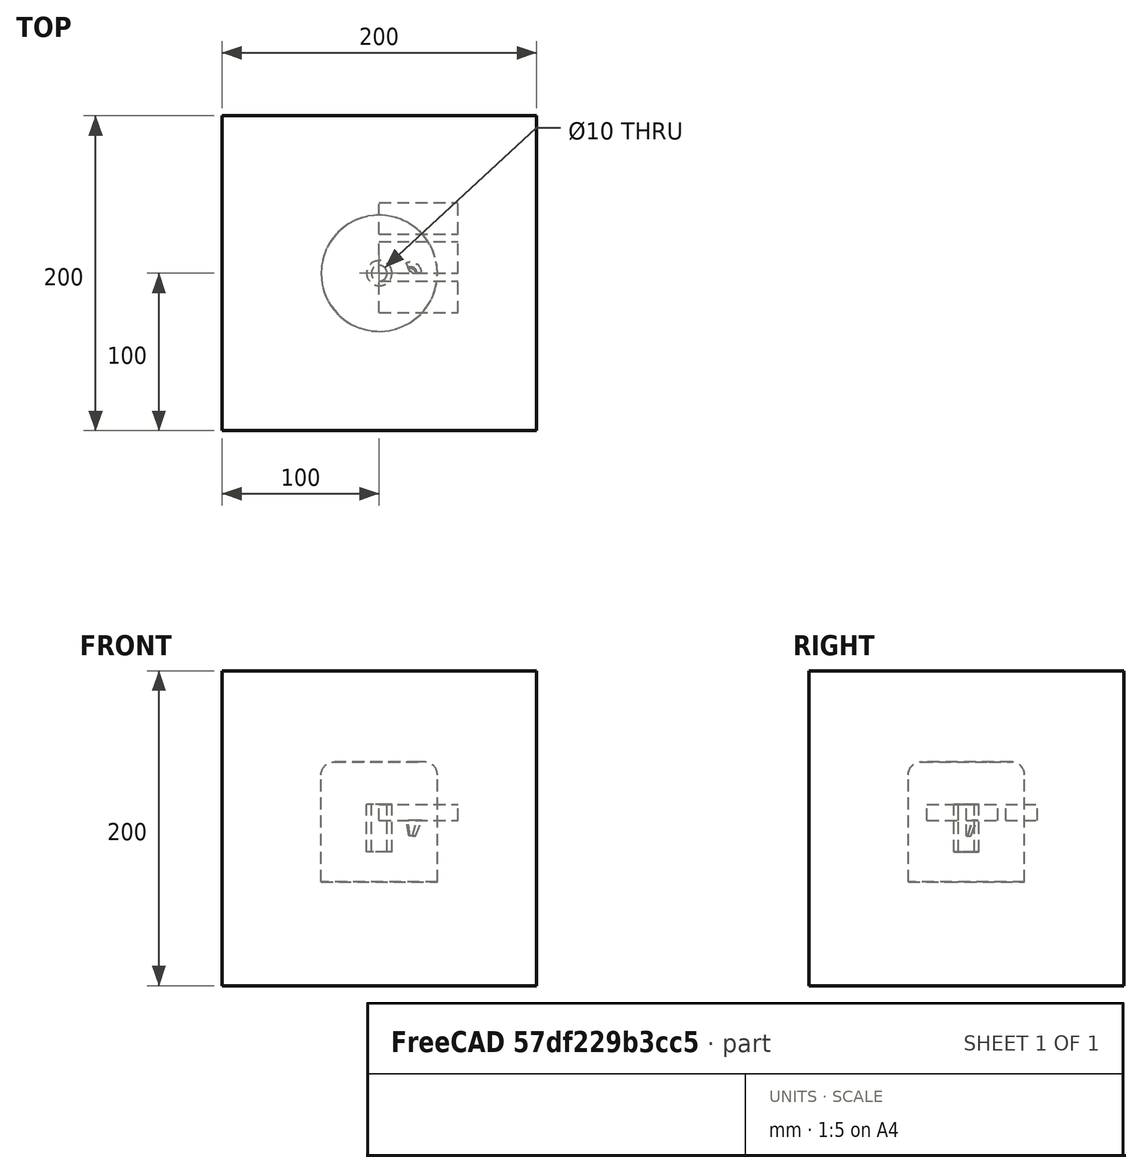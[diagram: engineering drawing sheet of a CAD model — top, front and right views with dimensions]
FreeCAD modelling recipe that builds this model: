
FCSTD DOCUMENT  (FreeCAD 0.19RUnknown)
Label: assemblyTest
License: All rights reserved
LicenseURL: http://en.wikipedia.org/wiki/All_rights_reserved
objects: App::DocumentObjectGroupPython×1254, Part::FeaturePython×6, App::Part×5, Part::Box×3, Part::Fuse×2
note: 11 computed .brp shape members not serialized (recipe doc carries the construction recipe); baked Part::Feature solids carry a one-line shape summary decoded from their .brp

FEATURE [App::DocumentObjectGroupPython] HALFPI  # scripted group (container) (typed FeaturePython)
  name = HALFPI
  value = pi/2.
FEATURE [App::DocumentObjectGroupPython] PI  # scripted group (container) (typed FeaturePython)
  name = PI
  value = 1.*pi
FEATURE [App::DocumentObjectGroupPython] TWOPI  # scripted group (container) (typed FeaturePython)
  name = TWOPI
  value = 2.*pi
FEATURE [App::DocumentObjectGroupPython] Variables  # scripted group (container) (typed FeaturePython)
FEATURE [App::DocumentObjectGroupPython] Quantities  # scripted group (container) (typed FeaturePython)
FEATURE [App::DocumentObjectGroupPython] Isotopes  # scripted group (container) (typed FeaturePython)
FEATURE [App::DocumentObjectGroupPython] Elements  # scripted group (container) (typed FeaturePython)
FEATURE [App::DocumentObjectGroupPython] G4Isotopes  # scripted group (container) (typed FeaturePython)
FEATURE [App::DocumentObjectGroupPython] H_element  # scripted group (container) (typed FeaturePython)
  Z = 1
  atom_value = 1.008
  formula = H
  name = H_element
FEATURE [App::DocumentObjectGroupPython] He_element  # scripted group (container) (typed FeaturePython)
  Z = 2
  atom_value = 4.0026
  formula = He
  name = He_element
FEATURE [App::DocumentObjectGroupPython] Li_element  # scripted group (container) (typed FeaturePython)
  Z = 3
  atom_value = 6.94
  formula = Li
  name = Li_element
FEATURE [App::DocumentObjectGroupPython] Be_element  # scripted group (container) (typed FeaturePython)
  Z = 4
  atom_value = 9.01218
  formula = Be
  name = Be_element
FEATURE [App::DocumentObjectGroupPython] B_element  # scripted group (container) (typed FeaturePython)
  Z = 5
  atom_value = 10.81
  formula = B
  name = B_element
FEATURE [App::DocumentObjectGroupPython] C_element  # scripted group (container) (typed FeaturePython)
  Z = 6
  atom_value = 12.011
  formula = C
  name = C_element
FEATURE [App::DocumentObjectGroupPython] N_element  # scripted group (container) (typed FeaturePython)
  Z = 7
  atom_value = 14.007
  formula = N
  name = N_element
FEATURE [App::DocumentObjectGroupPython] O_element  # scripted group (container) (typed FeaturePython)
  Z = 8
  atom_value = 15.999
  formula = O
  name = O_element
FEATURE [App::DocumentObjectGroupPython] F_element  # scripted group (container) (typed FeaturePython)
  Z = 9
  atom_value = 18.9984
  formula = F
  name = F_element
FEATURE [App::DocumentObjectGroupPython] Ne_element  # scripted group (container) (typed FeaturePython)
  Z = 10
  atom_value = 20.1797
  formula = Ne
  name = Ne_element
FEATURE [App::DocumentObjectGroupPython] Na_element  # scripted group (container) (typed FeaturePython)
  Z = 11
  atom_value = 22.9898
  formula = Na
  name = Na_element
FEATURE [App::DocumentObjectGroupPython] Mg_element  # scripted group (container) (typed FeaturePython)
  Z = 12
  atom_value = 24.305
  formula = Mg
  name = Mg_element
FEATURE [App::DocumentObjectGroupPython] Al_element  # scripted group (container) (typed FeaturePython)
  Z = 13
  atom_value = 26.9815
  formula = Al
  name = Al_element
FEATURE [App::DocumentObjectGroupPython] Si_element  # scripted group (container) (typed FeaturePython)
  Z = 14
  atom_value = 28.085
  formula = Si
  name = Si_element
FEATURE [App::DocumentObjectGroupPython] P_element  # scripted group (container) (typed FeaturePython)
  Z = 15
  atom_value = 30.9738
  formula = P
  name = P_element
FEATURE [App::DocumentObjectGroupPython] S_element  # scripted group (container) (typed FeaturePython)
  Z = 16
  atom_value = 32.06
  formula = S
  name = S_element
FEATURE [App::DocumentObjectGroupPython] Cl_element  # scripted group (container) (typed FeaturePython)
  Z = 17
  atom_value = 35.45
  formula = Cl
  name = Cl_element
FEATURE [App::DocumentObjectGroupPython] Ar_element  # scripted group (container) (typed FeaturePython)
  Z = 18
  atom_value = 39.95
  formula = Ar
  name = Ar_element
FEATURE [App::DocumentObjectGroupPython] K_element  # scripted group (container) (typed FeaturePython)
  Z = 19
  atom_value = 39.0983
  formula = K
  name = K_element
FEATURE [App::DocumentObjectGroupPython] Ca_element  # scripted group (container) (typed FeaturePython)
  Z = 20
  atom_value = 40.078
  formula = Ca
  name = Ca_element
FEATURE [App::DocumentObjectGroupPython] Sc_element  # scripted group (container) (typed FeaturePython)
  Z = 21
  atom_value = 44.9559
  formula = Sc
  name = Sc_element
FEATURE [App::DocumentObjectGroupPython] Ti_element  # scripted group (container) (typed FeaturePython)
  Z = 22
  atom_value = 47.867
  formula = Ti
  name = Ti_element
FEATURE [App::DocumentObjectGroupPython] V_element  # scripted group (container) (typed FeaturePython)
  Z = 23
  atom_value = 50.9415
  formula = V
  name = V_element
FEATURE [App::DocumentObjectGroupPython] Cr_element  # scripted group (container) (typed FeaturePython)
  Z = 24
  atom_value = 51.9961
  formula = Cr
  name = Cr_element
FEATURE [App::DocumentObjectGroupPython] Mn_element  # scripted group (container) (typed FeaturePython)
  Z = 25
  atom_value = 54.938
  formula = Mn
  name = Mn_element
FEATURE [App::DocumentObjectGroupPython] Fe_element  # scripted group (container) (typed FeaturePython)
  Z = 26
  atom_value = 55.845
  formula = Fe
  name = Fe_element
FEATURE [App::DocumentObjectGroupPython] Co_element  # scripted group (container) (typed FeaturePython)
  Z = 27
  atom_value = 58.9332
  formula = Co
  name = Co_element
FEATURE [App::DocumentObjectGroupPython] Ni_element  # scripted group (container) (typed FeaturePython)
  Z = 28
  atom_value = 58.6934
  formula = Ni
  name = Ni_element
FEATURE [App::DocumentObjectGroupPython] Cu_element  # scripted group (container) (typed FeaturePython)
  Z = 29
  atom_value = 63.546
  formula = Cu
  name = Cu_element
FEATURE [App::DocumentObjectGroupPython] Zn_element  # scripted group (container) (typed FeaturePython)
  Z = 30
  atom_value = 65.38
  formula = Zn
  name = Zn_element
FEATURE [App::DocumentObjectGroupPython] Ga_element  # scripted group (container) (typed FeaturePython)
  Z = 31
  atom_value = 69.723
  formula = Ga
  name = Ga_element
FEATURE [App::DocumentObjectGroupPython] Ge_element  # scripted group (container) (typed FeaturePython)
  Z = 32
  atom_value = 72.63
  formula = Ge
  name = Ge_element
FEATURE [App::DocumentObjectGroupPython] As_element  # scripted group (container) (typed FeaturePython)
  Z = 33
  atom_value = 74.9216
  formula = As
  name = As_element
FEATURE [App::DocumentObjectGroupPython] Se_element  # scripted group (container) (typed FeaturePython)
  Z = 34
  atom_value = 78.971
  formula = Se
  name = Se_element
FEATURE [App::DocumentObjectGroupPython] Br_element  # scripted group (container) (typed FeaturePython)
  Z = 35
  atom_value = 79.904
  formula = Br
  name = Br_element
FEATURE [App::DocumentObjectGroupPython] Kr_element  # scripted group (container) (typed FeaturePython)
  Z = 36
  atom_value = 83.798
  formula = Kr
  name = Kr_element
FEATURE [App::DocumentObjectGroupPython] Rb_element  # scripted group (container) (typed FeaturePython)
  Z = 37
  atom_value = 85.4678
  formula = Rb
  name = Rb_element
FEATURE [App::DocumentObjectGroupPython] Sr_element  # scripted group (container) (typed FeaturePython)
  Z = 38
  atom_value = 87.62
  formula = Sr
  name = Sr_element
FEATURE [App::DocumentObjectGroupPython] Y_element  # scripted group (container) (typed FeaturePython)
  Z = 39
  atom_value = 88.9058
  formula = Y
  name = Y_element
FEATURE [App::DocumentObjectGroupPython] Zr_element  # scripted group (container) (typed FeaturePython)
  Z = 40
  atom_value = 91.224
  formula = Zr
  name = Zr_element
FEATURE [App::DocumentObjectGroupPython] Nb_element  # scripted group (container) (typed FeaturePython)
  Z = 41
  atom_value = 92.9064
  formula = Nb
  name = Nb_element
FEATURE [App::DocumentObjectGroupPython] Mo_element  # scripted group (container) (typed FeaturePython)
  Z = 42
  atom_value = 95.95
  formula = Mo
  name = Mo_element
FEATURE [App::DocumentObjectGroupPython] Tc_element  # scripted group (container) (typed FeaturePython)
  Z = 43
  atom_value = 97
  formula = Tc
  name = Tc_element
FEATURE [App::DocumentObjectGroupPython] Ru_element  # scripted group (container) (typed FeaturePython)
  Z = 44
  atom_value = 101.07
  formula = Ru
  name = Ru_element
FEATURE [App::DocumentObjectGroupPython] Rh_element  # scripted group (container) (typed FeaturePython)
  Z = 45
  atom_value = 102.905
  formula = Rh
  name = Rh_element
FEATURE [App::DocumentObjectGroupPython] Pd_element  # scripted group (container) (typed FeaturePython)
  Z = 46
  atom_value = 106.42
  formula = Pd
  name = Pd_element
FEATURE [App::DocumentObjectGroupPython] Ag_element  # scripted group (container) (typed FeaturePython)
  Z = 47
  atom_value = 107.868
  formula = Ag
  name = Ag_element
FEATURE [App::DocumentObjectGroupPython] Cd_element  # scripted group (container) (typed FeaturePython)
  Z = 48
  atom_value = 112.414
  formula = Cd
  name = Cd_element
FEATURE [App::DocumentObjectGroupPython] In_element  # scripted group (container) (typed FeaturePython)
  Z = 49
  atom_value = 114.818
  formula = In
  name = In_element
FEATURE [App::DocumentObjectGroupPython] Sn_element  # scripted group (container) (typed FeaturePython)
  Z = 50
  atom_value = 118.71
  formula = Sn
  name = Sn_element
FEATURE [App::DocumentObjectGroupPython] Sb_element  # scripted group (container) (typed FeaturePython)
  Z = 51
  atom_value = 121.76
  formula = Sb
  name = Sb_element
FEATURE [App::DocumentObjectGroupPython] Te_element  # scripted group (container) (typed FeaturePython)
  Z = 52
  atom_value = 127.6
  formula = Te
  name = Te_element
FEATURE [App::DocumentObjectGroupPython] I_element  # scripted group (container) (typed FeaturePython)
  Z = 53
  atom_value = 126.904
  formula = I
  name = I_element
FEATURE [App::DocumentObjectGroupPython] Xe_element  # scripted group (container) (typed FeaturePython)
  Z = 54
  atom_value = 131.293
  formula = Xe
  name = Xe_element
FEATURE [App::DocumentObjectGroupPython] Cs_element  # scripted group (container) (typed FeaturePython)
  Z = 55
  atom_value = 132.905
  formula = Cs
  name = Cs_element
FEATURE [App::DocumentObjectGroupPython] Ba_element  # scripted group (container) (typed FeaturePython)
  Z = 56
  atom_value = 137.327
  formula = Ba
  name = Ba_element
FEATURE [App::DocumentObjectGroupPython] La_element  # scripted group (container) (typed FeaturePython)
  Z = 57
  atom_value = 138.905
  formula = La
  name = La_element
FEATURE [App::DocumentObjectGroupPython] Ce_element  # scripted group (container) (typed FeaturePython)
  Z = 58
  atom_value = 140.116
  formula = Ce
  name = Ce_element
FEATURE [App::DocumentObjectGroupPython] Pr_element  # scripted group (container) (typed FeaturePython)
  Z = 59
  atom_value = 140.908
  formula = Pr
  name = Pr_element
FEATURE [App::DocumentObjectGroupPython] Nd_element  # scripted group (container) (typed FeaturePython)
  Z = 60
  atom_value = 144.242
  formula = Nd
  name = Nd_element
FEATURE [App::DocumentObjectGroupPython] Pm_element  # scripted group (container) (typed FeaturePython)
  Z = 61
  atom_value = 145
  formula = Pm
  name = Pm_element
FEATURE [App::DocumentObjectGroupPython] Sm_element  # scripted group (container) (typed FeaturePython)
  Z = 62
  atom_value = 150.36
  formula = Sm
  name = Sm_element
FEATURE [App::DocumentObjectGroupPython] Eu_element  # scripted group (container) (typed FeaturePython)
  Z = 63
  atom_value = 151.964
  formula = Eu
  name = Eu_element
FEATURE [App::DocumentObjectGroupPython] Gd_element  # scripted group (container) (typed FeaturePython)
  Z = 64
  atom_value = 157.25
  formula = Gd
  name = Gd_element
FEATURE [App::DocumentObjectGroupPython] Tb_element  # scripted group (container) (typed FeaturePython)
  Z = 65
  atom_value = 158.925
  formula = Tb
  name = Tb_element
FEATURE [App::DocumentObjectGroupPython] Dy_element  # scripted group (container) (typed FeaturePython)
  Z = 66
  atom_value = 162.5
  formula = Dy
  name = Dy_element
FEATURE [App::DocumentObjectGroupPython] Ho_element  # scripted group (container) (typed FeaturePython)
  Z = 67
  atom_value = 164.93
  formula = Ho
  name = Ho_element
FEATURE [App::DocumentObjectGroupPython] Er_element  # scripted group (container) (typed FeaturePython)
  Z = 68
  atom_value = 167.259
  formula = Er
  name = Er_element
FEATURE [App::DocumentObjectGroupPython] Tm_element  # scripted group (container) (typed FeaturePython)
  Z = 69
  atom_value = 168.934
  formula = Tm
  name = Tm_element
FEATURE [App::DocumentObjectGroupPython] Yb_element  # scripted group (container) (typed FeaturePython)
  Z = 70
  atom_value = 173.045
  formula = Yb
  name = Yb_element
FEATURE [App::DocumentObjectGroupPython] Lu_element  # scripted group (container) (typed FeaturePython)
  Z = 71
  atom_value = 174.967
  formula = Lu
  name = Lu_element
FEATURE [App::DocumentObjectGroupPython] Hf_element  # scripted group (container) (typed FeaturePython)
  Z = 72
  atom_value = 178.49
  formula = Hf
  name = Hf_element
FEATURE [App::DocumentObjectGroupPython] Ta_element  # scripted group (container) (typed FeaturePython)
  Z = 73
  atom_value = 180.948
  formula = Ta
  name = Ta_element
FEATURE [App::DocumentObjectGroupPython] W_element  # scripted group (container) (typed FeaturePython)
  Z = 74
  atom_value = 183.84
  formula = W
  name = W_element
FEATURE [App::DocumentObjectGroupPython] Re_element  # scripted group (container) (typed FeaturePython)
  Z = 75
  atom_value = 186.207
  formula = Re
  name = Re_element
FEATURE [App::DocumentObjectGroupPython] Os_element  # scripted group (container) (typed FeaturePython)
  Z = 76
  atom_value = 190.23
  formula = Os
  name = Os_element
FEATURE [App::DocumentObjectGroupPython] Ir_element  # scripted group (container) (typed FeaturePython)
  Z = 77
  atom_value = 192.217
  formula = Ir
  name = Ir_element
FEATURE [App::DocumentObjectGroupPython] Pt_element  # scripted group (container) (typed FeaturePython)
  Z = 78
  atom_value = 195.084
  formula = Pt
  name = Pt_element
FEATURE [App::DocumentObjectGroupPython] Au_element  # scripted group (container) (typed FeaturePython)
  Z = 79
  atom_value = 196.967
  formula = Au
  name = Au_element
FEATURE [App::DocumentObjectGroupPython] Hg_element  # scripted group (container) (typed FeaturePython)
  Z = 80
  atom_value = 200.592
  formula = Hg
  name = Hg_element
FEATURE [App::DocumentObjectGroupPython] Tl_element  # scripted group (container) (typed FeaturePython)
  Z = 81
  atom_value = 204.38
  formula = Tl
  name = Tl_element
FEATURE [App::DocumentObjectGroupPython] Pb_element  # scripted group (container) (typed FeaturePython)
  Z = 82
  atom_value = 207.2
  formula = Pb
  name = Pb_element
FEATURE [App::DocumentObjectGroupPython] Bi_element  # scripted group (container) (typed FeaturePython)
  Z = 83
  atom_value = 208.98
  formula = Bi
  name = Bi_element
FEATURE [App::DocumentObjectGroupPython] Po_element  # scripted group (container) (typed FeaturePython)
  Z = 84
  atom_value = 209
  formula = Po
  name = Po_element
FEATURE [App::DocumentObjectGroupPython] At_element  # scripted group (container) (typed FeaturePython)
  Z = 85
  atom_value = 210
  formula = At
  name = At_element
FEATURE [App::DocumentObjectGroupPython] Rn_element  # scripted group (container) (typed FeaturePython)
  Z = 86
  atom_value = 222
  formula = Rn
  name = Rn_element
FEATURE [App::DocumentObjectGroupPython] Fr_element  # scripted group (container) (typed FeaturePython)
  Z = 87
  atom_value = 223
  formula = Fr
  name = Fr_element
FEATURE [App::DocumentObjectGroupPython] Ra_element  # scripted group (container) (typed FeaturePython)
  Z = 88
  atom_value = 226
  formula = Ra
  name = Ra_element
FEATURE [App::DocumentObjectGroupPython] Ac_element  # scripted group (container) (typed FeaturePython)
  Z = 89
  atom_value = 227
  formula = Ac
  name = Ac_element
FEATURE [App::DocumentObjectGroupPython] Th_element  # scripted group (container) (typed FeaturePython)
  Z = 90
  atom_value = 232.038
  formula = Th
  name = Th_element
FEATURE [App::DocumentObjectGroupPython] Pa_element  # scripted group (container) (typed FeaturePython)
  Z = 91
  atom_value = 231.036
  formula = Pa
  name = Pa_element
FEATURE [App::DocumentObjectGroupPython] U_element  # scripted group (container) (typed FeaturePython)
  Z = 92
  atom_value = 238.029
  formula = U
  name = U_element
FEATURE [App::DocumentObjectGroupPython] Np_element  # scripted group (container) (typed FeaturePython)
  Z = 93
  atom_value = 237
  formula = Np
  name = Np_element
FEATURE [App::DocumentObjectGroupPython] Pu_element  # scripted group (container) (typed FeaturePython)
  Z = 94
  atom_value = 244
  formula = Pu
  name = Pu_element
FEATURE [App::DocumentObjectGroupPython] Am_element  # scripted group (container) (typed FeaturePython)
  Z = 95
  atom_value = 243
  formula = Am
  name = Am_element
FEATURE [App::DocumentObjectGroupPython] Cm_element  # scripted group (container) (typed FeaturePython)
  Z = 96
  atom_value = 247
  formula = Cm
  name = Cm_element
FEATURE [App::DocumentObjectGroupPython] Bk_element  # scripted group (container) (typed FeaturePython)
  Z = 97
  atom_value = 247
  formula = Bk
  name = Bk_element
FEATURE [App::DocumentObjectGroupPython] Cf_element  # scripted group (container) (typed FeaturePython)
  Z = 98
  atom_value = 251
  formula = Cf
  name = Cf_element
FEATURE [App::DocumentObjectGroupPython] G4Elements  # scripted group (container) (typed FeaturePython)
  Group = -> [H_element,He_element,Li_element,Be_element,B_element,C_element,N_element,O_element,F_element,Ne_element,Na_element,Mg_element,Al_element,Si_element,P_element,S_element,Cl_element,Ar_element,K_element,Ca_element,Sc_element,Ti_element,V_element,Cr_element,Mn_element,Fe_element,Co_element,Ni_element,Cu_element,Zn_element,Ga_element,Ge_element,As_element,Se_element,Br_element,Kr_element,Rb_element,+61 more]
FEATURE [Part::FeaturePython] GDMLBox_WorldBox  # WARN: FeaturePython — macro-defined, semantics opaque (R4)
  lunit = 2
  material = 5
  x = 200
  y = 200
  z = 200
FEATURE [App::DocumentObjectGroupPython] HALFPI001  # scripted group (container) (typed FeaturePython)
  name = HALFPI
  value = pi/2.
FEATURE [App::DocumentObjectGroupPython] PI001  # scripted group (container) (typed FeaturePython)
  name = PI
  value = 1.*pi
FEATURE [App::DocumentObjectGroupPython] TWOPI001  # scripted group (container) (typed FeaturePython)
  name = TWOPI
  value = 2.*pi
FEATURE [App::DocumentObjectGroupPython] HALFPI001001  # scripted group (container) (typed FeaturePython)
  name = HALFPI001
  value = pi/2.
FEATURE [App::DocumentObjectGroupPython] PI001001  # scripted group (container) (typed FeaturePython)
  name = PI001
  value = 1.*pi
FEATURE [App::DocumentObjectGroupPython] TWOPI001001  # scripted group (container) (typed FeaturePython)
  name = TWOPI001
  value = 2.*pi
FEATURE [App::DocumentObjectGroupPython] Constants  # scripted group (container) (typed FeaturePython)
  Group = -> [HALFPI,PI,TWOPI,HALFPI001,PI001,TWOPI001,HALFPI001001,PI001001,TWOPI001001]
FEATURE [Part::FeaturePython] GDMLTorus_Torus  # WARN: FeaturePython — macro-defined, semantics opaque (R4)
  aunit = deg
  deltaphi = 360
  lunit = 2
  material = 0
  rmax = 8
  rmin = 0
  rtor = 28.9
  startphi = 0
FEATURE [Part::FeaturePython] GDMLTube_Tube  # WARN: FeaturePython — macro-defined, semantics opaque (R4)
  aunit = 1
  deltaphi = 360
  lunit = 2
  material = 0
  rmax = 28.9
  rmin = 0
  startphi = 0
  z = 16
FEATURE [Part::FeaturePython] GDMLTube_Tube001  label="GDMLTube_T_1"  # WARN: FeaturePython — macro-defined, semantics opaque (R4)
  Placement = pos=(0,0,-34) rot=(0,0,-1;0.349066rad)
  aunit = 1
  deltaphi = 360
  lunit = 2
  material = 0
  rmax = 36.9
  rmin = 0
  startphi = 0
  z = 68
FEATURE [Part::Fuse] Union
  Base = -> GDMLTorus_Torus
  Placement = pos=(0,0,0) rot=(0,0,1;0.523599rad)
  Tool = -> GDMLTube_Tube
FEATURE [Part::Fuse] Union001  label="U1"
  Base = -> Union
  Placement = pos=(0,0,34) rot=(0,0,1;0rad)
  Tool = -> GDMLTube_Tube001
  material = 211
FEATURE [App::Part] Bool_Union001  label="Detector"
  Group = -> [GDMLTorus_Torus,GDMLTube_Tube,Union,GDMLTube_Tube001,Union001]
  Origin = -> Origin005
FEATURE [Part::FeaturePython] GDMLTube_Tube002  # WARN: FeaturePython — macro-defined, semantics opaque (R4)
  aunit = 1
  deltaphi = 360
  lunit = 2
  material = 109
  rmax = 8
  rmin = 5
  startphi = 0
  z = 30
FEATURE [Part::Box] Box  label="Cube"
  AttacherType = Attacher::AttachEngine3D
  Height = 10
  Length = 50
  Placement = pos=(0,0,5) rot=(0,0,1;0rad)
  Width = 20
  material = 441
FEATURE [Part::Box] Box001  label="Cube001"
  AttacherType = Attacher::AttachEngine3D
  Height = 10
  Length = 50
  Placement = pos=(0,25,5) rot=(0,0,1;0rad)
  Width = 20
  material = 441
FEATURE [Part::Box] Box002  label="Cube002"
  AttacherType = Attacher::AttachEngine3D
  Height = 10
  Length = 50
  Placement = pos=(0,-25,5) rot=(0,0,1;0rad)
  Width = 20
  material = 261
FEATURE [App::Part] Part001  label="shieldAssembly"
  Group = -> [Box,Box001,Box002]
  Origin = -> Origin008
  Placement = pos=(0,0,58) rot=(0,0,1;0rad)
FEATURE [App::DocumentObjectGroupPython] H_element553  label="H_element : 0.246"  # scripted group (container) (typed FeaturePython)
  n = 0.101327
FEATURE [App::DocumentObjectGroupPython] C_element593  label="C_element : 0.974"  # scripted group (container) (typed FeaturePython)
  n = 0.7755
FEATURE [App::DocumentObjectGroupPython] N_element273  label="N_element : 0.828"  # scripted group (container) (typed FeaturePython)
  n = 0.035057
FEATURE [App::DocumentObjectGroupPython] O_element521  label="O_element : 0.966"  # scripted group (container) (typed FeaturePython)
  n = 0.0523159
FEATURE [App::DocumentObjectGroupPython] F_element077  label="F_element : 0.727"  # scripted group (container) (typed FeaturePython)
  n = 0.017422
FEATURE [App::DocumentObjectGroupPython] Ca_element057  label="Ca_element : 0.240"  # scripted group (container) (typed FeaturePython)
  n = 0.018378
FEATURE [App::DocumentObjectGroupPython] G4_A_150_TISSUE  label="G4_A-150_TISSUE"  # scripted group (container) (typed FeaturePython)
  Dunit = g/cm3
  Dvalue = 1.127
  Group = -> [H_element553,C_element593,N_element273,O_element521,F_element077,Ca_element057]
  conduct = 2
  density = 1
  expand = 3
  formula = G4_A-150_TISSUE
  name = G4_A-150_TISSUE
  specific = 4
FEATURE [App::DocumentObjectGroupPython] C_element594  label="C_element : 390"  # scripted group (container) (typed FeaturePython)
  n = 3
  ref = C_element
FEATURE [App::DocumentObjectGroupPython] H_element554  label="H_element : 358"  # scripted group (container) (typed FeaturePython)
  n = 6
  ref = H_element
FEATURE [App::DocumentObjectGroupPython] O_element522  label="O_element : 335"  # scripted group (container) (typed FeaturePython)
  n = 1
  ref = O_element
FEATURE [App::DocumentObjectGroupPython] G4_ACETONE  # scripted group (container) (typed FeaturePython)
  Dunit = g/cm3
  Dvalue = 0.7899
  Group = -> [C_element594,H_element554,O_element522]
  conduct = 2
  density = 1
  expand = 3
  formula = G4_ACETONE
  name = G4_ACETONE
  specific = 4
FEATURE [App::DocumentObjectGroupPython] C_element595  label="C_element : 391"  # scripted group (container) (typed FeaturePython)
  n = 2
  ref = C_element
FEATURE [App::DocumentObjectGroupPython] H_element555  label="H_element : 359"  # scripted group (container) (typed FeaturePython)
  n = 2
  ref = H_element
FEATURE [App::DocumentObjectGroupPython] G4_ACETYLENE  # scripted group (container) (typed FeaturePython)
  Dunit = g/cm3
  Dvalue = 0.0010967
  Group = -> [C_element595,H_element555]
  conduct = 2
  density = 1
  expand = 3
  formula = G4_ACETYLENE
  name = G4_ACETYLENE
  specific = 4
FEATURE [App::DocumentObjectGroupPython] C_element596  label="C_element : 392"  # scripted group (container) (typed FeaturePython)
  n = 5
  ref = C_element
FEATURE [App::DocumentObjectGroupPython] H_element556  label="H_element : 360"  # scripted group (container) (typed FeaturePython)
  n = 5
  ref = H_element
FEATURE [App::DocumentObjectGroupPython] N_element274  label="N_element : 154"  # scripted group (container) (typed FeaturePython)
  n = 5
  ref = N_element
FEATURE [App::DocumentObjectGroupPython] G4_ADENINE  # scripted group (container) (typed FeaturePython)
  Dunit = g/cm3
  Dvalue = 1.6
  Group = -> [C_element596,H_element556,N_element274]
  conduct = 2
  density = 1
  expand = 3
  formula = G4_ADENINE
  name = G4_ADENINE
  specific = 4
FEATURE [App::DocumentObjectGroupPython] H_element557  label="H_element : 0.247"  # scripted group (container) (typed FeaturePython)
  n = 0.114
FEATURE [App::DocumentObjectGroupPython] C_element597  label="C_element : 0.975"  # scripted group (container) (typed FeaturePython)
  n = 0.598
FEATURE [App::DocumentObjectGroupPython] N_element275  label="N_element : 0.829"  # scripted group (container) (typed FeaturePython)
  n = 0.007
FEATURE [App::DocumentObjectGroupPython] O_element523  label="O_element : 0.967"  # scripted group (container) (typed FeaturePython)
  n = 0.278
FEATURE [App::DocumentObjectGroupPython] Na_element081  label="Na_element : 0.142"  # scripted group (container) (typed FeaturePython)
  n = 0.001
FEATURE [App::DocumentObjectGroupPython] S_element093  label="S_element : 0.065"  # scripted group (container) (typed FeaturePython)
  n = 0.001
FEATURE [App::DocumentObjectGroupPython] Cl_element121  label="Cl_element : 0.627"  # scripted group (container) (typed FeaturePython)
  n = 0.001
FEATURE [App::DocumentObjectGroupPython] G4_ADIPOSE_TISSUE_ICRP  # scripted group (container) (typed FeaturePython)
  Dunit = g/cm3
  Dvalue = 0.95
  Group = -> [H_element557,C_element597,N_element275,O_element523,Na_element081,S_element093,Cl_element121]
  conduct = 2
  density = 1
  expand = 3
  formula = G4_ADIPOSE_TISSUE_ICRP
  name = G4_ADIPOSE_TISSUE_ICRP
  specific = 4
FEATURE [App::DocumentObjectGroupPython] C_element598  label="C_element : 0.976"  # scripted group (container) (typed FeaturePython)
  n = 0.000124
FEATURE [App::DocumentObjectGroupPython] N_element276  label="N_element : 0.830"  # scripted group (container) (typed FeaturePython)
  n = 0.755268
FEATURE [App::DocumentObjectGroupPython] O_element524  label="O_element : 0.968"  # scripted group (container) (typed FeaturePython)
  n = 0.231781
FEATURE [App::DocumentObjectGroupPython] Ar_element009  label="Ar_element : 0.016"  # scripted group (container) (typed FeaturePython)
  n = 0.012827
FEATURE [App::DocumentObjectGroupPython] G4_AIR  # scripted group (container) (typed FeaturePython)
  Dunit = g/cm3
  Dvalue = 0.00120479
  Group = -> [C_element598,N_element276,O_element524,Ar_element009]
  conduct = 2
  density = 1
  expand = 3
  formula = G4_AIR
  name = G4_AIR
  specific = 4
FEATURE [App::DocumentObjectGroupPython] C_element599  label="C_element : 393"  # scripted group (container) (typed FeaturePython)
  n = 3
  ref = C_element
FEATURE [App::DocumentObjectGroupPython] H_element558  label="H_element : 361"  # scripted group (container) (typed FeaturePython)
  n = 7
  ref = H_element
FEATURE [App::DocumentObjectGroupPython] N_element277  label="N_element : 155"  # scripted group (container) (typed FeaturePython)
  n = 1
  ref = N_element
FEATURE [App::DocumentObjectGroupPython] O_element525  label="O_element : 336"  # scripted group (container) (typed FeaturePython)
  n = 2
  ref = O_element
FEATURE [App::DocumentObjectGroupPython] G4_ALANINE  # scripted group (container) (typed FeaturePython)
  Dunit = g/cm3
  Dvalue = 1.42
  Group = -> [C_element599,H_element558,N_element277,O_element525]
  conduct = 2
  density = 1
  expand = 3
  formula = G4_ALANINE
  name = G4_ALANINE
  specific = 4
FEATURE [App::DocumentObjectGroupPython] Al_element017  label="Al_element : 007"  # scripted group (container) (typed FeaturePython)
  n = 2
  ref = Al_element
FEATURE [App::DocumentObjectGroupPython] O_element526  label="O_element : 337"  # scripted group (container) (typed FeaturePython)
  n = 3
  ref = O_element
FEATURE [App::DocumentObjectGroupPython] G4_ALUMINUM_OXIDE  # scripted group (container) (typed FeaturePython)
  Dunit = g/cm3
  Dvalue = 3.97
  Group = -> [Al_element017,O_element526]
  conduct = 2
  density = 1
  expand = 3
  formula = G4_ALUMINUM_OXIDE
  name = G4_ALUMINUM_OXIDE
  specific = 4
FEATURE [App::DocumentObjectGroupPython] H_element559  label="H_element : 0.248"  # scripted group (container) (typed FeaturePython)
  n = 0.10593
FEATURE [App::DocumentObjectGroupPython] C_element600  label="C_element : 0.977"  # scripted group (container) (typed FeaturePython)
  n = 0.788974
FEATURE [App::DocumentObjectGroupPython] O_element527  label="O_element : 0.969"  # scripted group (container) (typed FeaturePython)
  n = 0.105096
FEATURE [App::DocumentObjectGroupPython] G4_AMBER  # scripted group (container) (typed FeaturePython)
  Dunit = g/cm3
  Dvalue = 1.1
  Group = -> [H_element559,C_element600,O_element527]
  conduct = 2
  density = 1
  expand = 3
  formula = G4_AMBER
  name = G4_AMBER
  specific = 4
FEATURE [App::DocumentObjectGroupPython] N_element278  label="N_element : 156"  # scripted group (container) (typed FeaturePython)
  n = 1
  ref = N_element
FEATURE [App::DocumentObjectGroupPython] H_element560  label="H_element : 362"  # scripted group (container) (typed FeaturePython)
  n = 3
  ref = H_element
FEATURE [App::DocumentObjectGroupPython] G4_AMMONIA  # scripted group (container) (typed FeaturePython)
  Dunit = g/cm3
  Dvalue = 0.000826019
  Group = -> [N_element278,H_element560]
  conduct = 2
  density = 1
  expand = 3
  formula = G4_AMMONIA
  name = G4_AMMONIA
  specific = 4
FEATURE [App::DocumentObjectGroupPython] C_element601  label="C_element : 394"  # scripted group (container) (typed FeaturePython)
  n = 6
  ref = C_element
FEATURE [App::DocumentObjectGroupPython] H_element561  label="H_element : 363"  # scripted group (container) (typed FeaturePython)
  n = 7
  ref = H_element
FEATURE [App::DocumentObjectGroupPython] N_element279  label="N_element : 157"  # scripted group (container) (typed FeaturePython)
  n = 1
  ref = N_element
FEATURE [App::DocumentObjectGroupPython] G4_ANILINE  # scripted group (container) (typed FeaturePython)
  Dunit = g/cm3
  Dvalue = 1.0235
  Group = -> [C_element601,H_element561,N_element279]
  conduct = 2
  density = 1
  expand = 3
  formula = G4_ANILINE
  name = G4_ANILINE
  specific = 4
FEATURE [App::DocumentObjectGroupPython] C_element602  label="C_element : 395"  # scripted group (container) (typed FeaturePython)
  n = 14
  ref = C_element
FEATURE [App::DocumentObjectGroupPython] H_element562  label="H_element : 364"  # scripted group (container) (typed FeaturePython)
  n = 10
  ref = H_element
FEATURE [App::DocumentObjectGroupPython] G4_ANTHRACENE  # scripted group (container) (typed FeaturePython)
  Dunit = g/cm3
  Dvalue = 1.283
  Group = -> [C_element602,H_element562]
  conduct = 2
  density = 1
  expand = 3
  formula = G4_ANTHRACENE
  name = G4_ANTHRACENE
  specific = 4
FEATURE [App::DocumentObjectGroupPython] H_element563  label="H_element : 0.249"  # scripted group (container) (typed FeaturePython)
  n = 0.0654709
FEATURE [App::DocumentObjectGroupPython] C_element603  label="C_element : 0.978"  # scripted group (container) (typed FeaturePython)
  n = 0.536944
FEATURE [App::DocumentObjectGroupPython] N_element280  label="N_element : 0.831"  # scripted group (container) (typed FeaturePython)
  n = 0.0215
FEATURE [App::DocumentObjectGroupPython] O_element528  label="O_element : 0.970"  # scripted group (container) (typed FeaturePython)
  n = 0.032085
FEATURE [App::DocumentObjectGroupPython] F_element078  label="F_element : 0.728"  # scripted group (container) (typed FeaturePython)
  n = 0.167411
FEATURE [App::DocumentObjectGroupPython] Ca_element058  label="Ca_element : 0.241"  # scripted group (container) (typed FeaturePython)
  n = 0.176589
FEATURE [App::DocumentObjectGroupPython] G4_B_100_BONE  label="G4_B-100_BONE"  # scripted group (container) (typed FeaturePython)
  Dunit = g/cm3
  Dvalue = 1.45
  Group = -> [H_element563,C_element603,N_element280,O_element528,F_element078,Ca_element058]
  conduct = 2
  density = 1
  expand = 3
  formula = G4_B-100_BONE
  name = G4_B-100_BONE
  specific = 4
FEATURE [App::DocumentObjectGroupPython] H_element564  label="H_element : 0.250"  # scripted group (container) (typed FeaturePython)
  n = 0.057441
FEATURE [App::DocumentObjectGroupPython] C_element604  label="C_element : 0.979"  # scripted group (container) (typed FeaturePython)
  n = 0.774591
FEATURE [App::DocumentObjectGroupPython] O_element529  label="O_element : 0.971"  # scripted group (container) (typed FeaturePython)
  n = 0.167968
FEATURE [App::DocumentObjectGroupPython] G4_BAKELITE  # scripted group (container) (typed FeaturePython)
  Dunit = g/cm3
  Dvalue = 1.25
  Group = -> [H_element564,C_element604,O_element529]
  conduct = 2
  density = 1
  expand = 3
  formula = G4_BAKELITE
  name = G4_BAKELITE
  specific = 4
FEATURE [App::DocumentObjectGroupPython] Ba_element013  label="Ba_element : 012"  # scripted group (container) (typed FeaturePython)
  n = 1
  ref = Ba_element
FEATURE [App::DocumentObjectGroupPython] F_element079  label="F_element : 037"  # scripted group (container) (typed FeaturePython)
  n = 2
  ref = F_element
FEATURE [App::DocumentObjectGroupPython] G4_BARIUM_FLUORIDE  # scripted group (container) (typed FeaturePython)
  Dunit = g/cm3
  Dvalue = 4.89
  Group = -> [Ba_element013,F_element079]
  conduct = 2
  density = 1
  expand = 3
  formula = G4_BARIUM_FLUORIDE
  name = G4_BARIUM_FLUORIDE
  specific = 4
FEATURE [App::DocumentObjectGroupPython] Ba_element014  label="Ba_element : 013"  # scripted group (container) (typed FeaturePython)
  n = 1
  ref = Ba_element
FEATURE [App::DocumentObjectGroupPython] S_element094  label="S_element : 028"  # scripted group (container) (typed FeaturePython)
  n = 1
  ref = S_element
FEATURE [App::DocumentObjectGroupPython] O_element530  label="O_element : 338"  # scripted group (container) (typed FeaturePython)
  n = 4
  ref = O_element
FEATURE [App::DocumentObjectGroupPython] G4_BARIUM_SULFATE  # scripted group (container) (typed FeaturePython)
  Dunit = g/cm3
  Dvalue = 4.5
  Group = -> [Ba_element014,S_element094,O_element530]
  conduct = 2
  density = 1
  expand = 3
  formula = G4_BARIUM_SULFATE
  name = G4_BARIUM_SULFATE
  specific = 4
FEATURE [App::DocumentObjectGroupPython] C_element605  label="C_element : 396"  # scripted group (container) (typed FeaturePython)
  n = 6
  ref = C_element
FEATURE [App::DocumentObjectGroupPython] H_element565  label="H_element : 365"  # scripted group (container) (typed FeaturePython)
  n = 6
  ref = H_element
FEATURE [App::DocumentObjectGroupPython] G4_BENZENE  # scripted group (container) (typed FeaturePython)
  Dunit = g/cm3
  Dvalue = 0.87865
  Group = -> [C_element605,H_element565]
  conduct = 2
  density = 1
  expand = 3
  formula = G4_BENZENE
  name = G4_BENZENE
  specific = 4
FEATURE [App::DocumentObjectGroupPython] Be_element009  label="Be_element : 008"  # scripted group (container) (typed FeaturePython)
  n = 1
  ref = Be_element
FEATURE [App::DocumentObjectGroupPython] O_element531  label="O_element : 339"  # scripted group (container) (typed FeaturePython)
  n = 1
  ref = O_element
FEATURE [App::DocumentObjectGroupPython] G4_BERYLLIUM_OXIDE  # scripted group (container) (typed FeaturePython)
  Dunit = g/cm3
  Dvalue = 3.01
  Group = -> [Be_element009,O_element531]
  conduct = 2
  density = 1
  expand = 3
  formula = G4_BERYLLIUM_OXIDE
  name = G4_BERYLLIUM_OXIDE
  specific = 4
FEATURE [App::DocumentObjectGroupPython] Bi_element009  label="Bi_element : 009"  # scripted group (container) (typed FeaturePython)
  n = 4
  ref = Bi_element
FEATURE [App::DocumentObjectGroupPython] Ge_element009  label="Ge_element : 008"  # scripted group (container) (typed FeaturePython)
  n = 3
  ref = Ge_element
FEATURE [App::DocumentObjectGroupPython] O_element532  label="O_element : 340"  # scripted group (container) (typed FeaturePython)
  n = 12
  ref = O_element
FEATURE [App::DocumentObjectGroupPython] G4_BGO  # scripted group (container) (typed FeaturePython)
  Dunit = g/cm3
  Dvalue = 7.13
  Group = -> [Bi_element009,Ge_element009,O_element532]
  conduct = 2
  density = 1
  expand = 3
  formula = G4_BGO
  name = G4_BGO
  specific = 4
FEATURE [App::DocumentObjectGroupPython] H_element566  label="H_element : 0.251"  # scripted group (container) (typed FeaturePython)
  n = 0.102
FEATURE [App::DocumentObjectGroupPython] C_element606  label="C_element : 0.980"  # scripted group (container) (typed FeaturePython)
  n = 0.11
FEATURE [App::DocumentObjectGroupPython] N_element281  label="N_element : 0.832"  # scripted group (container) (typed FeaturePython)
  n = 0.033
FEATURE [App::DocumentObjectGroupPython] O_element533  label="O_element : 0.972"  # scripted group (container) (typed FeaturePython)
  n = 0.745
FEATURE [App::DocumentObjectGroupPython] Na_element082  label="Na_element : 0.143"  # scripted group (container) (typed FeaturePython)
  n = 0.001
FEATURE [App::DocumentObjectGroupPython] P_element077  label="P_element : 0.138"  # scripted group (container) (typed FeaturePython)
  n = 0.001
FEATURE [App::DocumentObjectGroupPython] S_element095  label="S_element : 0.066"  # scripted group (container) (typed FeaturePython)
  n = 0.002
FEATURE [App::DocumentObjectGroupPython] Cl_element122  label="Cl_element : 0.628"  # scripted group (container) (typed FeaturePython)
  n = 0.003
FEATURE [App::DocumentObjectGroupPython] K_element053  label="K_element : 0.044"  # scripted group (container) (typed FeaturePython)
  n = 0.002
FEATURE [App::DocumentObjectGroupPython] Fe_element033  label="Fe_element : 0.021"  # scripted group (container) (typed FeaturePython)
  n = 0.001
FEATURE [App::DocumentObjectGroupPython] G4_BLOOD_ICRP  # scripted group (container) (typed FeaturePython)
  Dunit = g/cm3
  Dvalue = 1.06
  Group = -> [H_element566,C_element606,N_element281,O_element533,Na_element082,P_element077,S_element095,Cl_element122,K_element053,Fe_element033]
  conduct = 2
  density = 1
  expand = 3
  formula = G4_BLOOD_ICRP
  name = G4_BLOOD_ICRP
  specific = 4
FEATURE [App::DocumentObjectGroupPython] H_element567  label="H_element : 0.252"  # scripted group (container) (typed FeaturePython)
  n = 0.064
FEATURE [App::DocumentObjectGroupPython] C_element607  label="C_element : 0.981"  # scripted group (container) (typed FeaturePython)
  n = 0.278
FEATURE [App::DocumentObjectGroupPython] N_element282  label="N_element : 0.833"  # scripted group (container) (typed FeaturePython)
  n = 0.027
FEATURE [App::DocumentObjectGroupPython] O_element534  label="O_element : 0.973"  # scripted group (container) (typed FeaturePython)
  n = 0.41
FEATURE [App::DocumentObjectGroupPython] Mg_element045  label="Mg_element : 0.150"  # scripted group (container) (typed FeaturePython)
  n = 0.002
FEATURE [App::DocumentObjectGroupPython] P_element078  label="P_element : 0.139"  # scripted group (container) (typed FeaturePython)
  n = 0.07
FEATURE [App::DocumentObjectGroupPython] S_element096  label="S_element : 0.067"  # scripted group (container) (typed FeaturePython)
  n = 0.002
FEATURE [App::DocumentObjectGroupPython] Ca_element059  label="Ca_element : 0.242"  # scripted group (container) (typed FeaturePython)
  n = 0.147
FEATURE [App::DocumentObjectGroupPython] G4_BONE_COMPACT_ICRU  # scripted group (container) (typed FeaturePython)
  Dunit = g/cm3
  Dvalue = 1.85
  Group = -> [H_element567,C_element607,N_element282,O_element534,Mg_element045,P_element078,S_element096,Ca_element059]
  conduct = 2
  density = 1
  expand = 3
  formula = G4_BONE_COMPACT_ICRU
  name = G4_BONE_COMPACT_ICRU
  specific = 4
FEATURE [App::DocumentObjectGroupPython] H_element568  label="H_element : 0.253"  # scripted group (container) (typed FeaturePython)
  n = 0.034
FEATURE [App::DocumentObjectGroupPython] C_element608  label="C_element : 0.982"  # scripted group (container) (typed FeaturePython)
  n = 0.155
FEATURE [App::DocumentObjectGroupPython] N_element283  label="N_element : 0.834"  # scripted group (container) (typed FeaturePython)
  n = 0.042
FEATURE [App::DocumentObjectGroupPython] O_element535  label="O_element : 0.974"  # scripted group (container) (typed FeaturePython)
  n = 0.435
FEATURE [App::DocumentObjectGroupPython] Na_element083  label="Na_element : 0.144"  # scripted group (container) (typed FeaturePython)
  n = 0.001
FEATURE [App::DocumentObjectGroupPython] Mg_element046  label="Mg_element : 0.151"  # scripted group (container) (typed FeaturePython)
  n = 0.002
FEATURE [App::DocumentObjectGroupPython] P_element079  label="P_element : 0.140"  # scripted group (container) (typed FeaturePython)
  n = 0.103
FEATURE [App::DocumentObjectGroupPython] S_element097  label="S_element : 0.068"  # scripted group (container) (typed FeaturePython)
  n = 0.003
FEATURE [App::DocumentObjectGroupPython] Ca_element060  label="Ca_element : 0.243"  # scripted group (container) (typed FeaturePython)
  n = 0.225
FEATURE [App::DocumentObjectGroupPython] G4_BONE_CORTICAL_ICRP  # scripted group (container) (typed FeaturePython)
  Dunit = g/cm3
  Dvalue = 1.92
  Group = -> [H_element568,C_element608,N_element283,O_element535,Na_element083,Mg_element046,P_element079,S_element097,Ca_element060]
  conduct = 2
  density = 1
  expand = 3
  formula = G4_BONE_CORTICAL_ICRP
  name = G4_BONE_CORTICAL_ICRP
  specific = 4
FEATURE [App::DocumentObjectGroupPython] B_element029  label="B_element : 023"  # scripted group (container) (typed FeaturePython)
  n = 4
  ref = B_element
FEATURE [App::DocumentObjectGroupPython] C_element609  label="C_element : 397"  # scripted group (container) (typed FeaturePython)
  n = 1
  ref = C_element
FEATURE [App::DocumentObjectGroupPython] G4_BORON_CARBIDE  # scripted group (container) (typed FeaturePython)
  Dunit = g/cm3
  Dvalue = 2.52
  Group = -> [B_element029,C_element609]
  conduct = 2
  density = 1
  expand = 3
  formula = G4_BORON_CARBIDE
  name = G4_BORON_CARBIDE
  specific = 4
FEATURE [App::DocumentObjectGroupPython] B_element030  label="B_element : 024"  # scripted group (container) (typed FeaturePython)
  n = 2
  ref = B_element
FEATURE [App::DocumentObjectGroupPython] O_element536  label="O_element : 341"  # scripted group (container) (typed FeaturePython)
  n = 3
  ref = O_element
FEATURE [App::DocumentObjectGroupPython] G4_BORON_OXIDE  # scripted group (container) (typed FeaturePython)
  Dunit = g/cm3
  Dvalue = 1.812
  Group = -> [B_element030,O_element536]
  conduct = 2
  density = 1
  expand = 3
  formula = G4_BORON_OXIDE
  name = G4_BORON_OXIDE
  specific = 4
FEATURE [App::DocumentObjectGroupPython] H_element569  label="H_element : 0.254"  # scripted group (container) (typed FeaturePython)
  n = 0.107
FEATURE [App::DocumentObjectGroupPython] C_element610  label="C_element : 0.983"  # scripted group (container) (typed FeaturePython)
  n = 0.145
FEATURE [App::DocumentObjectGroupPython] N_element284  label="N_element : 0.835"  # scripted group (container) (typed FeaturePython)
  n = 0.022
FEATURE [App::DocumentObjectGroupPython] O_element537  label="O_element : 0.975"  # scripted group (container) (typed FeaturePython)
  n = 0.712
FEATURE [App::DocumentObjectGroupPython] Na_element084  label="Na_element : 0.145"  # scripted group (container) (typed FeaturePython)
  n = 0.002
FEATURE [App::DocumentObjectGroupPython] P_element080  label="P_element : 0.141"  # scripted group (container) (typed FeaturePython)
  n = 0.004
FEATURE [App::DocumentObjectGroupPython] S_element098  label="S_element : 0.069"  # scripted group (container) (typed FeaturePython)
  n = 0.002
FEATURE [App::DocumentObjectGroupPython] Cl_element123  label="Cl_element : 0.629"  # scripted group (container) (typed FeaturePython)
  n = 0.003
FEATURE [App::DocumentObjectGroupPython] K_element054  label="K_element : 0.045"  # scripted group (container) (typed FeaturePython)
  n = 0.003
FEATURE [App::DocumentObjectGroupPython] G4_BRAIN_ICRP  # scripted group (container) (typed FeaturePython)
  Dunit = g/cm3
  Dvalue = 1.04
  Group = -> [H_element569,C_element610,N_element284,O_element537,Na_element084,P_element080,S_element098,Cl_element123,K_element054]
  conduct = 2
  density = 1
  expand = 3
  formula = G4_BRAIN_ICRP
  name = G4_BRAIN_ICRP
  specific = 4
FEATURE [App::DocumentObjectGroupPython] C_element611  label="C_element : 398"  # scripted group (container) (typed FeaturePython)
  n = 4
  ref = C_element
FEATURE [App::DocumentObjectGroupPython] H_element570  label="H_element : 366"  # scripted group (container) (typed FeaturePython)
  n = 10
  ref = H_element
FEATURE [App::DocumentObjectGroupPython] G4_BUTANE  # scripted group (container) (typed FeaturePython)
  Dunit = g/cm3
  Dvalue = 0.00249343
  Group = -> [C_element611,H_element570]
  conduct = 2
  density = 1
  expand = 3
  formula = G4_BUTANE
  name = G4_BUTANE
  specific = 4
FEATURE [App::DocumentObjectGroupPython] C_element612  label="C_element : 399"  # scripted group (container) (typed FeaturePython)
  n = 4
  ref = C_element
FEATURE [App::DocumentObjectGroupPython] H_element571  label="H_element : 367"  # scripted group (container) (typed FeaturePython)
  n = 10
  ref = H_element
FEATURE [App::DocumentObjectGroupPython] O_element538  label="O_element : 342"  # scripted group (container) (typed FeaturePython)
  n = 1
  ref = O_element
FEATURE [App::DocumentObjectGroupPython] G4_N_BUTYL_ALCOHOL  label="G4_N-BUTYL_ALCOHOL"  # scripted group (container) (typed FeaturePython)
  Dunit = g/cm3
  Dvalue = 0.8098
  Group = -> [C_element612,H_element571,O_element538]
  conduct = 2
  density = 1
  expand = 3
  formula = G4_N-BUTYL_ALCOHOL
  name = G4_N-BUTYL_ALCOHOL
  specific = 4
FEATURE [App::DocumentObjectGroupPython] H_element572  label="H_element : 0.255"  # scripted group (container) (typed FeaturePython)
  n = 0.02468
FEATURE [App::DocumentObjectGroupPython] C_element613  label="C_element : 0.984"  # scripted group (container) (typed FeaturePython)
  n = 0.501611
FEATURE [App::DocumentObjectGroupPython] O_element539  label="O_element : 0.976"  # scripted group (container) (typed FeaturePython)
  n = 0.004527
FEATURE [App::DocumentObjectGroupPython] F_element080  label="F_element : 0.729"  # scripted group (container) (typed FeaturePython)
  n = 0.465209
FEATURE [App::DocumentObjectGroupPython] Si_element029  label="Si_element : 0.390"  # scripted group (container) (typed FeaturePython)
  n = 0.003973
FEATURE [App::DocumentObjectGroupPython] G4_C_552  label="G4_C-552"  # scripted group (container) (typed FeaturePython)
  Dunit = g/cm3
  Dvalue = 1.76
  Group = -> [H_element572,C_element613,O_element539,F_element080,Si_element029]
  conduct = 2
  density = 1
  expand = 3
  formula = G4_C-552
  name = G4_C-552
  specific = 4
FEATURE [App::DocumentObjectGroupPython] Cd_element013  label="Cd_element : 012"  # scripted group (container) (typed FeaturePython)
  n = 1
  ref = Cd_element
FEATURE [App::DocumentObjectGroupPython] Te_element009  label="Te_element : 008"  # scripted group (container) (typed FeaturePython)
  n = 1
  ref = Te_element
FEATURE [App::DocumentObjectGroupPython] G4_CADMIUM_TELLURIDE  # scripted group (container) (typed FeaturePython)
  Dunit = g/cm3
  Dvalue = 6.2
  Group = -> [Cd_element013,Te_element009]
  conduct = 2
  density = 1
  expand = 3
  formula = G4_CADMIUM_TELLURIDE
  name = G4_CADMIUM_TELLURIDE
  specific = 4
FEATURE [App::DocumentObjectGroupPython] Cd_element014  label="Cd_element : 013"  # scripted group (container) (typed FeaturePython)
  n = 1
  ref = Cd_element
FEATURE [App::DocumentObjectGroupPython] W_element021  label="W_element : 020"  # scripted group (container) (typed FeaturePython)
  n = 1
  ref = W_element
FEATURE [App::DocumentObjectGroupPython] O_element540  label="O_element : 343"  # scripted group (container) (typed FeaturePython)
  n = 4
  ref = O_element
FEATURE [App::DocumentObjectGroupPython] G4_CADMIUM_TUNGSTATE  # scripted group (container) (typed FeaturePython)
  Dunit = g/cm3
  Dvalue = 7.9
  Group = -> [Cd_element014,W_element021,O_element540]
  conduct = 2
  density = 1
  expand = 3
  formula = G4_CADMIUM_TUNGSTATE
  name = G4_CADMIUM_TUNGSTATE
  specific = 4
FEATURE [App::DocumentObjectGroupPython] Ca_element061  label="Ca_element : 028"  # scripted group (container) (typed FeaturePython)
  n = 1
  ref = Ca_element
FEATURE [App::DocumentObjectGroupPython] C_element614  label="C_element : 400"  # scripted group (container) (typed FeaturePython)
  n = 1
  ref = C_element
FEATURE [App::DocumentObjectGroupPython] O_element541  label="O_element : 344"  # scripted group (container) (typed FeaturePython)
  n = 3
  ref = O_element
FEATURE [App::DocumentObjectGroupPython] G4_CALCIUM_CARBONATE  # scripted group (container) (typed FeaturePython)
  Dunit = g/cm3
  Dvalue = 2.8
  Group = -> [Ca_element061,C_element614,O_element541]
  conduct = 2
  density = 1
  expand = 3
  formula = G4_CALCIUM_CARBONATE
  name = G4_CALCIUM_CARBONATE
  specific = 4
FEATURE [App::DocumentObjectGroupPython] Ca_element062  label="Ca_element : 029"  # scripted group (container) (typed FeaturePython)
  n = 1
  ref = Ca_element
FEATURE [App::DocumentObjectGroupPython] F_element081  label="F_element : 038"  # scripted group (container) (typed FeaturePython)
  n = 2
  ref = F_element
FEATURE [App::DocumentObjectGroupPython] G4_CALCIUM_FLUORIDE  # scripted group (container) (typed FeaturePython)
  Dunit = g/cm3
  Dvalue = 3.18
  Group = -> [Ca_element062,F_element081]
  conduct = 2
  density = 1
  expand = 3
  formula = G4_CALCIUM_FLUORIDE
  name = G4_CALCIUM_FLUORIDE
  specific = 4
FEATURE [App::DocumentObjectGroupPython] Ca_element063  label="Ca_element : 030"  # scripted group (container) (typed FeaturePython)
  n = 1
  ref = Ca_element
FEATURE [App::DocumentObjectGroupPython] O_element542  label="O_element : 345"  # scripted group (container) (typed FeaturePython)
  n = 1
  ref = O_element
FEATURE [App::DocumentObjectGroupPython] G4_CALCIUM_OXIDE  # scripted group (container) (typed FeaturePython)
  Dunit = g/cm3
  Dvalue = 3.3
  Group = -> [Ca_element063,O_element542]
  conduct = 2
  density = 1
  expand = 3
  formula = G4_CALCIUM_OXIDE
  name = G4_CALCIUM_OXIDE
  specific = 4
FEATURE [App::DocumentObjectGroupPython] Ca_element064  label="Ca_element : 031"  # scripted group (container) (typed FeaturePython)
  n = 1
  ref = Ca_element
FEATURE [App::DocumentObjectGroupPython] S_element099  label="S_element : 029"  # scripted group (container) (typed FeaturePython)
  n = 1
  ref = S_element
FEATURE [App::DocumentObjectGroupPython] O_element543  label="O_element : 346"  # scripted group (container) (typed FeaturePython)
  n = 4
  ref = O_element
FEATURE [App::DocumentObjectGroupPython] G4_CALCIUM_SULFATE  # scripted group (container) (typed FeaturePython)
  Dunit = g/cm3
  Dvalue = 2.96
  Group = -> [Ca_element064,S_element099,O_element543]
  conduct = 2
  density = 1
  expand = 3
  formula = G4_CALCIUM_SULFATE
  name = G4_CALCIUM_SULFATE
  specific = 4
FEATURE [App::DocumentObjectGroupPython] Ca_element065  label="Ca_element : 032"  # scripted group (container) (typed FeaturePython)
  n = 1
  ref = Ca_element
FEATURE [App::DocumentObjectGroupPython] W_element022  label="W_element : 021"  # scripted group (container) (typed FeaturePython)
  n = 1
  ref = W_element
FEATURE [App::DocumentObjectGroupPython] O_element544  label="O_element : 347"  # scripted group (container) (typed FeaturePython)
  n = 4
  ref = O_element
FEATURE [App::DocumentObjectGroupPython] G4_CALCIUM_TUNGSTATE  # scripted group (container) (typed FeaturePython)
  Dunit = g/cm3
  Dvalue = 6.062
  Group = -> [Ca_element065,W_element022,O_element544]
  conduct = 2
  density = 1
  expand = 3
  formula = G4_CALCIUM_TUNGSTATE
  name = G4_CALCIUM_TUNGSTATE
  specific = 4
FEATURE [App::DocumentObjectGroupPython] C_element615  label="C_element : 401"  # scripted group (container) (typed FeaturePython)
  n = 1
  ref = C_element
FEATURE [App::DocumentObjectGroupPython] O_element545  label="O_element : 348"  # scripted group (container) (typed FeaturePython)
  n = 2
  ref = O_element
FEATURE [App::DocumentObjectGroupPython] G4_CARBON_DIOXIDE  # scripted group (container) (typed FeaturePython)
  Dunit = g/cm3
  Dvalue = 0.00184212
  Group = -> [C_element615,O_element545]
  conduct = 2
  density = 1
  expand = 3
  formula = G4_CARBON_DIOXIDE
  name = G4_CARBON_DIOXIDE
  specific = 4
FEATURE [App::DocumentObjectGroupPython] C_element616  label="C_element : 402"  # scripted group (container) (typed FeaturePython)
  n = 1
  ref = C_element
FEATURE [App::DocumentObjectGroupPython] Cl_element124  label="Cl_element : 061"  # scripted group (container) (typed FeaturePython)
  n = 4
  ref = Cl_element
FEATURE [App::DocumentObjectGroupPython] G4_CARBON_TETRACHLORIDE  # scripted group (container) (typed FeaturePython)
  Dunit = g/cm3
  Dvalue = 1.594
  Group = -> [C_element616,Cl_element124]
  conduct = 2
  density = 1
  expand = 3
  formula = G4_CARBON_TETRACHLORIDE
  name = G4_CARBON_TETRACHLORIDE
  specific = 4
FEATURE [App::DocumentObjectGroupPython] C_element617  label="C_element : 403"  # scripted group (container) (typed FeaturePython)
  n = 6
  ref = C_element
FEATURE [App::DocumentObjectGroupPython] H_element573  label="H_element : 368"  # scripted group (container) (typed FeaturePython)
  n = 10
  ref = H_element
FEATURE [App::DocumentObjectGroupPython] O_element546  label="O_element : 349"  # scripted group (container) (typed FeaturePython)
  n = 5
  ref = O_element
FEATURE [App::DocumentObjectGroupPython] G4_CELLULOSE_CELLOPHANE  # scripted group (container) (typed FeaturePython)
  Dunit = g/cm3
  Dvalue = 1.42
  Group = -> [C_element617,H_element573,O_element546]
  conduct = 2
  density = 1
  expand = 3
  formula = G4_CELLULOSE_CELLOPHANE
  name = G4_CELLULOSE_CELLOPHANE
  specific = 4
FEATURE [App::DocumentObjectGroupPython] H_element574  label="H_element : 0.256"  # scripted group (container) (typed FeaturePython)
  n = 0.067125
FEATURE [App::DocumentObjectGroupPython] C_element618  label="C_element : 0.985"  # scripted group (container) (typed FeaturePython)
  n = 0.545403
FEATURE [App::DocumentObjectGroupPython] O_element547  label="O_element : 0.977"  # scripted group (container) (typed FeaturePython)
  n = 0.387472
FEATURE [App::DocumentObjectGroupPython] G4_CELLULOSE_BUTYRATE  # scripted group (container) (typed FeaturePython)
  Dunit = g/cm3
  Dvalue = 1.2
  Group = -> [H_element574,C_element618,O_element547]
  conduct = 2
  density = 1
  expand = 3
  formula = G4_CELLULOSE_BUTYRATE
  name = G4_CELLULOSE_BUTYRATE
  specific = 4
FEATURE [App::DocumentObjectGroupPython] H_element575  label="H_element : 0.257"  # scripted group (container) (typed FeaturePython)
  n = 0.029216
FEATURE [App::DocumentObjectGroupPython] C_element619  label="C_element : 0.986"  # scripted group (container) (typed FeaturePython)
  n = 0.271296
FEATURE [App::DocumentObjectGroupPython] N_element285  label="N_element : 0.836"  # scripted group (container) (typed FeaturePython)
  n = 0.121276
FEATURE [App::DocumentObjectGroupPython] O_element548  label="O_element : 0.978"  # scripted group (container) (typed FeaturePython)
  n = 0.578212
FEATURE [App::DocumentObjectGroupPython] G4_CELLULOSE_NITRATE  # scripted group (container) (typed FeaturePython)
  Dunit = g/cm3
  Dvalue = 1.49
  Group = -> [H_element575,C_element619,N_element285,O_element548]
  conduct = 2
  density = 1
  expand = 3
  formula = G4_CELLULOSE_NITRATE
  name = G4_CELLULOSE_NITRATE
  specific = 4
FEATURE [App::DocumentObjectGroupPython] H_element576  label="H_element : 0.258"  # scripted group (container) (typed FeaturePython)
  n = 0.107596
FEATURE [App::DocumentObjectGroupPython] N_element286  label="N_element : 0.837"  # scripted group (container) (typed FeaturePython)
  n = 0.0008
FEATURE [App::DocumentObjectGroupPython] O_element549  label="O_element : 0.979"  # scripted group (container) (typed FeaturePython)
  n = 0.874976
FEATURE [App::DocumentObjectGroupPython] S_element100  label="S_element : 0.070"  # scripted group (container) (typed FeaturePython)
  n = 0.014627
FEATURE [App::DocumentObjectGroupPython] Ce_element009  label="Ce_element : 0.005"  # scripted group (container) (typed FeaturePython)
  n = 0.002001
FEATURE [App::DocumentObjectGroupPython] G4_CERIC_SULFATE  # scripted group (container) (typed FeaturePython)
  Dunit = g/cm3
  Dvalue = 1.03
  Group = -> [H_element576,N_element286,O_element549,S_element100,Ce_element009]
  conduct = 2
  density = 1
  expand = 3
  formula = G4_CERIC_SULFATE
  name = G4_CERIC_SULFATE
  specific = 4
FEATURE [App::DocumentObjectGroupPython] Cs_element013  label="Cs_element : 012"  # scripted group (container) (typed FeaturePython)
  n = 1
  ref = Cs_element
FEATURE [App::DocumentObjectGroupPython] F_element082  label="F_element : 039"  # scripted group (container) (typed FeaturePython)
  n = 1
  ref = F_element
FEATURE [App::DocumentObjectGroupPython] G4_CESIUM_FLUORIDE  # scripted group (container) (typed FeaturePython)
  Dunit = g/cm3
  Dvalue = 4.115
  Group = -> [Cs_element013,F_element082]
  conduct = 2
  density = 1
  expand = 3
  formula = G4_CESIUM_FLUORIDE
  name = G4_CESIUM_FLUORIDE
  specific = 4
FEATURE [App::DocumentObjectGroupPython] Cs_element014  label="Cs_element : 013"  # scripted group (container) (typed FeaturePython)
  n = 1
  ref = Cs_element
FEATURE [App::DocumentObjectGroupPython] I_element041  label="I_element : 026"  # scripted group (container) (typed FeaturePython)
  n = 1
  ref = I_element
FEATURE [App::DocumentObjectGroupPython] G4_CESIUM_IODIDE  # scripted group (container) (typed FeaturePython)
  Dunit = g/cm3
  Dvalue = 4.51
  Group = -> [Cs_element014,I_element041]
  conduct = 2
  density = 1
  expand = 3
  formula = G4_CESIUM_IODIDE
  name = G4_CESIUM_IODIDE
  specific = 4
FEATURE [App::DocumentObjectGroupPython] C_element620  label="C_element : 404"  # scripted group (container) (typed FeaturePython)
  n = 6
  ref = C_element
FEATURE [App::DocumentObjectGroupPython] H_element577  label="H_element : 369"  # scripted group (container) (typed FeaturePython)
  n = 5
  ref = H_element
FEATURE [App::DocumentObjectGroupPython] Cl_element125  label="Cl_element : 062"  # scripted group (container) (typed FeaturePython)
  n = 1
  ref = Cl_element
FEATURE [App::DocumentObjectGroupPython] G4_CHLOROBENZENE  # scripted group (container) (typed FeaturePython)
  Dunit = g/cm3
  Dvalue = 1.1058
  Group = -> [C_element620,H_element577,Cl_element125]
  conduct = 2
  density = 1
  expand = 3
  formula = G4_CHLOROBENZENE
  name = G4_CHLOROBENZENE
  specific = 4
FEATURE [App::DocumentObjectGroupPython] C_element621  label="C_element : 405"  # scripted group (container) (typed FeaturePython)
  n = 1
  ref = C_element
FEATURE [App::DocumentObjectGroupPython] H_element578  label="H_element : 370"  # scripted group (container) (typed FeaturePython)
  n = 1
  ref = H_element
FEATURE [App::DocumentObjectGroupPython] Cl_element126  label="Cl_element : 063"  # scripted group (container) (typed FeaturePython)
  n = 3
  ref = Cl_element
FEATURE [App::DocumentObjectGroupPython] G4_CHLOROFORM  # scripted group (container) (typed FeaturePython)
  Dunit = g/cm3
  Dvalue = 1.4832
  Group = -> [C_element621,H_element578,Cl_element126]
  conduct = 2
  density = 1
  expand = 3
  formula = G4_CHLOROFORM
  name = G4_CHLOROFORM
  specific = 4
FEATURE [App::DocumentObjectGroupPython] H_element579  label="H_element : 0.259"  # scripted group (container) (typed FeaturePython)
  n = 0.01
FEATURE [App::DocumentObjectGroupPython] C_element622  label="C_element : 0.987"  # scripted group (container) (typed FeaturePython)
  n = 0.001
FEATURE [App::DocumentObjectGroupPython] O_element550  label="O_element : 0.980"  # scripted group (container) (typed FeaturePython)
  n = 0.529107
FEATURE [App::DocumentObjectGroupPython] Na_element085  label="Na_element : 0.146"  # scripted group (container) (typed FeaturePython)
  n = 0.016
FEATURE [App::DocumentObjectGroupPython] Mg_element047  label="Mg_element : 0.152"  # scripted group (container) (typed FeaturePython)
  n = 0.002
FEATURE [App::DocumentObjectGroupPython] Al_element018  label="Al_element : 0.039"  # scripted group (container) (typed FeaturePython)
  n = 0.033872
FEATURE [App::DocumentObjectGroupPython] Si_element030  label="Si_element : 0.391"  # scripted group (container) (typed FeaturePython)
  n = 0.337021
FEATURE [App::DocumentObjectGroupPython] K_element055  label="K_element : 0.046"  # scripted group (container) (typed FeaturePython)
  n = 0.013
FEATURE [App::DocumentObjectGroupPython] Ca_element066  label="Ca_element : 0.244"  # scripted group (container) (typed FeaturePython)
  n = 0.044
FEATURE [App::DocumentObjectGroupPython] Fe_element034  label="Fe_element : 0.022"  # scripted group (container) (typed FeaturePython)
  n = 0.014
FEATURE [App::DocumentObjectGroupPython] G4_CONCRETE  # scripted group (container) (typed FeaturePython)
  Dunit = g/cm3
  Dvalue = 2.3
  Group = -> [H_element579,C_element622,O_element550,Na_element085,Mg_element047,Al_element018,Si_element030,K_element055,Ca_element066,Fe_element034]
  conduct = 2
  density = 1
  expand = 3
  formula = G4_CONCRETE
  name = G4_CONCRETE
  specific = 4
FEATURE [App::DocumentObjectGroupPython] C_element623  label="C_element : 406"  # scripted group (container) (typed FeaturePython)
  n = 6
  ref = C_element
FEATURE [App::DocumentObjectGroupPython] H_element580  label="H_element : 371"  # scripted group (container) (typed FeaturePython)
  n = 12
  ref = H_element
FEATURE [App::DocumentObjectGroupPython] G4_CYCLOHEXANE  # scripted group (container) (typed FeaturePython)
  Dunit = g/cm3
  Dvalue = 0.779
  Group = -> [C_element623,H_element580]
  conduct = 2
  density = 1
  expand = 3
  formula = G4_CYCLOHEXANE
  name = G4_CYCLOHEXANE
  specific = 4
FEATURE [App::DocumentObjectGroupPython] C_element624  label="C_element : 407"  # scripted group (container) (typed FeaturePython)
  n = 6
  ref = C_element
FEATURE [App::DocumentObjectGroupPython] H_element581  label="H_element : 372"  # scripted group (container) (typed FeaturePython)
  n = 4
  ref = H_element
FEATURE [App::DocumentObjectGroupPython] Cl_element127  label="Cl_element : 064"  # scripted group (container) (typed FeaturePython)
  n = 2
  ref = Cl_element
FEATURE [App::DocumentObjectGroupPython] G4_1_2_DICHLOROBENZENE  label="G4_1.2-DICHLOROBENZENE"  # scripted group (container) (typed FeaturePython)
  Dunit = g/cm3
  Dvalue = 1.3048
  Group = -> [C_element624,H_element581,Cl_element127]
  conduct = 2
  density = 1
  expand = 3
  formula = G4_1.2-DICHLOROBENZENE
  name = G4_1.2-DICHLOROBENZENE
  specific = 4
FEATURE [App::DocumentObjectGroupPython] C_element625  label="C_element : 408"  # scripted group (container) (typed FeaturePython)
  n = 4
  ref = C_element
FEATURE [App::DocumentObjectGroupPython] H_element582  label="H_element : 373"  # scripted group (container) (typed FeaturePython)
  n = 8
  ref = H_element
FEATURE [App::DocumentObjectGroupPython] O_element551  label="O_element : 350"  # scripted group (container) (typed FeaturePython)
  n = 1
  ref = O_element
FEATURE [App::DocumentObjectGroupPython] Cl_element128  label="Cl_element : 065"  # scripted group (container) (typed FeaturePython)
  n = 2
  ref = Cl_element
FEATURE [App::DocumentObjectGroupPython] G4_DICHLORODIETHYL_ETHER  # scripted group (container) (typed FeaturePython)
  Dunit = g/cm3
  Dvalue = 1.2199
  Group = -> [C_element625,H_element582,O_element551,Cl_element128]
  conduct = 2
  density = 1
  expand = 3
  formula = G4_DICHLORODIETHYL_ETHER
  name = G4_DICHLORODIETHYL_ETHER
  specific = 4
FEATURE [App::DocumentObjectGroupPython] C_element626  label="C_element : 409"  # scripted group (container) (typed FeaturePython)
  n = 2
  ref = C_element
FEATURE [App::DocumentObjectGroupPython] H_element583  label="H_element : 374"  # scripted group (container) (typed FeaturePython)
  n = 4
  ref = H_element
FEATURE [App::DocumentObjectGroupPython] Cl_element129  label="Cl_element : 066"  # scripted group (container) (typed FeaturePython)
  n = 2
  ref = Cl_element
FEATURE [App::DocumentObjectGroupPython] G4_1_2_DICHLOROETHANE  label="G4_1.2-DICHLOROETHANE"  # scripted group (container) (typed FeaturePython)
  Dunit = g/cm3
  Dvalue = 1.2351
  Group = -> [C_element626,H_element583,Cl_element129]
  conduct = 2
  density = 1
  expand = 3
  formula = G4_1.2-DICHLOROETHANE
  name = G4_1.2-DICHLOROETHANE
  specific = 4
FEATURE [App::DocumentObjectGroupPython] C_element627  label="C_element : 410"  # scripted group (container) (typed FeaturePython)
  n = 4
  ref = C_element
FEATURE [App::DocumentObjectGroupPython] H_element584  label="H_element : 375"  # scripted group (container) (typed FeaturePython)
  n = 10
  ref = H_element
FEATURE [App::DocumentObjectGroupPython] O_element552  label="O_element : 351"  # scripted group (container) (typed FeaturePython)
  n = 1
  ref = O_element
FEATURE [App::DocumentObjectGroupPython] G4_DIETHYL_ETHER  # scripted group (container) (typed FeaturePython)
  Dunit = g/cm3
  Dvalue = 0.71378
  Group = -> [C_element627,H_element584,O_element552]
  conduct = 2
  density = 1
  expand = 3
  formula = G4_DIETHYL_ETHER
  name = G4_DIETHYL_ETHER
  specific = 4
FEATURE [App::DocumentObjectGroupPython] C_element628  label="C_element : 411"  # scripted group (container) (typed FeaturePython)
  n = 3
  ref = C_element
FEATURE [App::DocumentObjectGroupPython] H_element585  label="H_element : 376"  # scripted group (container) (typed FeaturePython)
  n = 7
  ref = H_element
FEATURE [App::DocumentObjectGroupPython] N_element287  label="N_element : 158"  # scripted group (container) (typed FeaturePython)
  n = 1
  ref = N_element
FEATURE [App::DocumentObjectGroupPython] O_element553  label="O_element : 352"  # scripted group (container) (typed FeaturePython)
  n = 1
  ref = O_element
FEATURE [App::DocumentObjectGroupPython] G4_N_N_DIMETHYL_FORMAMIDE  label="G4_N.N-DIMETHYL_FORMAMIDE"  # scripted group (container) (typed FeaturePython)
  Dunit = g/cm3
  Dvalue = 0.9487
  Group = -> [C_element628,H_element585,N_element287,O_element553]
  conduct = 2
  density = 1
  expand = 3
  formula = G4_N.N-DIMETHYL_FORMAMIDE
  name = G4_N.N-DIMETHYL_FORMAMIDE
  specific = 4
FEATURE [App::DocumentObjectGroupPython] C_element629  label="C_element : 412"  # scripted group (container) (typed FeaturePython)
  n = 2
  ref = C_element
FEATURE [App::DocumentObjectGroupPython] H_element586  label="H_element : 377"  # scripted group (container) (typed FeaturePython)
  n = 6
  ref = H_element
FEATURE [App::DocumentObjectGroupPython] O_element554  label="O_element : 353"  # scripted group (container) (typed FeaturePython)
  n = 1
  ref = O_element
FEATURE [App::DocumentObjectGroupPython] S_element101  label="S_element : 030"  # scripted group (container) (typed FeaturePython)
  n = 1
  ref = S_element
FEATURE [App::DocumentObjectGroupPython] G4_DIMETHYL_SULFOXIDE  # scripted group (container) (typed FeaturePython)
  Dunit = g/cm3
  Dvalue = 1.1014
  Group = -> [C_element629,H_element586,O_element554,S_element101]
  conduct = 2
  density = 1
  expand = 3
  formula = G4_DIMETHYL_SULFOXIDE
  name = G4_DIMETHYL_SULFOXIDE
  specific = 4
FEATURE [App::DocumentObjectGroupPython] C_element630  label="C_element : 413"  # scripted group (container) (typed FeaturePython)
  n = 2
  ref = C_element
FEATURE [App::DocumentObjectGroupPython] H_element587  label="H_element : 378"  # scripted group (container) (typed FeaturePython)
  n = 6
  ref = H_element
FEATURE [App::DocumentObjectGroupPython] G4_ETHANE  # scripted group (container) (typed FeaturePython)
  Dunit = g/cm3
  Dvalue = 0.00125324
  Group = -> [C_element630,H_element587]
  conduct = 2
  density = 1
  expand = 3
  formula = G4_ETHANE
  name = G4_ETHANE
  specific = 4
FEATURE [App::DocumentObjectGroupPython] C_element631  label="C_element : 414"  # scripted group (container) (typed FeaturePython)
  n = 2
  ref = C_element
FEATURE [App::DocumentObjectGroupPython] H_element588  label="H_element : 379"  # scripted group (container) (typed FeaturePython)
  n = 6
  ref = H_element
FEATURE [App::DocumentObjectGroupPython] O_element555  label="O_element : 354"  # scripted group (container) (typed FeaturePython)
  n = 1
  ref = O_element
FEATURE [App::DocumentObjectGroupPython] G4_ETHYL_ALCOHOL  # scripted group (container) (typed FeaturePython)
  Dunit = g/cm3
  Dvalue = 0.7893
  Group = -> [C_element631,H_element588,O_element555]
  conduct = 2
  density = 1
  expand = 3
  formula = G4_ETHYL_ALCOHOL
  name = G4_ETHYL_ALCOHOL
  specific = 4
FEATURE [App::DocumentObjectGroupPython] H_element589  label="H_element : 0.260"  # scripted group (container) (typed FeaturePython)
  n = 0.090027
FEATURE [App::DocumentObjectGroupPython] C_element632  label="C_element : 0.988"  # scripted group (container) (typed FeaturePython)
  n = 0.585182
FEATURE [App::DocumentObjectGroupPython] O_element556  label="O_element : 0.981"  # scripted group (container) (typed FeaturePython)
  n = 0.324791
FEATURE [App::DocumentObjectGroupPython] G4_ETHYL_CELLULOSE  # scripted group (container) (typed FeaturePython)
  Dunit = g/cm3
  Dvalue = 1.13
  Group = -> [H_element589,C_element632,O_element556]
  conduct = 2
  density = 1
  expand = 3
  formula = G4_ETHYL_CELLULOSE
  name = G4_ETHYL_CELLULOSE
  specific = 4
FEATURE [App::DocumentObjectGroupPython] C_element633  label="C_element : 415"  # scripted group (container) (typed FeaturePython)
  n = 2
  ref = C_element
FEATURE [App::DocumentObjectGroupPython] H_element590  label="H_element : 380"  # scripted group (container) (typed FeaturePython)
  n = 4
  ref = H_element
FEATURE [App::DocumentObjectGroupPython] G4_ETHYLENE  # scripted group (container) (typed FeaturePython)
  Dunit = g/cm3
  Dvalue = 0.00117497
  Group = -> [C_element633,H_element590]
  conduct = 2
  density = 1
  expand = 3
  formula = G4_ETHYLENE
  name = G4_ETHYLENE
  specific = 4
FEATURE [App::DocumentObjectGroupPython] H_element591  label="H_element : 0.261"  # scripted group (container) (typed FeaturePython)
  n = 0.096
FEATURE [App::DocumentObjectGroupPython] C_element634  label="C_element : 0.989"  # scripted group (container) (typed FeaturePython)
  n = 0.195
FEATURE [App::DocumentObjectGroupPython] N_element288  label="N_element : 0.838"  # scripted group (container) (typed FeaturePython)
  n = 0.057
FEATURE [App::DocumentObjectGroupPython] O_element557  label="O_element : 0.982"  # scripted group (container) (typed FeaturePython)
  n = 0.646
FEATURE [App::DocumentObjectGroupPython] Na_element086  label="Na_element : 0.147"  # scripted group (container) (typed FeaturePython)
  n = 0.001
FEATURE [App::DocumentObjectGroupPython] P_element081  label="P_element : 0.142"  # scripted group (container) (typed FeaturePython)
  n = 0.001
FEATURE [App::DocumentObjectGroupPython] S_element102  label="S_element : 0.071"  # scripted group (container) (typed FeaturePython)
  n = 0.003
FEATURE [App::DocumentObjectGroupPython] Cl_element130  label="Cl_element : 0.630"  # scripted group (container) (typed FeaturePython)
  n = 0.001
FEATURE [App::DocumentObjectGroupPython] G4_EYE_LENS_ICRP  # scripted group (container) (typed FeaturePython)
  Dunit = g/cm3
  Dvalue = 1.07
  Group = -> [H_element591,C_element634,N_element288,O_element557,Na_element086,P_element081,S_element102,Cl_element130]
  conduct = 2
  density = 1
  expand = 3
  formula = G4_EYE_LENS_ICRP
  name = G4_EYE_LENS_ICRP
  specific = 4
FEATURE [App::DocumentObjectGroupPython] Fe_element035  label="Fe_element : 017"  # scripted group (container) (typed FeaturePython)
  n = 2
  ref = Fe_element
FEATURE [App::DocumentObjectGroupPython] O_element558  label="O_element : 355"  # scripted group (container) (typed FeaturePython)
  n = 3
  ref = O_element
FEATURE [App::DocumentObjectGroupPython] G4_FERRIC_OXIDE  # scripted group (container) (typed FeaturePython)
  Dunit = g/cm3
  Dvalue = 5.2
  Group = -> [Fe_element035,O_element558]
  conduct = 2
  density = 1
  expand = 3
  formula = G4_FERRIC_OXIDE
  name = G4_FERRIC_OXIDE
  specific = 4
FEATURE [App::DocumentObjectGroupPython] Fe_element036  label="Fe_element : 018"  # scripted group (container) (typed FeaturePython)
  n = 1
  ref = Fe_element
FEATURE [App::DocumentObjectGroupPython] B_element031  label="B_element : 025"  # scripted group (container) (typed FeaturePython)
  n = 1
  ref = B_element
FEATURE [App::DocumentObjectGroupPython] G4_FERROBORIDE  # scripted group (container) (typed FeaturePython)
  Dunit = g/cm3
  Dvalue = 7.15
  Group = -> [Fe_element036,B_element031]
  conduct = 2
  density = 1
  expand = 3
  formula = G4_FERROBORIDE
  name = G4_FERROBORIDE
  specific = 4
FEATURE [App::DocumentObjectGroupPython] Fe_element037  label="Fe_element : 019"  # scripted group (container) (typed FeaturePython)
  n = 1
  ref = Fe_element
FEATURE [App::DocumentObjectGroupPython] O_element559  label="O_element : 356"  # scripted group (container) (typed FeaturePython)
  n = 1
  ref = O_element
FEATURE [App::DocumentObjectGroupPython] G4_FERROUS_OXIDE  # scripted group (container) (typed FeaturePython)
  Dunit = g/cm3
  Dvalue = 5.7
  Group = -> [Fe_element037,O_element559]
  conduct = 2
  density = 1
  expand = 3
  formula = G4_FERROUS_OXIDE
  name = G4_FERROUS_OXIDE
  specific = 4
FEATURE [App::DocumentObjectGroupPython] H_element592  label="H_element : 0.262"  # scripted group (container) (typed FeaturePython)
  n = 0.108259
FEATURE [App::DocumentObjectGroupPython] N_element289  label="N_element : 0.839"  # scripted group (container) (typed FeaturePython)
  n = 2.7e-05
FEATURE [App::DocumentObjectGroupPython] O_element560  label="O_element : 0.983"  # scripted group (container) (typed FeaturePython)
  n = 0.878636
FEATURE [App::DocumentObjectGroupPython] Na_element087  label="Na_element : 0.148"  # scripted group (container) (typed FeaturePython)
  n = 2.2e-05
FEATURE [App::DocumentObjectGroupPython] S_element103  label="S_element : 0.072"  # scripted group (container) (typed FeaturePython)
  n = 0.012968
FEATURE [App::DocumentObjectGroupPython] Cl_element131  label="Cl_element : 0.631"  # scripted group (container) (typed FeaturePython)
  n = 3.4e-05
FEATURE [App::DocumentObjectGroupPython] Fe_element038  label="Fe_element : 0.023"  # scripted group (container) (typed FeaturePython)
  n = 5.4e-05
FEATURE [App::DocumentObjectGroupPython] G4_FERROUS_SULFATE  # scripted group (container) (typed FeaturePython)
  Dunit = g/cm3
  Dvalue = 1.024
  Group = -> [H_element592,N_element289,O_element560,Na_element087,S_element103,Cl_element131,Fe_element038]
  conduct = 2
  density = 1
  expand = 3
  formula = G4_FERROUS_SULFATE
  name = G4_FERROUS_SULFATE
  specific = 4
FEATURE [App::DocumentObjectGroupPython] C_element635  label="C_element : 0.990"  # scripted group (container) (typed FeaturePython)
  n = 0.099335
FEATURE [App::DocumentObjectGroupPython] F_element083  label="F_element : 0.730"  # scripted group (container) (typed FeaturePython)
  n = 0.314247
FEATURE [App::DocumentObjectGroupPython] Cl_element132  label="Cl_element : 0.632"  # scripted group (container) (typed FeaturePython)
  n = 0.586418
FEATURE [App::DocumentObjectGroupPython] G4_FREON_12  label="G4_FREON-12"  # scripted group (container) (typed FeaturePython)
  Dunit = g/cm3
  Dvalue = 1.12
  Group = -> [C_element635,F_element083,Cl_element132]
  conduct = 2
  density = 1
  expand = 3
  formula = G4_FREON-12
  name = G4_FREON-12
  specific = 4
FEATURE [App::DocumentObjectGroupPython] C_element636  label="C_element : 0.991"  # scripted group (container) (typed FeaturePython)
  n = 0.057245
FEATURE [App::DocumentObjectGroupPython] F_element084  label="F_element : 0.731"  # scripted group (container) (typed FeaturePython)
  n = 0.181096
FEATURE [App::DocumentObjectGroupPython] Br_element029  label="Br_element : 0.769"  # scripted group (container) (typed FeaturePython)
  n = 0.761659
FEATURE [App::DocumentObjectGroupPython] G4_FREON_12B2  label="G4_FREON-12B2"  # scripted group (container) (typed FeaturePython)
  Dunit = g/cm3
  Dvalue = 1.8
  Group = -> [C_element636,F_element084,Br_element029]
  conduct = 2
  density = 1
  expand = 3
  formula = G4_FREON-12B2
  name = G4_FREON-12B2
  specific = 4
FEATURE [App::DocumentObjectGroupPython] C_element637  label="C_element : 0.992"  # scripted group (container) (typed FeaturePython)
  n = 0.114983
FEATURE [App::DocumentObjectGroupPython] F_element085  label="F_element : 0.732"  # scripted group (container) (typed FeaturePython)
  n = 0.545621
FEATURE [App::DocumentObjectGroupPython] Cl_element133  label="Cl_element : 0.633"  # scripted group (container) (typed FeaturePython)
  n = 0.339396
FEATURE [App::DocumentObjectGroupPython] G4_FREON_13  label="G4_FREON-13"  # scripted group (container) (typed FeaturePython)
  Dunit = g/cm3
  Dvalue = 0.95
  Group = -> [C_element637,F_element085,Cl_element133]
  conduct = 2
  density = 1
  expand = 3
  formula = G4_FREON-13
  name = G4_FREON-13
  specific = 4
FEATURE [App::DocumentObjectGroupPython] C_element638  label="C_element : 416"  # scripted group (container) (typed FeaturePython)
  n = 1
  ref = C_element
FEATURE [App::DocumentObjectGroupPython] F_element086  label="F_element : 040"  # scripted group (container) (typed FeaturePython)
  n = 3
  ref = F_element
FEATURE [App::DocumentObjectGroupPython] Br_element030  label="Br_element : 016"  # scripted group (container) (typed FeaturePython)
  n = 1
  ref = Br_element
FEATURE [App::DocumentObjectGroupPython] G4_FREON_13B1  label="G4_FREON-13B1"  # scripted group (container) (typed FeaturePython)
  Dunit = g/cm3
  Dvalue = 1.5
  Group = -> [C_element638,F_element086,Br_element030]
  conduct = 2
  density = 1
  expand = 3
  formula = G4_FREON-13B1
  name = G4_FREON-13B1
  specific = 4
FEATURE [App::DocumentObjectGroupPython] C_element639  label="C_element : 0.993"  # scripted group (container) (typed FeaturePython)
  n = 0.061309
FEATURE [App::DocumentObjectGroupPython] F_element087  label="F_element : 0.733"  # scripted group (container) (typed FeaturePython)
  n = 0.290924
FEATURE [App::DocumentObjectGroupPython] I_element042  label="I_element : 0.657"  # scripted group (container) (typed FeaturePython)
  n = 0.647767
FEATURE [App::DocumentObjectGroupPython] G4_FREON_13I1  label="G4_FREON-13I1"  # scripted group (container) (typed FeaturePython)
  Dunit = g/cm3
  Dvalue = 1.8
  Group = -> [C_element639,F_element087,I_element042]
  conduct = 2
  density = 1
  expand = 3
  formula = G4_FREON-13I1
  name = G4_FREON-13I1
  specific = 4
FEATURE [App::DocumentObjectGroupPython] Gd_element009  label="Gd_element : 007"  # scripted group (container) (typed FeaturePython)
  n = 2
  ref = Gd_element
FEATURE [App::DocumentObjectGroupPython] O_element561  label="O_element : 357"  # scripted group (container) (typed FeaturePython)
  n = 2
  ref = O_element
FEATURE [App::DocumentObjectGroupPython] S_element104  label="S_element : 031"  # scripted group (container) (typed FeaturePython)
  n = 1
  ref = S_element
FEATURE [App::DocumentObjectGroupPython] G4_GADOLINIUM_OXYSULFIDE  # scripted group (container) (typed FeaturePython)
  Dunit = g/cm3
  Dvalue = 7.44
  Group = -> [Gd_element009,O_element561,S_element104]
  conduct = 2
  density = 1
  expand = 3
  formula = G4_GADOLINIUM_OXYSULFIDE
  name = G4_GADOLINIUM_OXYSULFIDE
  specific = 4
FEATURE [App::DocumentObjectGroupPython] Ga_element009  label="Ga_element : 008"  # scripted group (container) (typed FeaturePython)
  n = 1
  ref = Ga_element
FEATURE [App::DocumentObjectGroupPython] As_element013  label="As_element : 008"  # scripted group (container) (typed FeaturePython)
  n = 1
  ref = As_element
FEATURE [App::DocumentObjectGroupPython] G4_GALLIUM_ARSENIDE  # scripted group (container) (typed FeaturePython)
  Dunit = g/cm3
  Dvalue = 5.31
  Group = -> [Ga_element009,As_element013]
  conduct = 2
  density = 1
  expand = 3
  formula = G4_GALLIUM_ARSENIDE
  name = G4_GALLIUM_ARSENIDE
  specific = 4
FEATURE [App::DocumentObjectGroupPython] H_element593  label="H_element : 0.263"  # scripted group (container) (typed FeaturePython)
  n = 0.08118
FEATURE [App::DocumentObjectGroupPython] C_element640  label="C_element : 0.994"  # scripted group (container) (typed FeaturePython)
  n = 0.41606
FEATURE [App::DocumentObjectGroupPython] N_element290  label="N_element : 0.840"  # scripted group (container) (typed FeaturePython)
  n = 0.11124
FEATURE [App::DocumentObjectGroupPython] O_element562  label="O_element : 0.984"  # scripted group (container) (typed FeaturePython)
  n = 0.38064
FEATURE [App::DocumentObjectGroupPython] S_element105  label="S_element : 0.073"  # scripted group (container) (typed FeaturePython)
  n = 0.01088
FEATURE [App::DocumentObjectGroupPython] G4_GEL_PHOTO_EMULSION  # scripted group (container) (typed FeaturePython)
  Dunit = g/cm3
  Dvalue = 1.2914
  Group = -> [H_element593,C_element640,N_element290,O_element562,S_element105]
  conduct = 2
  density = 1
  expand = 3
  formula = G4_GEL_PHOTO_EMULSION
  name = G4_GEL_PHOTO_EMULSION
  specific = 4
FEATURE [App::DocumentObjectGroupPython] B_element032  label="B_element : 0.043"  # scripted group (container) (typed FeaturePython)
  n = 0.0400639
FEATURE [App::DocumentObjectGroupPython] O_element563  label="O_element : 0.985"  # scripted group (container) (typed FeaturePython)
  n = 0.539561
FEATURE [App::DocumentObjectGroupPython] Na_element088  label="Na_element : 0.149"  # scripted group (container) (typed FeaturePython)
  n = 0.0281909
FEATURE [App::DocumentObjectGroupPython] Al_element019  label="Al_element : 0.040"  # scripted group (container) (typed FeaturePython)
  n = 0.011644
FEATURE [App::DocumentObjectGroupPython] Si_element031  label="Si_element : 0.392"  # scripted group (container) (typed FeaturePython)
  n = 0.377219
FEATURE [App::DocumentObjectGroupPython] K_element056  label="K_element : 0.047"  # scripted group (container) (typed FeaturePython)
  n = 0.00332099
FEATURE [App::DocumentObjectGroupPython] G4_Pyrex_Glass  # scripted group (container) (typed FeaturePython)
  Dunit = g/cm3
  Dvalue = 2.23
  Group = -> [B_element032,O_element563,Na_element088,Al_element019,Si_element031,K_element056]
  conduct = 2
  density = 1
  expand = 3
  formula = G4_Pyrex_Glass
  name = G4_Pyrex_Glass
  specific = 4
FEATURE [App::DocumentObjectGroupPython] O_element564  label="O_element : 0.986"  # scripted group (container) (typed FeaturePython)
  n = 0.156453
FEATURE [App::DocumentObjectGroupPython] Si_element032  label="Si_element : 0.393"  # scripted group (container) (typed FeaturePython)
  n = 0.080866
FEATURE [App::DocumentObjectGroupPython] Ti_element017  label="Ti_element : 0.019"  # scripted group (container) (typed FeaturePython)
  n = 0.008092
FEATURE [App::DocumentObjectGroupPython] As_element014  label="As_element : 0.006"  # scripted group (container) (typed FeaturePython)
  n = 0.002651
FEATURE [App::DocumentObjectGroupPython] Pb_element025  label="Pb_element : 0.933"  # scripted group (container) (typed FeaturePython)
  n = 0.751938
FEATURE [App::DocumentObjectGroupPython] G4_GLASS_LEAD  # scripted group (container) (typed FeaturePython)
  Dunit = g/cm3
  Dvalue = 6.22
  Group = -> [O_element564,Si_element032,Ti_element017,As_element014,Pb_element025]
  conduct = 2
  density = 1
  expand = 3
  formula = G4_GLASS_LEAD
  name = G4_GLASS_LEAD
  specific = 4
FEATURE [App::DocumentObjectGroupPython] O_element565  label="O_element : 0.987"  # scripted group (container) (typed FeaturePython)
  n = 0.4598
FEATURE [App::DocumentObjectGroupPython] Na_element089  label="Na_element : 0.150"  # scripted group (container) (typed FeaturePython)
  n = 0.0964411
FEATURE [App::DocumentObjectGroupPython] Si_element033  label="Si_element : 0.394"  # scripted group (container) (typed FeaturePython)
  n = 0.336553
FEATURE [App::DocumentObjectGroupPython] Ca_element067  label="Ca_element : 0.245"  # scripted group (container) (typed FeaturePython)
  n = 0.107205
FEATURE [App::DocumentObjectGroupPython] G4_GLASS_PLATE  # scripted group (container) (typed FeaturePython)
  Dunit = g/cm3
  Dvalue = 2.4
  Group = -> [O_element565,Na_element089,Si_element033,Ca_element067]
  conduct = 2
  density = 1
  expand = 3
  formula = G4_GLASS_PLATE
  name = G4_GLASS_PLATE
  specific = 4
FEATURE [App::DocumentObjectGroupPython] C_element641  label="C_element : 417"  # scripted group (container) (typed FeaturePython)
  n = 5
  ref = C_element
FEATURE [App::DocumentObjectGroupPython] H_element594  label="H_element : 381"  # scripted group (container) (typed FeaturePython)
  n = 10
  ref = H_element
FEATURE [App::DocumentObjectGroupPython] N_element291  label="N_element : 159"  # scripted group (container) (typed FeaturePython)
  n = 2
  ref = N_element
FEATURE [App::DocumentObjectGroupPython] O_element566  label="O_element : 358"  # scripted group (container) (typed FeaturePython)
  n = 3
  ref = O_element
FEATURE [App::DocumentObjectGroupPython] G4_GLUTAMINE  # scripted group (container) (typed FeaturePython)
  Dunit = g/cm3
  Dvalue = 1.46
  Group = -> [C_element641,H_element594,N_element291,O_element566]
  conduct = 2
  density = 1
  expand = 3
  formula = G4_GLUTAMINE
  name = G4_GLUTAMINE
  specific = 4
FEATURE [App::DocumentObjectGroupPython] C_element642  label="C_element : 418"  # scripted group (container) (typed FeaturePython)
  n = 3
  ref = C_element
FEATURE [App::DocumentObjectGroupPython] H_element595  label="H_element : 382"  # scripted group (container) (typed FeaturePython)
  n = 8
  ref = H_element
FEATURE [App::DocumentObjectGroupPython] O_element567  label="O_element : 359"  # scripted group (container) (typed FeaturePython)
  n = 3
  ref = O_element
FEATURE [App::DocumentObjectGroupPython] G4_GLYCEROL  # scripted group (container) (typed FeaturePython)
  Dunit = g/cm3
  Dvalue = 1.2613
  Group = -> [C_element642,H_element595,O_element567]
  conduct = 2
  density = 1
  expand = 3
  formula = G4_GLYCEROL
  name = G4_GLYCEROL
  specific = 4
FEATURE [App::DocumentObjectGroupPython] C_element643  label="C_element : 419"  # scripted group (container) (typed FeaturePython)
  n = 5
  ref = C_element
FEATURE [App::DocumentObjectGroupPython] H_element596  label="H_element : 383"  # scripted group (container) (typed FeaturePython)
  n = 5
  ref = H_element
FEATURE [App::DocumentObjectGroupPython] N_element292  label="N_element : 160"  # scripted group (container) (typed FeaturePython)
  n = 5
  ref = N_element
FEATURE [App::DocumentObjectGroupPython] O_element568  label="O_element : 360"  # scripted group (container) (typed FeaturePython)
  n = 1
  ref = O_element
FEATURE [App::DocumentObjectGroupPython] G4_GUANINE  # scripted group (container) (typed FeaturePython)
  Dunit = g/cm3
  Dvalue = 2.2
  Group = -> [C_element643,H_element596,N_element292,O_element568]
  conduct = 2
  density = 1
  expand = 3
  formula = G4_GUANINE
  name = G4_GUANINE
  specific = 4
FEATURE [App::DocumentObjectGroupPython] Ca_element068  label="Ca_element : 033"  # scripted group (container) (typed FeaturePython)
  n = 1
  ref = Ca_element
FEATURE [App::DocumentObjectGroupPython] S_element106  label="S_element : 032"  # scripted group (container) (typed FeaturePython)
  n = 1
  ref = S_element
FEATURE [App::DocumentObjectGroupPython] O_element569  label="O_element : 361"  # scripted group (container) (typed FeaturePython)
  n = 6
  ref = O_element
FEATURE [App::DocumentObjectGroupPython] H_element597  label="H_element : 384"  # scripted group (container) (typed FeaturePython)
  n = 4
  ref = H_element
FEATURE [App::DocumentObjectGroupPython] G4_GYPSUM  # scripted group (container) (typed FeaturePython)
  Dunit = g/cm3
  Dvalue = 2.32
  Group = -> [Ca_element068,S_element106,O_element569,H_element597]
  conduct = 2
  density = 1
  expand = 3
  formula = G4_GYPSUM
  name = G4_GYPSUM
  specific = 4
FEATURE [App::DocumentObjectGroupPython] C_element644  label="C_element : 420"  # scripted group (container) (typed FeaturePython)
  n = 7
  ref = C_element
FEATURE [App::DocumentObjectGroupPython] H_element598  label="H_element : 385"  # scripted group (container) (typed FeaturePython)
  n = 16
  ref = H_element
FEATURE [App::DocumentObjectGroupPython] G4_N_HEPTANE  label="G4_N-HEPTANE"  # scripted group (container) (typed FeaturePython)
  Dunit = g/cm3
  Dvalue = 0.68376
  Group = -> [C_element644,H_element598]
  conduct = 2
  density = 1
  expand = 3
  formula = G4_N-HEPTANE
  name = G4_N-HEPTANE
  specific = 4
FEATURE [App::DocumentObjectGroupPython] C_element645  label="C_element : 421"  # scripted group (container) (typed FeaturePython)
  n = 6
  ref = C_element
FEATURE [App::DocumentObjectGroupPython] H_element599  label="H_element : 386"  # scripted group (container) (typed FeaturePython)
  n = 14
  ref = H_element
FEATURE [App::DocumentObjectGroupPython] G4_N_HEXANE  label="G4_N-HEXANE"  # scripted group (container) (typed FeaturePython)
  Dunit = g/cm3
  Dvalue = 0.6603
  Group = -> [C_element645,H_element599]
  conduct = 2
  density = 1
  expand = 3
  formula = G4_N-HEXANE
  name = G4_N-HEXANE
  specific = 4
FEATURE [App::DocumentObjectGroupPython] C_element646  label="C_element : 422"  # scripted group (container) (typed FeaturePython)
  n = 22
  ref = C_element
FEATURE [App::DocumentObjectGroupPython] H_element600  label="H_element : 387"  # scripted group (container) (typed FeaturePython)
  n = 10
  ref = H_element
FEATURE [App::DocumentObjectGroupPython] N_element293  label="N_element : 161"  # scripted group (container) (typed FeaturePython)
  n = 2
  ref = N_element
FEATURE [App::DocumentObjectGroupPython] O_element570  label="O_element : 362"  # scripted group (container) (typed FeaturePython)
  n = 5
  ref = O_element
FEATURE [App::DocumentObjectGroupPython] G4_KAPTON  # scripted group (container) (typed FeaturePython)
  Dunit = g/cm3
  Dvalue = 1.42
  Group = -> [C_element646,H_element600,N_element293,O_element570]
  conduct = 2
  density = 1
  expand = 3
  formula = G4_KAPTON
  name = G4_KAPTON
  specific = 4
FEATURE [App::DocumentObjectGroupPython] La_element013  label="La_element : 011"  # scripted group (container) (typed FeaturePython)
  n = 1
  ref = La_element
FEATURE [App::DocumentObjectGroupPython] Br_element031  label="Br_element : 017"  # scripted group (container) (typed FeaturePython)
  n = 1
  ref = Br_element
FEATURE [App::DocumentObjectGroupPython] O_element571  label="O_element : 363"  # scripted group (container) (typed FeaturePython)
  n = 1
  ref = O_element
FEATURE [App::DocumentObjectGroupPython] G4_LANTHANUM_OXYBROMIDE  # scripted group (container) (typed FeaturePython)
  Dunit = g/cm3
  Dvalue = 6.28
  Group = -> [La_element013,Br_element031,O_element571]
  conduct = 2
  density = 1
  expand = 3
  formula = G4_LANTHANUM_OXYBROMIDE
  name = G4_LANTHANUM_OXYBROMIDE
  specific = 4
FEATURE [App::DocumentObjectGroupPython] La_element014  label="La_element : 012"  # scripted group (container) (typed FeaturePython)
  n = 2
  ref = La_element
FEATURE [App::DocumentObjectGroupPython] O_element572  label="O_element : 364"  # scripted group (container) (typed FeaturePython)
  n = 2
  ref = O_element
FEATURE [App::DocumentObjectGroupPython] S_element107  label="S_element : 033"  # scripted group (container) (typed FeaturePython)
  n = 1
  ref = S_element
FEATURE [App::DocumentObjectGroupPython] G4_LANTHANUM_OXYSULFIDE  # scripted group (container) (typed FeaturePython)
  Dunit = g/cm3
  Dvalue = 5.86
  Group = -> [La_element014,O_element572,S_element107]
  conduct = 2
  density = 1
  expand = 3
  formula = G4_LANTHANUM_OXYSULFIDE
  name = G4_LANTHANUM_OXYSULFIDE
  specific = 4
FEATURE [App::DocumentObjectGroupPython] O_element573  label="O_element : 0.988"  # scripted group (container) (typed FeaturePython)
  n = 0.071682
FEATURE [App::DocumentObjectGroupPython] Pb_element026  label="Pb_element : 0.934"  # scripted group (container) (typed FeaturePython)
  n = 0.928318
FEATURE [App::DocumentObjectGroupPython] G4_LEAD_OXIDE  # scripted group (container) (typed FeaturePython)
  Dunit = g/cm3
  Dvalue = 9.53
  Group = -> [O_element573,Pb_element026]
  conduct = 2
  density = 1
  expand = 3
  formula = G4_LEAD_OXIDE
  name = G4_LEAD_OXIDE
  specific = 4
FEATURE [App::DocumentObjectGroupPython] Li_element033  label="Li_element : 031"  # scripted group (container) (typed FeaturePython)
  n = 1
  ref = Li_element
FEATURE [App::DocumentObjectGroupPython] N_element294  label="N_element : 162"  # scripted group (container) (typed FeaturePython)
  n = 1
  ref = N_element
FEATURE [App::DocumentObjectGroupPython] H_element601  label="H_element : 388"  # scripted group (container) (typed FeaturePython)
  n = 2
  ref = H_element
FEATURE [App::DocumentObjectGroupPython] G4_LITHIUM_AMIDE  # scripted group (container) (typed FeaturePython)
  Dunit = g/cm3
  Dvalue = 1.178
  Group = -> [Li_element033,N_element294,H_element601]
  conduct = 2
  density = 1
  expand = 3
  formula = G4_LITHIUM_AMIDE
  name = G4_LITHIUM_AMIDE
  specific = 4
FEATURE [App::DocumentObjectGroupPython] Li_element034  label="Li_element : 032"  # scripted group (container) (typed FeaturePython)
  n = 2
  ref = Li_element
FEATURE [App::DocumentObjectGroupPython] C_element647  label="C_element : 423"  # scripted group (container) (typed FeaturePython)
  n = 1
  ref = C_element
FEATURE [App::DocumentObjectGroupPython] O_element574  label="O_element : 365"  # scripted group (container) (typed FeaturePython)
  n = 3
  ref = O_element
FEATURE [App::DocumentObjectGroupPython] G4_LITHIUM_CARBONATE  # scripted group (container) (typed FeaturePython)
  Dunit = g/cm3
  Dvalue = 2.11
  Group = -> [Li_element034,C_element647,O_element574]
  conduct = 2
  density = 1
  expand = 3
  formula = G4_LITHIUM_CARBONATE
  name = G4_LITHIUM_CARBONATE
  specific = 4
FEATURE [App::DocumentObjectGroupPython] Li_element035  label="Li_element : 033"  # scripted group (container) (typed FeaturePython)
  n = 1
  ref = Li_element
FEATURE [App::DocumentObjectGroupPython] F_element088  label="F_element : 041"  # scripted group (container) (typed FeaturePython)
  n = 1
  ref = F_element
FEATURE [App::DocumentObjectGroupPython] G4_LITHIUM_FLUORIDE  # scripted group (container) (typed FeaturePython)
  Dunit = g/cm3
  Dvalue = 2.635
  Group = -> [Li_element035,F_element088]
  conduct = 2
  density = 1
  expand = 3
  formula = G4_LITHIUM_FLUORIDE
  name = G4_LITHIUM_FLUORIDE
  specific = 4
FEATURE [App::DocumentObjectGroupPython] Li_element036  label="Li_element : 034"  # scripted group (container) (typed FeaturePython)
  n = 1
  ref = Li_element
FEATURE [App::DocumentObjectGroupPython] H_element602  label="H_element : 389"  # scripted group (container) (typed FeaturePython)
  n = 1
  ref = H_element
FEATURE [App::DocumentObjectGroupPython] G4_LITHIUM_HYDRIDE  # scripted group (container) (typed FeaturePython)
  Dunit = g/cm3
  Dvalue = 0.82
  Group = -> [Li_element036,H_element602]
  conduct = 2
  density = 1
  expand = 3
  formula = G4_LITHIUM_HYDRIDE
  name = G4_LITHIUM_HYDRIDE
  specific = 4
FEATURE [App::DocumentObjectGroupPython] Li_element037  label="Li_element : 035"  # scripted group (container) (typed FeaturePython)
  n = 1
  ref = Li_element
FEATURE [App::DocumentObjectGroupPython] I_element043  label="I_element : 027"  # scripted group (container) (typed FeaturePython)
  n = 1
  ref = I_element
FEATURE [App::DocumentObjectGroupPython] G4_LITHIUM_IODIDE  # scripted group (container) (typed FeaturePython)
  Dunit = g/cm3
  Dvalue = 3.494
  Group = -> [Li_element037,I_element043]
  conduct = 2
  density = 1
  expand = 3
  formula = G4_LITHIUM_IODIDE
  name = G4_LITHIUM_IODIDE
  specific = 4
FEATURE [App::DocumentObjectGroupPython] Li_element038  label="Li_element : 036"  # scripted group (container) (typed FeaturePython)
  n = 2
  ref = Li_element
FEATURE [App::DocumentObjectGroupPython] O_element575  label="O_element : 366"  # scripted group (container) (typed FeaturePython)
  n = 1
  ref = O_element
FEATURE [App::DocumentObjectGroupPython] G4_LITHIUM_OXIDE  # scripted group (container) (typed FeaturePython)
  Dunit = g/cm3
  Dvalue = 2.013
  Group = -> [Li_element038,O_element575]
  conduct = 2
  density = 1
  expand = 3
  formula = G4_LITHIUM_OXIDE
  name = G4_LITHIUM_OXIDE
  specific = 4
FEATURE [App::DocumentObjectGroupPython] Li_element039  label="Li_element : 037"  # scripted group (container) (typed FeaturePython)
  n = 2
  ref = Li_element
FEATURE [App::DocumentObjectGroupPython] B_element033  label="B_element : 026"  # scripted group (container) (typed FeaturePython)
  n = 4
  ref = B_element
FEATURE [App::DocumentObjectGroupPython] O_element576  label="O_element : 367"  # scripted group (container) (typed FeaturePython)
  n = 7
  ref = O_element
FEATURE [App::DocumentObjectGroupPython] G4_LITHIUM_TETRABORATE  # scripted group (container) (typed FeaturePython)
  Dunit = g/cm3
  Dvalue = 2.44
  Group = -> [Li_element039,B_element033,O_element576]
  conduct = 2
  density = 1
  expand = 3
  formula = G4_LITHIUM_TETRABORATE
  name = G4_LITHIUM_TETRABORATE
  specific = 4
FEATURE [App::DocumentObjectGroupPython] H_element603  label="H_element : 0.264"  # scripted group (container) (typed FeaturePython)
  n = 0.105
FEATURE [App::DocumentObjectGroupPython] C_element648  label="C_element : 0.995"  # scripted group (container) (typed FeaturePython)
  n = 0.083
FEATURE [App::DocumentObjectGroupPython] N_element295  label="N_element : 0.841"  # scripted group (container) (typed FeaturePython)
  n = 0.023
FEATURE [App::DocumentObjectGroupPython] O_element577  label="O_element : 0.989"  # scripted group (container) (typed FeaturePython)
  n = 0.779
FEATURE [App::DocumentObjectGroupPython] Na_element090  label="Na_element : 0.151"  # scripted group (container) (typed FeaturePython)
  n = 0.002
FEATURE [App::DocumentObjectGroupPython] P_element082  label="P_element : 0.143"  # scripted group (container) (typed FeaturePython)
  n = 0.001
FEATURE [App::DocumentObjectGroupPython] S_element108  label="S_element : 0.074"  # scripted group (container) (typed FeaturePython)
  n = 0.002
FEATURE [App::DocumentObjectGroupPython] Cl_element134  label="Cl_element : 0.634"  # scripted group (container) (typed FeaturePython)
  n = 0.003
FEATURE [App::DocumentObjectGroupPython] K_element057  label="K_element : 0.048"  # scripted group (container) (typed FeaturePython)
  n = 0.002
FEATURE [App::DocumentObjectGroupPython] G4_LUNG_ICRP  # scripted group (container) (typed FeaturePython)
  Dunit = g/cm3
  Dvalue = 1.04
  Group = -> [H_element603,C_element648,N_element295,O_element577,Na_element090,P_element082,S_element108,Cl_element134,K_element057]
  conduct = 2
  density = 1
  expand = 3
  formula = G4_LUNG_ICRP
  name = G4_LUNG_ICRP
  specific = 4
FEATURE [App::DocumentObjectGroupPython] H_element604  label="H_element : 0.265"  # scripted group (container) (typed FeaturePython)
  n = 0.114318
FEATURE [App::DocumentObjectGroupPython] C_element649  label="C_element : 0.996"  # scripted group (container) (typed FeaturePython)
  n = 0.655824
FEATURE [App::DocumentObjectGroupPython] O_element578  label="O_element : 0.990"  # scripted group (container) (typed FeaturePython)
  n = 0.0921831
FEATURE [App::DocumentObjectGroupPython] Mg_element048  label="Mg_element : 0.153"  # scripted group (container) (typed FeaturePython)
  n = 0.134792
FEATURE [App::DocumentObjectGroupPython] Ca_element069  label="Ca_element : 0.246"  # scripted group (container) (typed FeaturePython)
  n = 0.002883
FEATURE [App::DocumentObjectGroupPython] G4_M3_WAX  # scripted group (container) (typed FeaturePython)
  Dunit = g/cm3
  Dvalue = 1.05
  Group = -> [H_element604,C_element649,O_element578,Mg_element048,Ca_element069]
  conduct = 2
  density = 1
  expand = 3
  formula = G4_M3_WAX
  name = G4_M3_WAX
  specific = 4
FEATURE [App::DocumentObjectGroupPython] Mg_element049  label="Mg_element : 020"  # scripted group (container) (typed FeaturePython)
  n = 1
  ref = Mg_element
FEATURE [App::DocumentObjectGroupPython] C_element650  label="C_element : 424"  # scripted group (container) (typed FeaturePython)
  n = 1
  ref = C_element
FEATURE [App::DocumentObjectGroupPython] O_element579  label="O_element : 368"  # scripted group (container) (typed FeaturePython)
  n = 3
  ref = O_element
FEATURE [App::DocumentObjectGroupPython] G4_MAGNESIUM_CARBONATE  # scripted group (container) (typed FeaturePython)
  Dunit = g/cm3
  Dvalue = 2.958
  Group = -> [Mg_element049,C_element650,O_element579]
  conduct = 2
  density = 1
  expand = 3
  formula = G4_MAGNESIUM_CARBONATE
  name = G4_MAGNESIUM_CARBONATE
  specific = 4
FEATURE [App::DocumentObjectGroupPython] Mg_element050  label="Mg_element : 021"  # scripted group (container) (typed FeaturePython)
  n = 1
  ref = Mg_element
FEATURE [App::DocumentObjectGroupPython] F_element089  label="F_element : 042"  # scripted group (container) (typed FeaturePython)
  n = 2
  ref = F_element
FEATURE [App::DocumentObjectGroupPython] G4_MAGNESIUM_FLUORIDE  # scripted group (container) (typed FeaturePython)
  Dunit = g/cm3
  Dvalue = 3
  Group = -> [Mg_element050,F_element089]
  conduct = 2
  density = 1
  expand = 3
  formula = G4_MAGNESIUM_FLUORIDE
  name = G4_MAGNESIUM_FLUORIDE
  specific = 4
FEATURE [App::DocumentObjectGroupPython] Mg_element051  label="Mg_element : 022"  # scripted group (container) (typed FeaturePython)
  n = 1
  ref = Mg_element
FEATURE [App::DocumentObjectGroupPython] O_element580  label="O_element : 369"  # scripted group (container) (typed FeaturePython)
  n = 1
  ref = O_element
FEATURE [App::DocumentObjectGroupPython] G4_MAGNESIUM_OXIDE  # scripted group (container) (typed FeaturePython)
  Dunit = g/cm3
  Dvalue = 3.58
  Group = -> [Mg_element051,O_element580]
  conduct = 2
  density = 1
  expand = 3
  formula = G4_MAGNESIUM_OXIDE
  name = G4_MAGNESIUM_OXIDE
  specific = 4
FEATURE [App::DocumentObjectGroupPython] Mg_element052  label="Mg_element : 023"  # scripted group (container) (typed FeaturePython)
  n = 1
  ref = Mg_element
FEATURE [App::DocumentObjectGroupPython] B_element034  label="B_element : 027"  # scripted group (container) (typed FeaturePython)
  n = 4
  ref = B_element
FEATURE [App::DocumentObjectGroupPython] O_element581  label="O_element : 370"  # scripted group (container) (typed FeaturePython)
  n = 7
  ref = O_element
FEATURE [App::DocumentObjectGroupPython] G4_MAGNESIUM_TETRABORATE  # scripted group (container) (typed FeaturePython)
  Dunit = g/cm3
  Dvalue = 2.53
  Group = -> [Mg_element052,B_element034,O_element581]
  conduct = 2
  density = 1
  expand = 3
  formula = G4_MAGNESIUM_TETRABORATE
  name = G4_MAGNESIUM_TETRABORATE
  specific = 4
FEATURE [App::DocumentObjectGroupPython] Hg_element009  label="Hg_element : 008"  # scripted group (container) (typed FeaturePython)
  n = 1
  ref = Hg_element
FEATURE [App::DocumentObjectGroupPython] I_element044  label="I_element : 028"  # scripted group (container) (typed FeaturePython)
  n = 2
  ref = I_element
FEATURE [App::DocumentObjectGroupPython] G4_MERCURIC_IODIDE  # scripted group (container) (typed FeaturePython)
  Dunit = g/cm3
  Dvalue = 6.36
  Group = -> [Hg_element009,I_element044]
  conduct = 2
  density = 1
  expand = 3
  formula = G4_MERCURIC_IODIDE
  name = G4_MERCURIC_IODIDE
  specific = 4
FEATURE [App::DocumentObjectGroupPython] C_element651  label="C_element : 425"  # scripted group (container) (typed FeaturePython)
  n = 1
  ref = C_element
FEATURE [App::DocumentObjectGroupPython] H_element605  label="H_element : 390"  # scripted group (container) (typed FeaturePython)
  n = 4
  ref = H_element
FEATURE [App::DocumentObjectGroupPython] G4_METHANE  # scripted group (container) (typed FeaturePython)
  Dunit = g/cm3
  Dvalue = 0.000667151
  Group = -> [C_element651,H_element605]
  conduct = 2
  density = 1
  expand = 3
  formula = G4_METHANE
  name = G4_METHANE
  specific = 4
FEATURE [App::DocumentObjectGroupPython] C_element652  label="C_element : 426"  # scripted group (container) (typed FeaturePython)
  n = 1
  ref = C_element
FEATURE [App::DocumentObjectGroupPython] H_element606  label="H_element : 391"  # scripted group (container) (typed FeaturePython)
  n = 4
  ref = H_element
FEATURE [App::DocumentObjectGroupPython] O_element582  label="O_element : 371"  # scripted group (container) (typed FeaturePython)
  n = 1
  ref = O_element
FEATURE [App::DocumentObjectGroupPython] G4_METHANOL  # scripted group (container) (typed FeaturePython)
  Dunit = g/cm3
  Dvalue = 0.7914
  Group = -> [C_element652,H_element606,O_element582]
  conduct = 2
  density = 1
  expand = 3
  formula = G4_METHANOL
  name = G4_METHANOL
  specific = 4
FEATURE [App::DocumentObjectGroupPython] H_element607  label="H_element : 0.266"  # scripted group (container) (typed FeaturePython)
  n = 0.13404
FEATURE [App::DocumentObjectGroupPython] C_element653  label="C_element : 0.997"  # scripted group (container) (typed FeaturePython)
  n = 0.77796
FEATURE [App::DocumentObjectGroupPython] O_element583  label="O_element : 0.991"  # scripted group (container) (typed FeaturePython)
  n = 0.03502
FEATURE [App::DocumentObjectGroupPython] Mg_element053  label="Mg_element : 0.154"  # scripted group (container) (typed FeaturePython)
  n = 0.038594
FEATURE [App::DocumentObjectGroupPython] Ti_element018  label="Ti_element : 0.020"  # scripted group (container) (typed FeaturePython)
  n = 0.014386
FEATURE [App::DocumentObjectGroupPython] G4_MIX_D_WAX  # scripted group (container) (typed FeaturePython)
  Dunit = g/cm3
  Dvalue = 0.99
  Group = -> [H_element607,C_element653,O_element583,Mg_element053,Ti_element018]
  conduct = 2
  density = 1
  expand = 3
  formula = G4_MIX_D_WAX
  name = G4_MIX_D_WAX
  specific = 4
FEATURE [App::DocumentObjectGroupPython] H_element608  label="H_element : 0.267"  # scripted group (container) (typed FeaturePython)
  n = 0.081192
FEATURE [App::DocumentObjectGroupPython] C_element654  label="C_element : 0.998"  # scripted group (container) (typed FeaturePython)
  n = 0.583442
FEATURE [App::DocumentObjectGroupPython] N_element296  label="N_element : 0.842"  # scripted group (container) (typed FeaturePython)
  n = 0.017798
FEATURE [App::DocumentObjectGroupPython] O_element584  label="O_element : 0.992"  # scripted group (container) (typed FeaturePython)
  n = 0.186381
FEATURE [App::DocumentObjectGroupPython] Mg_element054  label="Mg_element : 0.155"  # scripted group (container) (typed FeaturePython)
  n = 0.130287
FEATURE [App::DocumentObjectGroupPython] Cl_element135  label="Cl_element : 0.635"  # scripted group (container) (typed FeaturePython)
  n = 0.0009
FEATURE [App::DocumentObjectGroupPython] G4_MS20_TISSUE  # scripted group (container) (typed FeaturePython)
  Dunit = g/cm3
  Dvalue = 1
  Group = -> [H_element608,C_element654,N_element296,O_element584,Mg_element054,Cl_element135]
  conduct = 2
  density = 1
  expand = 3
  formula = G4_MS20_TISSUE
  name = G4_MS20_TISSUE
  specific = 4
FEATURE [App::DocumentObjectGroupPython] H_element609  label="H_element : 0.268"  # scripted group (container) (typed FeaturePython)
  n = 0.102
FEATURE [App::DocumentObjectGroupPython] C_element655  label="C_element : 0.999"  # scripted group (container) (typed FeaturePython)
  n = 0.143
FEATURE [App::DocumentObjectGroupPython] N_element297  label="N_element : 0.843"  # scripted group (container) (typed FeaturePython)
  n = 0.034
FEATURE [App::DocumentObjectGroupPython] O_element585  label="O_element : 0.993"  # scripted group (container) (typed FeaturePython)
  n = 0.71
FEATURE [App::DocumentObjectGroupPython] Na_element091  label="Na_element : 0.152"  # scripted group (container) (typed FeaturePython)
  n = 0.001
FEATURE [App::DocumentObjectGroupPython] P_element083  label="P_element : 0.144"  # scripted group (container) (typed FeaturePython)
  n = 0.002
FEATURE [App::DocumentObjectGroupPython] S_element109  label="S_element : 0.075"  # scripted group (container) (typed FeaturePython)
  n = 0.003
FEATURE [App::DocumentObjectGroupPython] Cl_element136  label="Cl_element : 0.636"  # scripted group (container) (typed FeaturePython)
  n = 0.001
FEATURE [App::DocumentObjectGroupPython] K_element058  label="K_element : 0.049"  # scripted group (container) (typed FeaturePython)
  n = 0.004
FEATURE [App::DocumentObjectGroupPython] G4_MUSCLE_SKELETAL_ICRP  # scripted group (container) (typed FeaturePython)
  Dunit = g/cm3
  Dvalue = 1.05
  Group = -> [H_element609,C_element655,N_element297,O_element585,Na_element091,P_element083,S_element109,Cl_element136,K_element058]
  conduct = 2
  density = 1
  expand = 3
  formula = G4_MUSCLE_SKELETAL_ICRP
  name = G4_MUSCLE_SKELETAL_ICRP
  specific = 4
FEATURE [App::DocumentObjectGroupPython] H_element610  label="H_element : 0.269"  # scripted group (container) (typed FeaturePython)
  n = 0.102102
FEATURE [App::DocumentObjectGroupPython] C_element656  label="C_element : 0.1000"  # scripted group (container) (typed FeaturePython)
  n = 0.123123
FEATURE [App::DocumentObjectGroupPython] N_element298  label="N_element : 0.844"  # scripted group (container) (typed FeaturePython)
  n = 0.035035
FEATURE [App::DocumentObjectGroupPython] O_element586  label="O_element : 0.994"  # scripted group (container) (typed FeaturePython)
  n = 0.72973
FEATURE [App::DocumentObjectGroupPython] Na_element092  label="Na_element : 0.153"  # scripted group (container) (typed FeaturePython)
  n = 0.001001
FEATURE [App::DocumentObjectGroupPython] P_element084  label="P_element : 0.145"  # scripted group (container) (typed FeaturePython)
  n = 0.002002
FEATURE [App::DocumentObjectGroupPython] S_element110  label="S_element : 0.076"  # scripted group (container) (typed FeaturePython)
  n = 0.004004
FEATURE [App::DocumentObjectGroupPython] K_element059  label="K_element : 0.050"  # scripted group (container) (typed FeaturePython)
  n = 0.003003
FEATURE [App::DocumentObjectGroupPython] G4_MUSCLE_STRIATED_ICRU  # scripted group (container) (typed FeaturePython)
  Dunit = g/cm3
  Dvalue = 1.04
  Group = -> [H_element610,C_element656,N_element298,O_element586,Na_element092,P_element084,S_element110,K_element059]
  conduct = 2
  density = 1
  expand = 3
  formula = G4_MUSCLE_STRIATED_ICRU
  name = G4_MUSCLE_STRIATED_ICRU
  specific = 4
FEATURE [App::DocumentObjectGroupPython] H_element611  label="H_element : 0.270"  # scripted group (container) (typed FeaturePython)
  n = 0.0982341
FEATURE [App::DocumentObjectGroupPython] C_element657  label="C_element : 0.1001"  # scripted group (container) (typed FeaturePython)
  n = 0.156214
FEATURE [App::DocumentObjectGroupPython] N_element299  label="N_element : 0.845"  # scripted group (container) (typed FeaturePython)
  n = 0.035451
FEATURE [App::DocumentObjectGroupPython] O_element587  label="O_element : 0.995"  # scripted group (container) (typed FeaturePython)
  n = 0.710101
FEATURE [App::DocumentObjectGroupPython] G4_MUSCLE_WITH_SUCROSE  # scripted group (container) (typed FeaturePython)
  Dunit = g/cm3
  Dvalue = 1.11
  Group = -> [H_element611,C_element657,N_element299,O_element587]
  conduct = 2
  density = 1
  expand = 3
  formula = G4_MUSCLE_WITH_SUCROSE
  name = G4_MUSCLE_WITH_SUCROSE
  specific = 4
FEATURE [App::DocumentObjectGroupPython] H_element612  label="H_element : 0.271"  # scripted group (container) (typed FeaturePython)
  n = 0.101969
FEATURE [App::DocumentObjectGroupPython] C_element658  label="C_element : 0.1002"  # scripted group (container) (typed FeaturePython)
  n = 0.120058
FEATURE [App::DocumentObjectGroupPython] N_element300  label="N_element : 0.846"  # scripted group (container) (typed FeaturePython)
  n = 0.035451
FEATURE [App::DocumentObjectGroupPython] O_element588  label="O_element : 0.996"  # scripted group (container) (typed FeaturePython)
  n = 0.742522
FEATURE [App::DocumentObjectGroupPython] G4_MUSCLE_WITHOUT_SUCROSE  # scripted group (container) (typed FeaturePython)
  Dunit = g/cm3
  Dvalue = 1.07
  Group = -> [H_element612,C_element658,N_element300,O_element588]
  conduct = 2
  density = 1
  expand = 3
  formula = G4_MUSCLE_WITHOUT_SUCROSE
  name = G4_MUSCLE_WITHOUT_SUCROSE
  specific = 4
FEATURE [App::DocumentObjectGroupPython] C_element659  label="C_element : 427"  # scripted group (container) (typed FeaturePython)
  n = 10
  ref = C_element
FEATURE [App::DocumentObjectGroupPython] H_element613  label="H_element : 392"  # scripted group (container) (typed FeaturePython)
  n = 8
  ref = H_element
FEATURE [App::DocumentObjectGroupPython] G4_NAPHTHALENE  # scripted group (container) (typed FeaturePython)
  Dunit = g/cm3
  Dvalue = 1.145
  Group = -> [C_element659,H_element613]
  conduct = 2
  density = 1
  expand = 3
  formula = G4_NAPHTHALENE
  name = G4_NAPHTHALENE
  specific = 4
FEATURE [App::DocumentObjectGroupPython] C_element660  label="C_element : 428"  # scripted group (container) (typed FeaturePython)
  n = 6
  ref = C_element
FEATURE [App::DocumentObjectGroupPython] H_element614  label="H_element : 393"  # scripted group (container) (typed FeaturePython)
  n = 5
  ref = H_element
FEATURE [App::DocumentObjectGroupPython] N_element301  label="N_element : 163"  # scripted group (container) (typed FeaturePython)
  n = 1
  ref = N_element
FEATURE [App::DocumentObjectGroupPython] O_element589  label="O_element : 372"  # scripted group (container) (typed FeaturePython)
  n = 2
  ref = O_element
FEATURE [App::DocumentObjectGroupPython] G4_NITROBENZENE  # scripted group (container) (typed FeaturePython)
  Dunit = g/cm3
  Dvalue = 1.19867
  Group = -> [C_element660,H_element614,N_element301,O_element589]
  conduct = 2
  density = 1
  expand = 3
  formula = G4_NITROBENZENE
  name = G4_NITROBENZENE
  specific = 4
FEATURE [App::DocumentObjectGroupPython] N_element302  label="N_element : 164"  # scripted group (container) (typed FeaturePython)
  n = 2
  ref = N_element
FEATURE [App::DocumentObjectGroupPython] O_element590  label="O_element : 373"  # scripted group (container) (typed FeaturePython)
  n = 1
  ref = O_element
FEATURE [App::DocumentObjectGroupPython] G4_NITROUS_OXIDE  # scripted group (container) (typed FeaturePython)
  Dunit = g/cm3
  Dvalue = 0.00183094
  Group = -> [N_element302,O_element590]
  conduct = 2
  density = 1
  expand = 3
  formula = G4_NITROUS_OXIDE
  name = G4_NITROUS_OXIDE
  specific = 4
FEATURE [App::DocumentObjectGroupPython] H_element615  label="H_element : 0.272"  # scripted group (container) (typed FeaturePython)
  n = 0.103509
FEATURE [App::DocumentObjectGroupPython] C_element661  label="C_element : 0.1003"  # scripted group (container) (typed FeaturePython)
  n = 0.648416
FEATURE [App::DocumentObjectGroupPython] N_element303  label="N_element : 0.847"  # scripted group (container) (typed FeaturePython)
  n = 0.0995361
FEATURE [App::DocumentObjectGroupPython] O_element591  label="O_element : 0.997"  # scripted group (container) (typed FeaturePython)
  n = 0.148539
FEATURE [App::DocumentObjectGroupPython] G4_NYLON_8062  label="G4_NYLON-8062"  # scripted group (container) (typed FeaturePython)
  Dunit = g/cm3
  Dvalue = 1.08
  Group = -> [H_element615,C_element661,N_element303,O_element591]
  conduct = 2
  density = 1
  expand = 3
  formula = G4_NYLON-8062
  name = G4_NYLON-8062
  specific = 4
FEATURE [App::DocumentObjectGroupPython] C_element662  label="C_element : 429"  # scripted group (container) (typed FeaturePython)
  n = 6
  ref = C_element
FEATURE [App::DocumentObjectGroupPython] H_element616  label="H_element : 394"  # scripted group (container) (typed FeaturePython)
  n = 11
  ref = H_element
FEATURE [App::DocumentObjectGroupPython] N_element304  label="N_element : 165"  # scripted group (container) (typed FeaturePython)
  n = 1
  ref = N_element
FEATURE [App::DocumentObjectGroupPython] O_element592  label="O_element : 374"  # scripted group (container) (typed FeaturePython)
  n = 1
  ref = O_element
FEATURE [App::DocumentObjectGroupPython] G4_NYLON_6_6  label="G4_NYLON-6-6"  # scripted group (container) (typed FeaturePython)
  Dunit = g/cm3
  Dvalue = 1.14
  Group = -> [C_element662,H_element616,N_element304,O_element592]
  conduct = 2
  density = 1
  expand = 3
  formula = G4_NYLON-6-6
  name = G4_NYLON-6-6
  specific = 4
FEATURE [App::DocumentObjectGroupPython] H_element617  label="H_element : 0.273"  # scripted group (container) (typed FeaturePython)
  n = 0.107062
FEATURE [App::DocumentObjectGroupPython] C_element663  label="C_element : 0.1004"  # scripted group (container) (typed FeaturePython)
  n = 0.680449
FEATURE [App::DocumentObjectGroupPython] N_element305  label="N_element : 0.848"  # scripted group (container) (typed FeaturePython)
  n = 0.099189
FEATURE [App::DocumentObjectGroupPython] O_element593  label="O_element : 0.998"  # scripted group (container) (typed FeaturePython)
  n = 0.1133
FEATURE [App::DocumentObjectGroupPython] G4_NYLON_6_10  label="G4_NYLON-6-10"  # scripted group (container) (typed FeaturePython)
  Dunit = g/cm3
  Dvalue = 1.14
  Group = -> [H_element617,C_element663,N_element305,O_element593]
  conduct = 2
  density = 1
  expand = 3
  formula = G4_NYLON-6-10
  name = G4_NYLON-6-10
  specific = 4
FEATURE [App::DocumentObjectGroupPython] H_element618  label="H_element : 0.274"  # scripted group (container) (typed FeaturePython)
  n = 0.115476
FEATURE [App::DocumentObjectGroupPython] C_element664  label="C_element : 0.1005"  # scripted group (container) (typed FeaturePython)
  n = 0.720818
FEATURE [App::DocumentObjectGroupPython] N_element306  label="N_element : 0.849"  # scripted group (container) (typed FeaturePython)
  n = 0.0764169
FEATURE [App::DocumentObjectGroupPython] O_element594  label="O_element : 0.999"  # scripted group (container) (typed FeaturePython)
  n = 0.0872889
FEATURE [App::DocumentObjectGroupPython] G4_NYLON_11_RILSAN  label="G4_NYLON-11_RILSAN"  # scripted group (container) (typed FeaturePython)
  Dunit = g/cm3
  Dvalue = 1.425
  Group = -> [H_element618,C_element664,N_element306,O_element594]
  conduct = 2
  density = 1
  expand = 3
  formula = G4_NYLON-11_RILSAN
  name = G4_NYLON-11_RILSAN
  specific = 4
FEATURE [App::DocumentObjectGroupPython] C_element665  label="C_element : 430"  # scripted group (container) (typed FeaturePython)
  n = 8
  ref = C_element
FEATURE [App::DocumentObjectGroupPython] H_element619  label="H_element : 395"  # scripted group (container) (typed FeaturePython)
  n = 18
  ref = H_element
FEATURE [App::DocumentObjectGroupPython] G4_OCTANE  # scripted group (container) (typed FeaturePython)
  Dunit = g/cm3
  Dvalue = 0.7026
  Group = -> [C_element665,H_element619]
  conduct = 2
  density = 1
  expand = 3
  formula = G4_OCTANE
  name = G4_OCTANE
  specific = 4
FEATURE [App::DocumentObjectGroupPython] C_element666  label="C_element : 431"  # scripted group (container) (typed FeaturePython)
  n = 25
  ref = C_element
FEATURE [App::DocumentObjectGroupPython] H_element620  label="H_element : 396"  # scripted group (container) (typed FeaturePython)
  n = 52
  ref = H_element
FEATURE [App::DocumentObjectGroupPython] G4_PARAFFIN  # scripted group (container) (typed FeaturePython)
  Dunit = g/cm3
  Dvalue = 0.93
  Group = -> [C_element666,H_element620]
  conduct = 2
  density = 1
  expand = 3
  formula = G4_PARAFFIN
  name = G4_PARAFFIN
  specific = 4
FEATURE [App::DocumentObjectGroupPython] C_element667  label="C_element : 432"  # scripted group (container) (typed FeaturePython)
  n = 5
  ref = C_element
FEATURE [App::DocumentObjectGroupPython] H_element621  label="H_element : 397"  # scripted group (container) (typed FeaturePython)
  n = 12
  ref = H_element
FEATURE [App::DocumentObjectGroupPython] G4_N_PENTANE  label="G4_N-PENTANE"  # scripted group (container) (typed FeaturePython)
  Dunit = g/cm3
  Dvalue = 0.6262
  Group = -> [C_element667,H_element621]
  conduct = 2
  density = 1
  expand = 3
  formula = G4_N-PENTANE
  name = G4_N-PENTANE
  specific = 4
FEATURE [App::DocumentObjectGroupPython] H_element622  label="H_element : 0.275"  # scripted group (container) (typed FeaturePython)
  n = 0.0141
FEATURE [App::DocumentObjectGroupPython] C_element668  label="C_element : 0.1006"  # scripted group (container) (typed FeaturePython)
  n = 0.072261
FEATURE [App::DocumentObjectGroupPython] N_element307  label="N_element : 0.850"  # scripted group (container) (typed FeaturePython)
  n = 0.01932
FEATURE [App::DocumentObjectGroupPython] O_element595  label="O_element : 0.1000"  # scripted group (container) (typed FeaturePython)
  n = 0.066101
FEATURE [App::DocumentObjectGroupPython] S_element111  label="S_element : 0.077"  # scripted group (container) (typed FeaturePython)
  n = 0.00189
FEATURE [App::DocumentObjectGroupPython] Br_element032  label="Br_element : 0.770"  # scripted group (container) (typed FeaturePython)
  n = 0.349103
FEATURE [App::DocumentObjectGroupPython] Ag_element025  label="Ag_element : 0.579"  # scripted group (container) (typed FeaturePython)
  n = 0.474105
FEATURE [App::DocumentObjectGroupPython] I_element045  label="I_element : 0.658"  # scripted group (container) (typed FeaturePython)
  n = 0.00312
FEATURE [App::DocumentObjectGroupPython] G4_PHOTO_EMULSION  # scripted group (container) (typed FeaturePython)
  Dunit = g/cm3
  Dvalue = 3.815
  Group = -> [H_element622,C_element668,N_element307,O_element595,S_element111,Br_element032,Ag_element025,I_element045]
  conduct = 2
  density = 1
  expand = 3
  formula = G4_PHOTO_EMULSION
  name = G4_PHOTO_EMULSION
  specific = 4
FEATURE [App::DocumentObjectGroupPython] C_element669  label="C_element : 433"  # scripted group (container) (typed FeaturePython)
  n = 9
  ref = C_element
FEATURE [App::DocumentObjectGroupPython] H_element623  label="H_element : 398"  # scripted group (container) (typed FeaturePython)
  n = 10
  ref = H_element
FEATURE [App::DocumentObjectGroupPython] G4_PLASTIC_SC_VINYLTOLUENE  # scripted group (container) (typed FeaturePython)
  Dunit = g/cm3
  Dvalue = 1.032
  Group = -> [C_element669,H_element623]
  conduct = 2
  density = 1
  expand = 3
  formula = G4_PLASTIC_SC_VINYLTOLUENE
  name = G4_PLASTIC_SC_VINYLTOLUENE
  specific = 4
FEATURE [App::DocumentObjectGroupPython] Pu_element009  label="Pu_element : 008"  # scripted group (container) (typed FeaturePython)
  n = 1
  ref = Pu_element
FEATURE [App::DocumentObjectGroupPython] O_element596  label="O_element : 375"  # scripted group (container) (typed FeaturePython)
  n = 2
  ref = O_element
FEATURE [App::DocumentObjectGroupPython] G4_PLUTONIUM_DIOXIDE  # scripted group (container) (typed FeaturePython)
  Dunit = g/cm3
  Dvalue = 11.46
  Group = -> [Pu_element009,O_element596]
  conduct = 2
  density = 1
  expand = 3
  formula = G4_PLUTONIUM_DIOXIDE
  name = G4_PLUTONIUM_DIOXIDE
  specific = 4
FEATURE [App::DocumentObjectGroupPython] C_element670  label="C_element : 434"  # scripted group (container) (typed FeaturePython)
  n = 3
  ref = C_element
FEATURE [App::DocumentObjectGroupPython] H_element624  label="H_element : 399"  # scripted group (container) (typed FeaturePython)
  n = 3
  ref = H_element
FEATURE [App::DocumentObjectGroupPython] N_element308  label="N_element : 166"  # scripted group (container) (typed FeaturePython)
  n = 1
  ref = N_element
FEATURE [App::DocumentObjectGroupPython] G4_POLYACRYLONITRILE  # scripted group (container) (typed FeaturePython)
  Dunit = g/cm3
  Dvalue = 1.17
  Group = -> [C_element670,H_element624,N_element308]
  conduct = 2
  density = 1
  expand = 3
  formula = G4_POLYACRYLONITRILE
  name = G4_POLYACRYLONITRILE
  specific = 4
FEATURE [App::DocumentObjectGroupPython] C_element671  label="C_element : 435"  # scripted group (container) (typed FeaturePython)
  n = 16
  ref = C_element
FEATURE [App::DocumentObjectGroupPython] H_element625  label="H_element : 400"  # scripted group (container) (typed FeaturePython)
  n = 14
  ref = H_element
FEATURE [App::DocumentObjectGroupPython] O_element597  label="O_element : 376"  # scripted group (container) (typed FeaturePython)
  n = 3
  ref = O_element
FEATURE [App::DocumentObjectGroupPython] G4_POLYCARBONATE  # scripted group (container) (typed FeaturePython)
  Dunit = g/cm3
  Dvalue = 1.2
  Group = -> [C_element671,H_element625,O_element597]
  conduct = 2
  density = 1
  expand = 3
  formula = G4_POLYCARBONATE
  name = G4_POLYCARBONATE
  specific = 4
FEATURE [App::DocumentObjectGroupPython] C_element672  label="C_element : 436"  # scripted group (container) (typed FeaturePython)
  n = 8
  ref = C_element
FEATURE [App::DocumentObjectGroupPython] H_element626  label="H_element : 401"  # scripted group (container) (typed FeaturePython)
  n = 7
  ref = H_element
FEATURE [App::DocumentObjectGroupPython] Cl_element137  label="Cl_element : 067"  # scripted group (container) (typed FeaturePython)
  n = 1
  ref = Cl_element
FEATURE [App::DocumentObjectGroupPython] G4_POLYCHLOROSTYRENE  # scripted group (container) (typed FeaturePython)
  Dunit = g/cm3
  Dvalue = 1.3
  Group = -> [C_element672,H_element626,Cl_element137]
  conduct = 2
  density = 1
  expand = 3
  formula = G4_POLYCHLOROSTYRENE
  name = G4_POLYCHLOROSTYRENE
  specific = 4
FEATURE [App::DocumentObjectGroupPython] C_element673  label="C_element : 437"  # scripted group (container) (typed FeaturePython)
  n = 1
  ref = C_element
FEATURE [App::DocumentObjectGroupPython] H_element627  label="H_element : 402"  # scripted group (container) (typed FeaturePython)
  n = 2
  ref = H_element
FEATURE [App::DocumentObjectGroupPython] G4_POLYETHYLENE  # scripted group (container) (typed FeaturePython)
  Dunit = g/cm3
  Dvalue = 0.94
  Group = -> [C_element673,H_element627]
  conduct = 2
  density = 1
  expand = 3
  formula = G4_POLYETHYLENE
  name = G4_POLYETHYLENE
  specific = 4
FEATURE [App::DocumentObjectGroupPython] C_element674  label="C_element : 438"  # scripted group (container) (typed FeaturePython)
  n = 10
  ref = C_element
FEATURE [App::DocumentObjectGroupPython] H_element628  label="H_element : 403"  # scripted group (container) (typed FeaturePython)
  n = 8
  ref = H_element
FEATURE [App::DocumentObjectGroupPython] O_element598  label="O_element : 377"  # scripted group (container) (typed FeaturePython)
  n = 4
  ref = O_element
FEATURE [App::DocumentObjectGroupPython] G4_MYLAR  # scripted group (container) (typed FeaturePython)
  Dunit = g/cm3
  Dvalue = 1.4
  Group = -> [C_element674,H_element628,O_element598]
  conduct = 2
  density = 1
  expand = 3
  formula = G4_MYLAR
  name = G4_MYLAR
  specific = 4
FEATURE [App::DocumentObjectGroupPython] C_element675  label="C_element : 439"  # scripted group (container) (typed FeaturePython)
  n = 5
  ref = C_element
FEATURE [App::DocumentObjectGroupPython] H_element629  label="H_element : 404"  # scripted group (container) (typed FeaturePython)
  n = 8
  ref = H_element
FEATURE [App::DocumentObjectGroupPython] O_element599  label="O_element : 378"  # scripted group (container) (typed FeaturePython)
  n = 2
  ref = O_element
FEATURE [App::DocumentObjectGroupPython] G4_PLEXIGLASS  # scripted group (container) (typed FeaturePython)
  Dunit = g/cm3
  Dvalue = 1.19
  Group = -> [C_element675,H_element629,O_element599]
  conduct = 2
  density = 1
  expand = 3
  formula = G4_PLEXIGLASS
  name = G4_PLEXIGLASS
  specific = 4
FEATURE [App::DocumentObjectGroupPython] C_element676  label="C_element : 440"  # scripted group (container) (typed FeaturePython)
  n = 1
  ref = C_element
FEATURE [App::DocumentObjectGroupPython] H_element630  label="H_element : 405"  # scripted group (container) (typed FeaturePython)
  n = 2
  ref = H_element
FEATURE [App::DocumentObjectGroupPython] O_element600  label="O_element : 379"  # scripted group (container) (typed FeaturePython)
  n = 1
  ref = O_element
FEATURE [App::DocumentObjectGroupPython] G4_POLYOXYMETHYLENE  # scripted group (container) (typed FeaturePython)
  Dunit = g/cm3
  Dvalue = 1.425
  Group = -> [C_element676,H_element630,O_element600]
  conduct = 2
  density = 1
  expand = 3
  formula = G4_POLYOXYMETHYLENE
  name = G4_POLYOXYMETHYLENE
  specific = 4
FEATURE [App::DocumentObjectGroupPython] C_element677  label="C_element : 441"  # scripted group (container) (typed FeaturePython)
  n = 2
  ref = C_element
FEATURE [App::DocumentObjectGroupPython] H_element631  label="H_element : 406"  # scripted group (container) (typed FeaturePython)
  n = 4
  ref = H_element
FEATURE [App::DocumentObjectGroupPython] G4_POLYPROPYLENE  # scripted group (container) (typed FeaturePython)
  Dunit = g/cm3
  Dvalue = 0.9
  Group = -> [C_element677,H_element631]
  conduct = 2
  density = 1
  expand = 3
  formula = G4_POLYPROPYLENE
  name = G4_POLYPROPYLENE
  specific = 4
FEATURE [App::DocumentObjectGroupPython] C_element678  label="C_element : 442"  # scripted group (container) (typed FeaturePython)
  n = 8
  ref = C_element
FEATURE [App::DocumentObjectGroupPython] H_element632  label="H_element : 407"  # scripted group (container) (typed FeaturePython)
  n = 8
  ref = H_element
FEATURE [App::DocumentObjectGroupPython] G4_POLYSTYRENE  # scripted group (container) (typed FeaturePython)
  Dunit = g/cm3
  Dvalue = 1.06
  Group = -> [C_element678,H_element632]
  conduct = 2
  density = 1
  expand = 3
  formula = G4_POLYSTYRENE
  name = G4_POLYSTYRENE
  specific = 4
FEATURE [App::DocumentObjectGroupPython] C_element679  label="C_element : 443"  # scripted group (container) (typed FeaturePython)
  n = 2
  ref = C_element
FEATURE [App::DocumentObjectGroupPython] F_element090  label="F_element : 043"  # scripted group (container) (typed FeaturePython)
  n = 4
  ref = F_element
FEATURE [App::DocumentObjectGroupPython] G4_TEFLON  # scripted group (container) (typed FeaturePython)
  Dunit = g/cm3
  Dvalue = 2.2
  Group = -> [C_element679,F_element090]
  conduct = 2
  density = 1
  expand = 3
  formula = G4_TEFLON
  name = G4_TEFLON
  specific = 4
FEATURE [App::DocumentObjectGroupPython] C_element680  label="C_element : 444"  # scripted group (container) (typed FeaturePython)
  n = 2
  ref = C_element
FEATURE [App::DocumentObjectGroupPython] F_element091  label="F_element : 044"  # scripted group (container) (typed FeaturePython)
  n = 3
  ref = F_element
FEATURE [App::DocumentObjectGroupPython] Cl_element138  label="Cl_element : 068"  # scripted group (container) (typed FeaturePython)
  n = 1
  ref = Cl_element
FEATURE [App::DocumentObjectGroupPython] G4_POLYTRIFLUOROCHLOROETHYLENE  # scripted group (container) (typed FeaturePython)
  Dunit = g/cm3
  Dvalue = 2.1
  Group = -> [C_element680,F_element091,Cl_element138]
  conduct = 2
  density = 1
  expand = 3
  formula = G4_POLYTRIFLUOROCHLOROETHYLENE
  name = G4_POLYTRIFLUOROCHLOROETHYLENE
  specific = 4
FEATURE [App::DocumentObjectGroupPython] C_element681  label="C_element : 445"  # scripted group (container) (typed FeaturePython)
  n = 4
  ref = C_element
FEATURE [App::DocumentObjectGroupPython] H_element633  label="H_element : 408"  # scripted group (container) (typed FeaturePython)
  n = 6
  ref = H_element
FEATURE [App::DocumentObjectGroupPython] O_element601  label="O_element : 380"  # scripted group (container) (typed FeaturePython)
  n = 2
  ref = O_element
FEATURE [App::DocumentObjectGroupPython] G4_POLYVINYL_ACETATE  # scripted group (container) (typed FeaturePython)
  Dunit = g/cm3
  Dvalue = 1.19
  Group = -> [C_element681,H_element633,O_element601]
  conduct = 2
  density = 1
  expand = 3
  formula = G4_POLYVINYL_ACETATE
  name = G4_POLYVINYL_ACETATE
  specific = 4
FEATURE [App::DocumentObjectGroupPython] C_element682  label="C_element : 446"  # scripted group (container) (typed FeaturePython)
  n = 2
  ref = C_element
FEATURE [App::DocumentObjectGroupPython] H_element634  label="H_element : 409"  # scripted group (container) (typed FeaturePython)
  n = 4
  ref = H_element
FEATURE [App::DocumentObjectGroupPython] O_element602  label="O_element : 381"  # scripted group (container) (typed FeaturePython)
  n = 1
  ref = O_element
FEATURE [App::DocumentObjectGroupPython] G4_POLYVINYL_ALCOHOL  # scripted group (container) (typed FeaturePython)
  Dunit = g/cm3
  Dvalue = 1.3
  Group = -> [C_element682,H_element634,O_element602]
  conduct = 2
  density = 1
  expand = 3
  formula = G4_POLYVINYL_ALCOHOL
  name = G4_POLYVINYL_ALCOHOL
  specific = 4
FEATURE [App::DocumentObjectGroupPython] C_element683  label="C_element : 447"  # scripted group (container) (typed FeaturePython)
  n = 8
  ref = C_element
FEATURE [App::DocumentObjectGroupPython] H_element635  label="H_element : 410"  # scripted group (container) (typed FeaturePython)
  n = 14
  ref = H_element
FEATURE [App::DocumentObjectGroupPython] O_element603  label="O_element : 382"  # scripted group (container) (typed FeaturePython)
  n = 2
  ref = O_element
FEATURE [App::DocumentObjectGroupPython] G4_POLYVINYL_BUTYRAL  # scripted group (container) (typed FeaturePython)
  Dunit = g/cm3
  Dvalue = 1.12
  Group = -> [C_element683,H_element635,O_element603]
  conduct = 2
  density = 1
  expand = 3
  formula = G4_POLYVINYL_BUTYRAL
  name = G4_POLYVINYL_BUTYRAL
  specific = 4
FEATURE [App::DocumentObjectGroupPython] C_element684  label="C_element : 448"  # scripted group (container) (typed FeaturePython)
  n = 2
  ref = C_element
FEATURE [App::DocumentObjectGroupPython] H_element636  label="H_element : 411"  # scripted group (container) (typed FeaturePython)
  n = 3
  ref = H_element
FEATURE [App::DocumentObjectGroupPython] Cl_element139  label="Cl_element : 069"  # scripted group (container) (typed FeaturePython)
  n = 1
  ref = Cl_element
FEATURE [App::DocumentObjectGroupPython] G4_POLYVINYL_CHLORIDE  # scripted group (container) (typed FeaturePython)
  Dunit = g/cm3
  Dvalue = 1.3
  Group = -> [C_element684,H_element636,Cl_element139]
  conduct = 2
  density = 1
  expand = 3
  formula = G4_POLYVINYL_CHLORIDE
  name = G4_POLYVINYL_CHLORIDE
  specific = 4
FEATURE [App::DocumentObjectGroupPython] C_element685  label="C_element : 449"  # scripted group (container) (typed FeaturePython)
  n = 2
  ref = C_element
FEATURE [App::DocumentObjectGroupPython] H_element637  label="H_element : 412"  # scripted group (container) (typed FeaturePython)
  n = 2
  ref = H_element
FEATURE [App::DocumentObjectGroupPython] Cl_element140  label="Cl_element : 070"  # scripted group (container) (typed FeaturePython)
  n = 2
  ref = Cl_element
FEATURE [App::DocumentObjectGroupPython] G4_POLYVINYLIDENE_CHLORIDE  # scripted group (container) (typed FeaturePython)
  Dunit = g/cm3
  Dvalue = 1.7
  Group = -> [C_element685,H_element637,Cl_element140]
  conduct = 2
  density = 1
  expand = 3
  formula = G4_POLYVINYLIDENE_CHLORIDE
  name = G4_POLYVINYLIDENE_CHLORIDE
  specific = 4
FEATURE [App::DocumentObjectGroupPython] C_element686  label="C_element : 450"  # scripted group (container) (typed FeaturePython)
  n = 2
  ref = C_element
FEATURE [App::DocumentObjectGroupPython] H_element638  label="H_element : 413"  # scripted group (container) (typed FeaturePython)
  n = 2
  ref = H_element
FEATURE [App::DocumentObjectGroupPython] F_element092  label="F_element : 045"  # scripted group (container) (typed FeaturePython)
  n = 2
  ref = F_element
FEATURE [App::DocumentObjectGroupPython] G4_POLYVINYLIDENE_FLUORIDE  # scripted group (container) (typed FeaturePython)
  Dunit = g/cm3
  Dvalue = 1.76
  Group = -> [C_element686,H_element638,F_element092]
  conduct = 2
  density = 1
  expand = 3
  formula = G4_POLYVINYLIDENE_FLUORIDE
  name = G4_POLYVINYLIDENE_FLUORIDE
  specific = 4
FEATURE [App::DocumentObjectGroupPython] C_element687  label="C_element : 451"  # scripted group (container) (typed FeaturePython)
  n = 6
  ref = C_element
FEATURE [App::DocumentObjectGroupPython] H_element639  label="H_element : 414"  # scripted group (container) (typed FeaturePython)
  n = 9
  ref = H_element
FEATURE [App::DocumentObjectGroupPython] N_element309  label="N_element : 167"  # scripted group (container) (typed FeaturePython)
  n = 1
  ref = N_element
FEATURE [App::DocumentObjectGroupPython] O_element604  label="O_element : 383"  # scripted group (container) (typed FeaturePython)
  n = 1
  ref = O_element
FEATURE [App::DocumentObjectGroupPython] G4_POLYVINYL_PYRROLIDONE  # scripted group (container) (typed FeaturePython)
  Dunit = g/cm3
  Dvalue = 1.25
  Group = -> [C_element687,H_element639,N_element309,O_element604]
  conduct = 2
  density = 1
  expand = 3
  formula = G4_POLYVINYL_PYRROLIDONE
  name = G4_POLYVINYL_PYRROLIDONE
  specific = 4
FEATURE [App::DocumentObjectGroupPython] K_element060  label="K_element : 011"  # scripted group (container) (typed FeaturePython)
  n = 1
  ref = K_element
FEATURE [App::DocumentObjectGroupPython] I_element046  label="I_element : 029"  # scripted group (container) (typed FeaturePython)
  n = 1
  ref = I_element
FEATURE [App::DocumentObjectGroupPython] G4_POTASSIUM_IODIDE  # scripted group (container) (typed FeaturePython)
  Dunit = g/cm3
  Dvalue = 3.13
  Group = -> [K_element060,I_element046]
  conduct = 2
  density = 1
  expand = 3
  formula = G4_POTASSIUM_IODIDE
  name = G4_POTASSIUM_IODIDE
  specific = 4
FEATURE [App::DocumentObjectGroupPython] K_element061  label="K_element : 012"  # scripted group (container) (typed FeaturePython)
  n = 2
  ref = K_element
FEATURE [App::DocumentObjectGroupPython] O_element605  label="O_element : 384"  # scripted group (container) (typed FeaturePython)
  n = 1
  ref = O_element
FEATURE [App::DocumentObjectGroupPython] G4_POTASSIUM_OXIDE  # scripted group (container) (typed FeaturePython)
  Dunit = g/cm3
  Dvalue = 2.32
  Group = -> [K_element061,O_element605]
  conduct = 2
  density = 1
  expand = 3
  formula = G4_POTASSIUM_OXIDE
  name = G4_POTASSIUM_OXIDE
  specific = 4
FEATURE [App::DocumentObjectGroupPython] C_element688  label="C_element : 452"  # scripted group (container) (typed FeaturePython)
  n = 3
  ref = C_element
FEATURE [App::DocumentObjectGroupPython] H_element640  label="H_element : 415"  # scripted group (container) (typed FeaturePython)
  n = 8
  ref = H_element
FEATURE [App::DocumentObjectGroupPython] G4_PROPANE  # scripted group (container) (typed FeaturePython)
  Dunit = g/cm3
  Dvalue = 0.00187939
  Group = -> [C_element688,H_element640]
  conduct = 2
  density = 1
  expand = 3
  formula = G4_PROPANE
  name = G4_PROPANE
  specific = 4
FEATURE [App::DocumentObjectGroupPython] C_element689  label="C_element : 453"  # scripted group (container) (typed FeaturePython)
  n = 3
  ref = C_element
FEATURE [App::DocumentObjectGroupPython] H_element641  label="H_element : 416"  # scripted group (container) (typed FeaturePython)
  n = 8
  ref = H_element
FEATURE [App::DocumentObjectGroupPython] G4_lPROPANE  # scripted group (container) (typed FeaturePython)
  Dunit = g/cm3
  Dvalue = 0.43
  Group = -> [C_element689,H_element641]
  conduct = 2
  density = 1
  expand = 3
  formula = G4_lPROPANE
  name = G4_lPROPANE
  specific = 4
FEATURE [App::DocumentObjectGroupPython] C_element690  label="C_element : 454"  # scripted group (container) (typed FeaturePython)
  n = 3
  ref = C_element
FEATURE [App::DocumentObjectGroupPython] H_element642  label="H_element : 417"  # scripted group (container) (typed FeaturePython)
  n = 8
  ref = H_element
FEATURE [App::DocumentObjectGroupPython] O_element606  label="O_element : 385"  # scripted group (container) (typed FeaturePython)
  n = 1
  ref = O_element
FEATURE [App::DocumentObjectGroupPython] G4_N_PROPYL_ALCOHOL  label="G4_N-PROPYL_ALCOHOL"  # scripted group (container) (typed FeaturePython)
  Dunit = g/cm3
  Dvalue = 0.8035
  Group = -> [C_element690,H_element642,O_element606]
  conduct = 2
  density = 1
  expand = 3
  formula = G4_N-PROPYL_ALCOHOL
  name = G4_N-PROPYL_ALCOHOL
  specific = 4
FEATURE [App::DocumentObjectGroupPython] C_element691  label="C_element : 455"  # scripted group (container) (typed FeaturePython)
  n = 5
  ref = C_element
FEATURE [App::DocumentObjectGroupPython] H_element643  label="H_element : 418"  # scripted group (container) (typed FeaturePython)
  n = 5
  ref = H_element
FEATURE [App::DocumentObjectGroupPython] N_element310  label="N_element : 168"  # scripted group (container) (typed FeaturePython)
  n = 1
  ref = N_element
FEATURE [App::DocumentObjectGroupPython] G4_PYRIDINE  # scripted group (container) (typed FeaturePython)
  Dunit = g/cm3
  Dvalue = 0.9819
  Group = -> [C_element691,H_element643,N_element310]
  conduct = 2
  density = 1
  expand = 3
  formula = G4_PYRIDINE
  name = G4_PYRIDINE
  specific = 4
FEATURE [App::DocumentObjectGroupPython] H_element644  label="H_element : 0.276"  # scripted group (container) (typed FeaturePython)
  n = 0.143711
FEATURE [App::DocumentObjectGroupPython] C_element692  label="C_element : 0.1007"  # scripted group (container) (typed FeaturePython)
  n = 0.856289
FEATURE [App::DocumentObjectGroupPython] G4_RUBBER_BUTYL  # scripted group (container) (typed FeaturePython)
  Dunit = g/cm3
  Dvalue = 0.92
  Group = -> [H_element644,C_element692]
  conduct = 2
  density = 1
  expand = 3
  formula = G4_RUBBER_BUTYL
  name = G4_RUBBER_BUTYL
  specific = 4
FEATURE [App::DocumentObjectGroupPython] H_element645  label="H_element : 0.277"  # scripted group (container) (typed FeaturePython)
  n = 0.118371
FEATURE [App::DocumentObjectGroupPython] C_element693  label="C_element : 0.1008"  # scripted group (container) (typed FeaturePython)
  n = 0.881629
FEATURE [App::DocumentObjectGroupPython] G4_RUBBER_NATURAL  # scripted group (container) (typed FeaturePython)
  Dunit = g/cm3
  Dvalue = 0.92
  Group = -> [H_element645,C_element693]
  conduct = 2
  density = 1
  expand = 3
  formula = G4_RUBBER_NATURAL
  name = G4_RUBBER_NATURAL
  specific = 4
FEATURE [App::DocumentObjectGroupPython] H_element646  label="H_element : 0.278"  # scripted group (container) (typed FeaturePython)
  n = 0.05692
FEATURE [App::DocumentObjectGroupPython] C_element694  label="C_element : 0.1009"  # scripted group (container) (typed FeaturePython)
  n = 0.542646
FEATURE [App::DocumentObjectGroupPython] Cl_element141  label="Cl_element : 0.637"  # scripted group (container) (typed FeaturePython)
  n = 0.400434
FEATURE [App::DocumentObjectGroupPython] G4_RUBBER_NEOPRENE  # scripted group (container) (typed FeaturePython)
  Dunit = g/cm3
  Dvalue = 1.23
  Group = -> [H_element646,C_element694,Cl_element141]
  conduct = 2
  density = 1
  expand = 3
  formula = G4_RUBBER_NEOPRENE
  name = G4_RUBBER_NEOPRENE
  specific = 4
FEATURE [App::DocumentObjectGroupPython] Si_element034  label="Si_element : 008"  # scripted group (container) (typed FeaturePython)
  n = 1
  ref = Si_element
FEATURE [App::DocumentObjectGroupPython] O_element607  label="O_element : 386"  # scripted group (container) (typed FeaturePython)
  n = 2
  ref = O_element
FEATURE [App::DocumentObjectGroupPython] G4_SILICON_DIOXIDE  # scripted group (container) (typed FeaturePython)
  Dunit = g/cm3
  Dvalue = 2.32
  Group = -> [Si_element034,O_element607]
  conduct = 2
  density = 1
  expand = 3
  formula = G4_SILICON_DIOXIDE
  name = G4_SILICON_DIOXIDE
  specific = 4
FEATURE [App::DocumentObjectGroupPython] Ag_element026  label="Ag_element : 016"  # scripted group (container) (typed FeaturePython)
  n = 1
  ref = Ag_element
FEATURE [App::DocumentObjectGroupPython] Br_element033  label="Br_element : 018"  # scripted group (container) (typed FeaturePython)
  n = 1
  ref = Br_element
FEATURE [App::DocumentObjectGroupPython] G4_SILVER_BROMIDE  # scripted group (container) (typed FeaturePython)
  Dunit = g/cm3
  Dvalue = 6.473
  Group = -> [Ag_element026,Br_element033]
  conduct = 2
  density = 1
  expand = 3
  formula = G4_SILVER_BROMIDE
  name = G4_SILVER_BROMIDE
  specific = 4
FEATURE [App::DocumentObjectGroupPython] Ag_element027  label="Ag_element : 017"  # scripted group (container) (typed FeaturePython)
  n = 1
  ref = Ag_element
FEATURE [App::DocumentObjectGroupPython] Cl_element142  label="Cl_element : 071"  # scripted group (container) (typed FeaturePython)
  n = 1
  ref = Cl_element
FEATURE [App::DocumentObjectGroupPython] G4_SILVER_CHLORIDE  # scripted group (container) (typed FeaturePython)
  Dunit = g/cm3
  Dvalue = 5.56
  Group = -> [Ag_element027,Cl_element142]
  conduct = 2
  density = 1
  expand = 3
  formula = G4_SILVER_CHLORIDE
  name = G4_SILVER_CHLORIDE
  specific = 4
FEATURE [App::DocumentObjectGroupPython] Br_element034  label="Br_element : 0.771"  # scripted group (container) (typed FeaturePython)
  n = 0.422895
FEATURE [App::DocumentObjectGroupPython] Ag_element028  label="Ag_element : 0.580"  # scripted group (container) (typed FeaturePython)
  n = 0.573748
FEATURE [App::DocumentObjectGroupPython] I_element047  label="I_element : 0.659"  # scripted group (container) (typed FeaturePython)
  n = 0.003357
FEATURE [App::DocumentObjectGroupPython] G4_SILVER_HALIDES  # scripted group (container) (typed FeaturePython)
  Dunit = g/cm3
  Dvalue = 6.47
  Group = -> [Br_element034,Ag_element028,I_element047]
  conduct = 2
  density = 1
  expand = 3
  formula = G4_SILVER_HALIDES
  name = G4_SILVER_HALIDES
  specific = 4
FEATURE [App::DocumentObjectGroupPython] Ag_element029  label="Ag_element : 018"  # scripted group (container) (typed FeaturePython)
  n = 1
  ref = Ag_element
FEATURE [App::DocumentObjectGroupPython] I_element048  label="I_element : 030"  # scripted group (container) (typed FeaturePython)
  n = 1
  ref = I_element
FEATURE [App::DocumentObjectGroupPython] G4_SILVER_IODIDE  # scripted group (container) (typed FeaturePython)
  Dunit = g/cm3
  Dvalue = 6.01
  Group = -> [Ag_element029,I_element048]
  conduct = 2
  density = 1
  expand = 3
  formula = G4_SILVER_IODIDE
  name = G4_SILVER_IODIDE
  specific = 4
FEATURE [App::DocumentObjectGroupPython] H_element647  label="H_element : 0.279"  # scripted group (container) (typed FeaturePython)
  n = 0.1
FEATURE [App::DocumentObjectGroupPython] C_element695  label="C_element : 0.1010"  # scripted group (container) (typed FeaturePython)
  n = 0.204
FEATURE [App::DocumentObjectGroupPython] N_element311  label="N_element : 0.851"  # scripted group (container) (typed FeaturePython)
  n = 0.042
FEATURE [App::DocumentObjectGroupPython] O_element608  label="O_element : 0.1001"  # scripted group (container) (typed FeaturePython)
  n = 0.645
FEATURE [App::DocumentObjectGroupPython] Na_element093  label="Na_element : 0.154"  # scripted group (container) (typed FeaturePython)
  n = 0.002
FEATURE [App::DocumentObjectGroupPython] P_element085  label="P_element : 0.146"  # scripted group (container) (typed FeaturePython)
  n = 0.001
FEATURE [App::DocumentObjectGroupPython] S_element112  label="S_element : 0.078"  # scripted group (container) (typed FeaturePython)
  n = 0.002
FEATURE [App::DocumentObjectGroupPython] Cl_element143  label="Cl_element : 0.638"  # scripted group (container) (typed FeaturePython)
  n = 0.003
FEATURE [App::DocumentObjectGroupPython] K_element062  label="K_element : 0.051"  # scripted group (container) (typed FeaturePython)
  n = 0.001
FEATURE [App::DocumentObjectGroupPython] G4_SKIN_ICRP  # scripted group (container) (typed FeaturePython)
  Dunit = g/cm3
  Dvalue = 1.09
  Group = -> [H_element647,C_element695,N_element311,O_element608,Na_element093,P_element085,S_element112,Cl_element143,K_element062]
  conduct = 2
  density = 1
  expand = 3
  formula = G4_SKIN_ICRP
  name = G4_SKIN_ICRP
  specific = 4
FEATURE [App::DocumentObjectGroupPython] Na_element094  label="Na_element : 019"  # scripted group (container) (typed FeaturePython)
  n = 2
  ref = Na_element
FEATURE [App::DocumentObjectGroupPython] C_element696  label="C_element : 456"  # scripted group (container) (typed FeaturePython)
  n = 1
  ref = C_element
FEATURE [App::DocumentObjectGroupPython] O_element609  label="O_element : 387"  # scripted group (container) (typed FeaturePython)
  n = 3
  ref = O_element
FEATURE [App::DocumentObjectGroupPython] G4_SODIUM_CARBONATE  # scripted group (container) (typed FeaturePython)
  Dunit = g/cm3
  Dvalue = 2.532
  Group = -> [Na_element094,C_element696,O_element609]
  conduct = 2
  density = 1
  expand = 3
  formula = G4_SODIUM_CARBONATE
  name = G4_SODIUM_CARBONATE
  specific = 4
FEATURE [App::DocumentObjectGroupPython] Na_element095  label="Na_element : 020"  # scripted group (container) (typed FeaturePython)
  n = 1
  ref = Na_element
FEATURE [App::DocumentObjectGroupPython] I_element049  label="I_element : 031"  # scripted group (container) (typed FeaturePython)
  n = 1
  ref = I_element
FEATURE [App::DocumentObjectGroupPython] G4_SODIUM_IODIDE  # scripted group (container) (typed FeaturePython)
  Dunit = g/cm3
  Dvalue = 3.667
  Group = -> [Na_element095,I_element049]
  conduct = 2
  density = 1
  expand = 3
  formula = G4_SODIUM_IODIDE
  name = G4_SODIUM_IODIDE
  specific = 4
FEATURE [App::DocumentObjectGroupPython] Na_element096  label="Na_element : 021"  # scripted group (container) (typed FeaturePython)
  n = 2
  ref = Na_element
FEATURE [App::DocumentObjectGroupPython] O_element610  label="O_element : 388"  # scripted group (container) (typed FeaturePython)
  n = 1
  ref = O_element
FEATURE [App::DocumentObjectGroupPython] G4_SODIUM_MONOXIDE  # scripted group (container) (typed FeaturePython)
  Dunit = g/cm3
  Dvalue = 2.27
  Group = -> [Na_element096,O_element610]
  conduct = 2
  density = 1
  expand = 3
  formula = G4_SODIUM_MONOXIDE
  name = G4_SODIUM_MONOXIDE
  specific = 4
FEATURE [App::DocumentObjectGroupPython] Na_element097  label="Na_element : 022"  # scripted group (container) (typed FeaturePython)
  n = 1
  ref = Na_element
FEATURE [App::DocumentObjectGroupPython] N_element312  label="N_element : 169"  # scripted group (container) (typed FeaturePython)
  n = 1
  ref = N_element
FEATURE [App::DocumentObjectGroupPython] O_element611  label="O_element : 389"  # scripted group (container) (typed FeaturePython)
  n = 3
  ref = O_element
FEATURE [App::DocumentObjectGroupPython] G4_SODIUM_NITRATE  # scripted group (container) (typed FeaturePython)
  Dunit = g/cm3
  Dvalue = 2.261
  Group = -> [Na_element097,N_element312,O_element611]
  conduct = 2
  density = 1
  expand = 3
  formula = G4_SODIUM_NITRATE
  name = G4_SODIUM_NITRATE
  specific = 4
FEATURE [App::DocumentObjectGroupPython] C_element697  label="C_element : 457"  # scripted group (container) (typed FeaturePython)
  n = 14
  ref = C_element
FEATURE [App::DocumentObjectGroupPython] H_element648  label="H_element : 419"  # scripted group (container) (typed FeaturePython)
  n = 12
  ref = H_element
FEATURE [App::DocumentObjectGroupPython] G4_STILBENE  # scripted group (container) (typed FeaturePython)
  Dunit = g/cm3
  Dvalue = 0.9707
  Group = -> [C_element697,H_element648]
  conduct = 2
  density = 1
  expand = 3
  formula = G4_STILBENE
  name = G4_STILBENE
  specific = 4
FEATURE [App::DocumentObjectGroupPython] C_element698  label="C_element : 458"  # scripted group (container) (typed FeaturePython)
  n = 12
  ref = C_element
FEATURE [App::DocumentObjectGroupPython] H_element649  label="H_element : 420"  # scripted group (container) (typed FeaturePython)
  n = 22
  ref = H_element
FEATURE [App::DocumentObjectGroupPython] O_element612  label="O_element : 390"  # scripted group (container) (typed FeaturePython)
  n = 11
  ref = O_element
FEATURE [App::DocumentObjectGroupPython] G4_SUCROSE  # scripted group (container) (typed FeaturePython)
  Dunit = g/cm3
  Dvalue = 1.5805
  Group = -> [C_element698,H_element649,O_element612]
  conduct = 2
  density = 1
  expand = 3
  formula = G4_SUCROSE
  name = G4_SUCROSE
  specific = 4
FEATURE [App::DocumentObjectGroupPython] C_element699  label="C_element : 459"  # scripted group (container) (typed FeaturePython)
  n = 18
  ref = C_element
FEATURE [App::DocumentObjectGroupPython] H_element650  label="H_element : 421"  # scripted group (container) (typed FeaturePython)
  n = 14
  ref = H_element
FEATURE [App::DocumentObjectGroupPython] G4_TERPHENYL  # scripted group (container) (typed FeaturePython)
  Dunit = g/cm3
  Dvalue = 1.24
  Group = -> [C_element699,H_element650]
  conduct = 2
  density = 1
  expand = 3
  formula = G4_TERPHENYL
  name = G4_TERPHENYL
  specific = 4
FEATURE [App::DocumentObjectGroupPython] H_element651  label="H_element : 0.280"  # scripted group (container) (typed FeaturePython)
  n = 0.106
FEATURE [App::DocumentObjectGroupPython] C_element700  label="C_element : 0.1011"  # scripted group (container) (typed FeaturePython)
  n = 0.099
FEATURE [App::DocumentObjectGroupPython] N_element313  label="N_element : 0.852"  # scripted group (container) (typed FeaturePython)
  n = 0.02
FEATURE [App::DocumentObjectGroupPython] O_element613  label="O_element : 0.1002"  # scripted group (container) (typed FeaturePython)
  n = 0.766
FEATURE [App::DocumentObjectGroupPython] Na_element098  label="Na_element : 0.155"  # scripted group (container) (typed FeaturePython)
  n = 0.002
FEATURE [App::DocumentObjectGroupPython] P_element086  label="P_element : 0.147"  # scripted group (container) (typed FeaturePython)
  n = 0.001
FEATURE [App::DocumentObjectGroupPython] S_element113  label="S_element : 0.079"  # scripted group (container) (typed FeaturePython)
  n = 0.002
FEATURE [App::DocumentObjectGroupPython] Cl_element144  label="Cl_element : 0.639"  # scripted group (container) (typed FeaturePython)
  n = 0.002
FEATURE [App::DocumentObjectGroupPython] K_element063  label="K_element : 0.052"  # scripted group (container) (typed FeaturePython)
  n = 0.002
FEATURE [App::DocumentObjectGroupPython] G4_TESTIS_ICRP  # scripted group (container) (typed FeaturePython)
  Dunit = g/cm3
  Dvalue = 1.04
  Group = -> [H_element651,C_element700,N_element313,O_element613,Na_element098,P_element086,S_element113,Cl_element144,K_element063]
  conduct = 2
  density = 1
  expand = 3
  formula = G4_TESTIS_ICRP
  name = G4_TESTIS_ICRP
  specific = 4
FEATURE [App::DocumentObjectGroupPython] C_element701  label="C_element : 460"  # scripted group (container) (typed FeaturePython)
  n = 2
  ref = C_element
FEATURE [App::DocumentObjectGroupPython] Cl_element145  label="Cl_element : 072"  # scripted group (container) (typed FeaturePython)
  n = 4
  ref = Cl_element
FEATURE [App::DocumentObjectGroupPython] G4_TETRACHLOROETHYLENE  # scripted group (container) (typed FeaturePython)
  Dunit = g/cm3
  Dvalue = 1.625
  Group = -> [C_element701,Cl_element145]
  conduct = 2
  density = 1
  expand = 3
  formula = G4_TETRACHLOROETHYLENE
  name = G4_TETRACHLOROETHYLENE
  specific = 4
FEATURE [App::DocumentObjectGroupPython] Tl_element009  label="Tl_element : 008"  # scripted group (container) (typed FeaturePython)
  n = 1
  ref = Tl_element
FEATURE [App::DocumentObjectGroupPython] Cl_element146  label="Cl_element : 073"  # scripted group (container) (typed FeaturePython)
  n = 1
  ref = Cl_element
FEATURE [App::DocumentObjectGroupPython] G4_THALLIUM_CHLORIDE  # scripted group (container) (typed FeaturePython)
  Dunit = g/cm3
  Dvalue = 7.004
  Group = -> [Tl_element009,Cl_element146]
  conduct = 2
  density = 1
  expand = 3
  formula = G4_THALLIUM_CHLORIDE
  name = G4_THALLIUM_CHLORIDE
  specific = 4
FEATURE [App::DocumentObjectGroupPython] H_element652  label="H_element : 0.281"  # scripted group (container) (typed FeaturePython)
  n = 0.105
FEATURE [App::DocumentObjectGroupPython] C_element702  label="C_element : 0.1012"  # scripted group (container) (typed FeaturePython)
  n = 0.256
FEATURE [App::DocumentObjectGroupPython] N_element314  label="N_element : 0.853"  # scripted group (container) (typed FeaturePython)
  n = 0.027
FEATURE [App::DocumentObjectGroupPython] O_element614  label="O_element : 0.1003"  # scripted group (container) (typed FeaturePython)
  n = 0.602
FEATURE [App::DocumentObjectGroupPython] Na_element099  label="Na_element : 0.156"  # scripted group (container) (typed FeaturePython)
  n = 0.001
FEATURE [App::DocumentObjectGroupPython] P_element087  label="P_element : 0.148"  # scripted group (container) (typed FeaturePython)
  n = 0.002
FEATURE [App::DocumentObjectGroupPython] S_element114  label="S_element : 0.080"  # scripted group (container) (typed FeaturePython)
  n = 0.003
FEATURE [App::DocumentObjectGroupPython] Cl_element147  label="Cl_element : 0.640"  # scripted group (container) (typed FeaturePython)
  n = 0.002
FEATURE [App::DocumentObjectGroupPython] K_element064  label="K_element : 0.053"  # scripted group (container) (typed FeaturePython)
  n = 0.002
FEATURE [App::DocumentObjectGroupPython] G4_TISSUE_SOFT_ICRP  # scripted group (container) (typed FeaturePython)
  Dunit = g/cm3
  Dvalue = 1.03
  Group = -> [H_element652,C_element702,N_element314,O_element614,Na_element099,P_element087,S_element114,Cl_element147,K_element064]
  conduct = 2
  density = 1
  expand = 3
  formula = G4_TISSUE_SOFT_ICRP
  name = G4_TISSUE_SOFT_ICRP
  specific = 4
FEATURE [App::DocumentObjectGroupPython] H_element653  label="H_element : 0.282"  # scripted group (container) (typed FeaturePython)
  n = 0.101
FEATURE [App::DocumentObjectGroupPython] C_element703  label="C_element : 0.1013"  # scripted group (container) (typed FeaturePython)
  n = 0.111
FEATURE [App::DocumentObjectGroupPython] N_element315  label="N_element : 0.854"  # scripted group (container) (typed FeaturePython)
  n = 0.026
FEATURE [App::DocumentObjectGroupPython] O_element615  label="O_element : 0.1004"  # scripted group (container) (typed FeaturePython)
  n = 0.762
FEATURE [App::DocumentObjectGroupPython] G4_TISSUE_SOFT_ICRU_4  label="G4_TISSUE_SOFT_ICRU-4"  # scripted group (container) (typed FeaturePython)
  Dunit = g/cm3
  Dvalue = 1
  Group = -> [H_element653,C_element703,N_element315,O_element615]
  conduct = 2
  density = 1
  expand = 3
  formula = G4_TISSUE_SOFT_ICRU-4
  name = G4_TISSUE_SOFT_ICRU-4
  specific = 4
FEATURE [App::DocumentObjectGroupPython] H_element654  label="H_element : 0.283"  # scripted group (container) (typed FeaturePython)
  n = 0.101869
FEATURE [App::DocumentObjectGroupPython] C_element704  label="C_element : 0.1014"  # scripted group (container) (typed FeaturePython)
  n = 0.456179
FEATURE [App::DocumentObjectGroupPython] N_element316  label="N_element : 0.855"  # scripted group (container) (typed FeaturePython)
  n = 0.035172
FEATURE [App::DocumentObjectGroupPython] O_element616  label="O_element : 0.1005"  # scripted group (container) (typed FeaturePython)
  n = 0.40678
FEATURE [App::DocumentObjectGroupPython] G4_TISSUE_METHANE  label="G4_TISSUE-METHANE"  # scripted group (container) (typed FeaturePython)
  Dunit = g/cm3
  Dvalue = 0.00106409
  Group = -> [H_element654,C_element704,N_element316,O_element616]
  conduct = 2
  density = 1
  expand = 3
  formula = G4_TISSUE-METHANE
  name = G4_TISSUE-METHANE
  specific = 4
FEATURE [App::DocumentObjectGroupPython] H_element655  label="H_element : 0.284"  # scripted group (container) (typed FeaturePython)
  n = 0.102672
FEATURE [App::DocumentObjectGroupPython] C_element705  label="C_element : 0.1015"  # scripted group (container) (typed FeaturePython)
  n = 0.56894
FEATURE [App::DocumentObjectGroupPython] N_element317  label="N_element : 0.856"  # scripted group (container) (typed FeaturePython)
  n = 0.035022
FEATURE [App::DocumentObjectGroupPython] O_element617  label="O_element : 0.1006"  # scripted group (container) (typed FeaturePython)
  n = 0.293366
FEATURE [App::DocumentObjectGroupPython] G4_TISSUE_PROPANE  label="G4_TISSUE-PROPANE"  # scripted group (container) (typed FeaturePython)
  Dunit = g/cm3
  Dvalue = 0.00182628
  Group = -> [H_element655,C_element705,N_element317,O_element617]
  conduct = 2
  density = 1
  expand = 3
  formula = G4_TISSUE-PROPANE
  name = G4_TISSUE-PROPANE
  specific = 4
FEATURE [App::DocumentObjectGroupPython] Ti_element019  label="Ti_element : 008"  # scripted group (container) (typed FeaturePython)
  n = 1
  ref = Ti_element
FEATURE [App::DocumentObjectGroupPython] O_element618  label="O_element : 391"  # scripted group (container) (typed FeaturePython)
  n = 2
  ref = O_element
FEATURE [App::DocumentObjectGroupPython] G4_TITANIUM_DIOXIDE  # scripted group (container) (typed FeaturePython)
  Dunit = g/cm3
  Dvalue = 4.26
  Group = -> [Ti_element019,O_element618]
  conduct = 2
  density = 1
  expand = 3
  formula = G4_TITANIUM_DIOXIDE
  name = G4_TITANIUM_DIOXIDE
  specific = 4
FEATURE [App::DocumentObjectGroupPython] C_element706  label="C_element : 461"  # scripted group (container) (typed FeaturePython)
  n = 7
  ref = C_element
FEATURE [App::DocumentObjectGroupPython] H_element656  label="H_element : 422"  # scripted group (container) (typed FeaturePython)
  n = 8
  ref = H_element
FEATURE [App::DocumentObjectGroupPython] G4_TOLUENE  # scripted group (container) (typed FeaturePython)
  Dunit = g/cm3
  Dvalue = 0.8669
  Group = -> [C_element706,H_element656]
  conduct = 2
  density = 1
  expand = 3
  formula = G4_TOLUENE
  name = G4_TOLUENE
  specific = 4
FEATURE [App::DocumentObjectGroupPython] C_element707  label="C_element : 462"  # scripted group (container) (typed FeaturePython)
  n = 2
  ref = C_element
FEATURE [App::DocumentObjectGroupPython] H_element657  label="H_element : 423"  # scripted group (container) (typed FeaturePython)
  n = 1
  ref = H_element
FEATURE [App::DocumentObjectGroupPython] Cl_element148  label="Cl_element : 074"  # scripted group (container) (typed FeaturePython)
  n = 3
  ref = Cl_element
FEATURE [App::DocumentObjectGroupPython] G4_TRICHLOROETHYLENE  # scripted group (container) (typed FeaturePython)
  Dunit = g/cm3
  Dvalue = 1.46
  Group = -> [C_element707,H_element657,Cl_element148]
  conduct = 2
  density = 1
  expand = 3
  formula = G4_TRICHLOROETHYLENE
  name = G4_TRICHLOROETHYLENE
  specific = 4
FEATURE [App::DocumentObjectGroupPython] C_element708  label="C_element : 463"  # scripted group (container) (typed FeaturePython)
  n = 6
  ref = C_element
FEATURE [App::DocumentObjectGroupPython] H_element658  label="H_element : 424"  # scripted group (container) (typed FeaturePython)
  n = 15
  ref = H_element
FEATURE [App::DocumentObjectGroupPython] O_element619  label="O_element : 392"  # scripted group (container) (typed FeaturePython)
  n = 4
  ref = O_element
FEATURE [App::DocumentObjectGroupPython] P_element088  label="P_element : 032"  # scripted group (container) (typed FeaturePython)
  n = 1
  ref = P_element
FEATURE [App::DocumentObjectGroupPython] G4_TRIETHYL_PHOSPHATE  # scripted group (container) (typed FeaturePython)
  Dunit = g/cm3
  Dvalue = 1.07
  Group = -> [C_element708,H_element658,O_element619,P_element088]
  conduct = 2
  density = 1
  expand = 3
  formula = G4_TRIETHYL_PHOSPHATE
  name = G4_TRIETHYL_PHOSPHATE
  specific = 4
FEATURE [App::DocumentObjectGroupPython] W_element023  label="W_element : 022"  # scripted group (container) (typed FeaturePython)
  n = 1
  ref = W_element
FEATURE [App::DocumentObjectGroupPython] F_element093  label="F_element : 046"  # scripted group (container) (typed FeaturePython)
  n = 6
  ref = F_element
FEATURE [App::DocumentObjectGroupPython] G4_TUNGSTEN_HEXAFLUORIDE  # scripted group (container) (typed FeaturePython)
  Dunit = g/cm3
  Dvalue = 2.4
  Group = -> [W_element023,F_element093]
  conduct = 2
  density = 1
  expand = 3
  formula = G4_TUNGSTEN_HEXAFLUORIDE
  name = G4_TUNGSTEN_HEXAFLUORIDE
  specific = 4
FEATURE [App::DocumentObjectGroupPython] U_element017  label="U_element : 016"  # scripted group (container) (typed FeaturePython)
  n = 1
  ref = U_element
FEATURE [App::DocumentObjectGroupPython] C_element709  label="C_element : 464"  # scripted group (container) (typed FeaturePython)
  n = 2
  ref = C_element
FEATURE [App::DocumentObjectGroupPython] G4_URANIUM_DICARBIDE  # scripted group (container) (typed FeaturePython)
  Dunit = g/cm3
  Dvalue = 11.28
  Group = -> [U_element017,C_element709]
  conduct = 2
  density = 1
  expand = 3
  formula = G4_URANIUM_DICARBIDE
  name = G4_URANIUM_DICARBIDE
  specific = 4
FEATURE [App::DocumentObjectGroupPython] U_element018  label="U_element : 017"  # scripted group (container) (typed FeaturePython)
  n = 1
  ref = U_element
FEATURE [App::DocumentObjectGroupPython] C_element710  label="C_element : 465"  # scripted group (container) (typed FeaturePython)
  n = 1
  ref = C_element
FEATURE [App::DocumentObjectGroupPython] G4_URANIUM_MONOCARBIDE  # scripted group (container) (typed FeaturePython)
  Dunit = g/cm3
  Dvalue = 13.63
  Group = -> [U_element018,C_element710]
  conduct = 2
  density = 1
  expand = 3
  formula = G4_URANIUM_MONOCARBIDE
  name = G4_URANIUM_MONOCARBIDE
  specific = 4
FEATURE [App::DocumentObjectGroupPython] U_element019  label="U_element : 018"  # scripted group (container) (typed FeaturePython)
  n = 1
  ref = U_element
FEATURE [App::DocumentObjectGroupPython] O_element620  label="O_element : 393"  # scripted group (container) (typed FeaturePython)
  n = 2
  ref = O_element
FEATURE [App::DocumentObjectGroupPython] G4_URANIUM_OXIDE  # scripted group (container) (typed FeaturePython)
  Dunit = g/cm3
  Dvalue = 10.96
  Group = -> [U_element019,O_element620]
  conduct = 2
  density = 1
  expand = 3
  formula = G4_URANIUM_OXIDE
  name = G4_URANIUM_OXIDE
  specific = 4
FEATURE [App::DocumentObjectGroupPython] C_element711  label="C_element : 466"  # scripted group (container) (typed FeaturePython)
  n = 1
  ref = C_element
FEATURE [App::DocumentObjectGroupPython] H_element659  label="H_element : 425"  # scripted group (container) (typed FeaturePython)
  n = 4
  ref = H_element
FEATURE [App::DocumentObjectGroupPython] N_element318  label="N_element : 170"  # scripted group (container) (typed FeaturePython)
  n = 2
  ref = N_element
FEATURE [App::DocumentObjectGroupPython] O_element621  label="O_element : 394"  # scripted group (container) (typed FeaturePython)
  n = 1
  ref = O_element
FEATURE [App::DocumentObjectGroupPython] G4_UREA  # scripted group (container) (typed FeaturePython)
  Dunit = g/cm3
  Dvalue = 1.323
  Group = -> [C_element711,H_element659,N_element318,O_element621]
  conduct = 2
  density = 1
  expand = 3
  formula = G4_UREA
  name = G4_UREA
  specific = 4
FEATURE [App::DocumentObjectGroupPython] C_element712  label="C_element : 467"  # scripted group (container) (typed FeaturePython)
  n = 5
  ref = C_element
FEATURE [App::DocumentObjectGroupPython] H_element660  label="H_element : 426"  # scripted group (container) (typed FeaturePython)
  n = 11
  ref = H_element
FEATURE [App::DocumentObjectGroupPython] N_element319  label="N_element : 171"  # scripted group (container) (typed FeaturePython)
  n = 1
  ref = N_element
FEATURE [App::DocumentObjectGroupPython] O_element622  label="O_element : 395"  # scripted group (container) (typed FeaturePython)
  n = 2
  ref = O_element
FEATURE [App::DocumentObjectGroupPython] G4_VALINE  # scripted group (container) (typed FeaturePython)
  Dunit = g/cm3
  Dvalue = 1.23
  Group = -> [C_element712,H_element660,N_element319,O_element622]
  conduct = 2
  density = 1
  expand = 3
  formula = G4_VALINE
  name = G4_VALINE
  specific = 4
FEATURE [App::DocumentObjectGroupPython] H_element661  label="H_element : 0.285"  # scripted group (container) (typed FeaturePython)
  n = 0.009417
FEATURE [App::DocumentObjectGroupPython] C_element713  label="C_element : 0.1016"  # scripted group (container) (typed FeaturePython)
  n = 0.280555
FEATURE [App::DocumentObjectGroupPython] F_element094  label="F_element : 0.734"  # scripted group (container) (typed FeaturePython)
  n = 0.710028
FEATURE [App::DocumentObjectGroupPython] G4_VITON  # scripted group (container) (typed FeaturePython)
  Dunit = g/cm3
  Dvalue = 1.8
  Group = -> [H_element661,C_element713,F_element094]
  conduct = 2
  density = 1
  expand = 3
  formula = G4_VITON
  name = G4_VITON
  specific = 4
FEATURE [App::DocumentObjectGroupPython] H_element662  label="H_element : 427"  # scripted group (container) (typed FeaturePython)
  n = 2
  ref = H_element
FEATURE [App::DocumentObjectGroupPython] O_element623  label="O_element : 396"  # scripted group (container) (typed FeaturePython)
  n = 1
  ref = O_element
FEATURE [App::DocumentObjectGroupPython] G4_WATER  # scripted group (container) (typed FeaturePython)
  Dunit = g/cm3
  Dvalue = 1
  Group = -> [H_element662,O_element623]
  conduct = 2
  density = 1
  expand = 3
  formula = G4_WATER
  name = G4_WATER
  specific = 4
FEATURE [App::DocumentObjectGroupPython] H_element663  label="H_element : 428"  # scripted group (container) (typed FeaturePython)
  n = 2
  ref = H_element
FEATURE [App::DocumentObjectGroupPython] O_element624  label="O_element : 397"  # scripted group (container) (typed FeaturePython)
  n = 1
  ref = O_element
FEATURE [App::DocumentObjectGroupPython] G4_WATER_VAPOR  # scripted group (container) (typed FeaturePython)
  Dunit = g/cm3
  Dvalue = 0.000756182
  Group = -> [H_element663,O_element624]
  conduct = 2
  density = 1
  expand = 3
  formula = G4_WATER_VAPOR
  name = G4_WATER_VAPOR
  specific = 4
FEATURE [App::DocumentObjectGroupPython] C_element714  label="C_element : 468"  # scripted group (container) (typed FeaturePython)
  n = 8
  ref = C_element
FEATURE [App::DocumentObjectGroupPython] H_element664  label="H_element : 429"  # scripted group (container) (typed FeaturePython)
  n = 10
  ref = H_element
FEATURE [App::DocumentObjectGroupPython] G4_XYLENE  # scripted group (container) (typed FeaturePython)
  Dunit = g/cm3
  Dvalue = 0.87
  Group = -> [C_element714,H_element664]
  conduct = 2
  density = 1
  expand = 3
  formula = G4_XYLENE
  name = G4_XYLENE
  specific = 4
FEATURE [App::DocumentObjectGroupPython] C_element715  label="C_element : 469"  # scripted group (container) (typed FeaturePython)
  n = 1
  ref = C_element
FEATURE [App::DocumentObjectGroupPython] G4_GRAPHITE  # scripted group (container) (typed FeaturePython)
  Dunit = g/cm3
  Dvalue = 2.21
  Group = -> [C_element715]
  conduct = 2
  density = 1
  expand = 3
  formula = G4_GRAPHITE
  name = G4_GRAPHITE
  specific = 4
FEATURE [App::DocumentObjectGroupPython] NIST  # scripted group (container) (typed FeaturePython)
  Group = -> [G4_A_150_TISSUE,G4_ACETONE,G4_ACETYLENE,G4_ADENINE,G4_ADIPOSE_TISSUE_ICRP,G4_AIR,G4_ALANINE,G4_ALUMINUM_OXIDE,G4_AMBER,G4_AMMONIA,G4_ANILINE,G4_ANTHRACENE,G4_B_100_BONE,G4_BAKELITE,G4_BARIUM_FLUORIDE,G4_BARIUM_SULFATE,G4_BENZENE,G4_BERYLLIUM_OXIDE,G4_BGO,G4_BLOOD_ICRP,G4_BONE_COMPACT_ICRU,G4_BONE_CORTICAL_ICRP,G4_BORON_CARBIDE,G4_BORON_OXIDE,G4_BRAIN_ICRP,G4_BUTANE,G4_N_BUTYL_ALCOHOL,G4_C_552,+152 more]
FEATURE [App::DocumentObjectGroupPython] H_element665  label="H_element : 430"  # scripted group (container) (typed FeaturePython)
  n = 1
  ref = H_element
FEATURE [App::DocumentObjectGroupPython] G4_H  # scripted group (container) (typed FeaturePython)
  Dunit = g/cm3
  Dvalue = 8.3748e-05
  Group = -> [H_element665]
  conduct = 2
  density = 1
  expand = 3
  formula = H
  name = G4_H
  specific = 4
FEATURE [App::DocumentObjectGroupPython] He_element005  label="He_element : 004"  # scripted group (container) (typed FeaturePython)
  n = 1
  ref = He_element
FEATURE [App::DocumentObjectGroupPython] G4_He  # scripted group (container) (typed FeaturePython)
  Dunit = g/cm3
  Dvalue = 0.000166322
  Group = -> [He_element005]
  conduct = 2
  density = 1
  expand = 3
  formula = He
  name = G4_He
  specific = 4
FEATURE [App::DocumentObjectGroupPython] Li_element040  label="Li_element : 038"  # scripted group (container) (typed FeaturePython)
  n = 1
  ref = Li_element
FEATURE [App::DocumentObjectGroupPython] G4_Li  # scripted group (container) (typed FeaturePython)
  Dunit = g/cm3
  Dvalue = 0.534
  Group = -> [Li_element040]
  conduct = 2
  density = 1
  expand = 3
  formula = Li
  name = G4_Li
  specific = 4
FEATURE [App::DocumentObjectGroupPython] Be_element010  label="Be_element : 009"  # scripted group (container) (typed FeaturePython)
  n = 1
  ref = Be_element
FEATURE [App::DocumentObjectGroupPython] G4_Be  # scripted group (container) (typed FeaturePython)
  Dunit = g/cm3
  Dvalue = 1.848
  Group = -> [Be_element010]
  conduct = 2
  density = 1
  expand = 3
  formula = Be
  name = G4_Be
  specific = 4
FEATURE [App::DocumentObjectGroupPython] B_element035  label="B_element : 028"  # scripted group (container) (typed FeaturePython)
  n = 1
  ref = B_element
FEATURE [App::DocumentObjectGroupPython] G4_B  # scripted group (container) (typed FeaturePython)
  Dunit = g/cm3
  Dvalue = 2.37
  Group = -> [B_element035]
  conduct = 2
  density = 1
  expand = 3
  formula = B
  name = G4_B
  specific = 4
FEATURE [App::DocumentObjectGroupPython] C_element716  label="C_element : 470"  # scripted group (container) (typed FeaturePython)
  n = 1
  ref = C_element
FEATURE [App::DocumentObjectGroupPython] G4_C  # scripted group (container) (typed FeaturePython)
  Dunit = g/cm3
  Dvalue = 2
  Group = -> [C_element716]
  conduct = 2
  density = 1
  expand = 3
  formula = C
  name = G4_C
  specific = 4
FEATURE [App::DocumentObjectGroupPython] N_element320  label="N_element : 172"  # scripted group (container) (typed FeaturePython)
  n = 1
  ref = N_element
FEATURE [App::DocumentObjectGroupPython] G4_N  # scripted group (container) (typed FeaturePython)
  Dunit = g/cm3
  Dvalue = 0.0011652
  Group = -> [N_element320]
  conduct = 2
  density = 1
  expand = 3
  formula = N
  name = G4_N
  specific = 4
FEATURE [App::DocumentObjectGroupPython] O_element625  label="O_element : 398"  # scripted group (container) (typed FeaturePython)
  n = 1
  ref = O_element
FEATURE [App::DocumentObjectGroupPython] G4_O  # scripted group (container) (typed FeaturePython)
  Dunit = g/cm3
  Dvalue = 0.00133151
  Group = -> [O_element625]
  conduct = 2
  density = 1
  expand = 3
  formula = O
  name = G4_O
  specific = 4
FEATURE [App::DocumentObjectGroupPython] F_element095  label="F_element : 047"  # scripted group (container) (typed FeaturePython)
  n = 1
  ref = F_element
FEATURE [App::DocumentObjectGroupPython] G4_F  # scripted group (container) (typed FeaturePython)
  Dunit = g/cm3
  Dvalue = 0.00158029
  Group = -> [F_element095]
  conduct = 2
  density = 1
  expand = 3
  formula = F
  name = G4_F
  specific = 4
FEATURE [App::DocumentObjectGroupPython] Ne_element005  label="Ne_element : 004"  # scripted group (container) (typed FeaturePython)
  n = 1
  ref = Ne_element
FEATURE [App::DocumentObjectGroupPython] G4_Ne  # scripted group (container) (typed FeaturePython)
  Dunit = g/cm3
  Dvalue = 0.000838505
  Group = -> [Ne_element005]
  conduct = 2
  density = 1
  expand = 3
  formula = Ne
  name = G4_Ne
  specific = 4
FEATURE [App::DocumentObjectGroupPython] Na_element100  label="Na_element : 023"  # scripted group (container) (typed FeaturePython)
  n = 1
  ref = Na_element
FEATURE [App::DocumentObjectGroupPython] G4_Na  # scripted group (container) (typed FeaturePython)
  Dunit = g/cm3
  Dvalue = 0.971
  Group = -> [Na_element100]
  conduct = 2
  density = 1
  expand = 3
  formula = Na
  name = G4_Na
  specific = 4
FEATURE [App::DocumentObjectGroupPython] Mg_element055  label="Mg_element : 024"  # scripted group (container) (typed FeaturePython)
  n = 1
  ref = Mg_element
FEATURE [App::DocumentObjectGroupPython] G4_Mg  # scripted group (container) (typed FeaturePython)
  Dunit = g/cm3
  Dvalue = 1.74
  Group = -> [Mg_element055]
  conduct = 2
  density = 1
  expand = 3
  formula = Mg
  name = G4_Mg
  specific = 4
FEATURE [App::DocumentObjectGroupPython] Al_element020  label="Al_element : 008"  # scripted group (container) (typed FeaturePython)
  n = 1
  ref = Al_element
FEATURE [App::DocumentObjectGroupPython] G4_Al  # scripted group (container) (typed FeaturePython)
  Dunit = g/cm3
  Dvalue = 2.699
  Group = -> [Al_element020]
  conduct = 2
  density = 1
  expand = 3
  formula = Al
  name = G4_Al
  specific = 4
FEATURE [App::DocumentObjectGroupPython] Si_element035  label="Si_element : 009"  # scripted group (container) (typed FeaturePython)
  n = 1
  ref = Si_element
FEATURE [App::DocumentObjectGroupPython] G4_Si  # scripted group (container) (typed FeaturePython)
  Dunit = g/cm3
  Dvalue = 2.33
  Group = -> [Si_element035]
  conduct = 2
  density = 1
  expand = 3
  formula = Si
  name = G4_Si
  specific = 4
FEATURE [App::DocumentObjectGroupPython] P_element089  label="P_element : 033"  # scripted group (container) (typed FeaturePython)
  n = 1
  ref = P_element
FEATURE [App::DocumentObjectGroupPython] G4_P  # scripted group (container) (typed FeaturePython)
  Dunit = g/cm3
  Dvalue = 2.2
  Group = -> [P_element089]
  conduct = 2
  density = 1
  expand = 3
  formula = P
  name = G4_P
  specific = 4
FEATURE [App::DocumentObjectGroupPython] S_element115  label="S_element : 034"  # scripted group (container) (typed FeaturePython)
  n = 1
  ref = S_element
FEATURE [App::DocumentObjectGroupPython] G4_S  # scripted group (container) (typed FeaturePython)
  Dunit = g/cm3
  Dvalue = 2
  Group = -> [S_element115]
  conduct = 2
  density = 1
  expand = 3
  formula = S
  name = G4_S
  specific = 4
FEATURE [App::DocumentObjectGroupPython] Cl_element149  label="Cl_element : 075"  # scripted group (container) (typed FeaturePython)
  n = 1
  ref = Cl_element
FEATURE [App::DocumentObjectGroupPython] G4_Cl  # scripted group (container) (typed FeaturePython)
  Dunit = g/cm3
  Dvalue = 0.00299473
  Group = -> [Cl_element149]
  conduct = 2
  density = 1
  expand = 3
  formula = Cl
  name = G4_Cl
  specific = 4
FEATURE [App::DocumentObjectGroupPython] Ar_element010  label="Ar_element : 004"  # scripted group (container) (typed FeaturePython)
  n = 1
  ref = Ar_element
FEATURE [App::DocumentObjectGroupPython] G4_Ar  # scripted group (container) (typed FeaturePython)
  Dunit = g/cm3
  Dvalue = 0.00166201
  Group = -> [Ar_element010]
  conduct = 2
  density = 1
  expand = 3
  formula = Ar
  name = G4_Ar
  specific = 4
FEATURE [App::DocumentObjectGroupPython] K_element065  label="K_element : 013"  # scripted group (container) (typed FeaturePython)
  n = 1
  ref = K_element
FEATURE [App::DocumentObjectGroupPython] G4_K  # scripted group (container) (typed FeaturePython)
  Dunit = g/cm3
  Dvalue = 0.862
  Group = -> [K_element065]
  conduct = 2
  density = 1
  expand = 3
  formula = K
  name = G4_K
  specific = 4
FEATURE [App::DocumentObjectGroupPython] Ca_element070  label="Ca_element : 034"  # scripted group (container) (typed FeaturePython)
  n = 1
  ref = Ca_element
FEATURE [App::DocumentObjectGroupPython] G4_Ca  # scripted group (container) (typed FeaturePython)
  Dunit = g/cm3
  Dvalue = 1.55
  Group = -> [Ca_element070]
  conduct = 2
  density = 1
  expand = 3
  formula = Ca
  name = G4_Ca
  specific = 4
FEATURE [App::DocumentObjectGroupPython] Sc_element005  label="Sc_element : 004"  # scripted group (container) (typed FeaturePython)
  n = 1
  ref = Sc_element
FEATURE [App::DocumentObjectGroupPython] G4_Sc  # scripted group (container) (typed FeaturePython)
  Dunit = g/cm3
  Dvalue = 2.989
  Group = -> [Sc_element005]
  conduct = 2
  density = 1
  expand = 3
  formula = Sc
  name = G4_Sc
  specific = 4
FEATURE [App::DocumentObjectGroupPython] Ti_element020  label="Ti_element : 009"  # scripted group (container) (typed FeaturePython)
  n = 1
  ref = Ti_element
FEATURE [App::DocumentObjectGroupPython] G4_Ti  # scripted group (container) (typed FeaturePython)
  Dunit = g/cm3
  Dvalue = 4.54
  Group = -> [Ti_element020]
  conduct = 2
  density = 1
  expand = 3
  formula = Ti
  name = G4_Ti
  specific = 4
FEATURE [App::DocumentObjectGroupPython] V_element005  label="V_element : 004"  # scripted group (container) (typed FeaturePython)
  n = 1
  ref = V_element
FEATURE [App::DocumentObjectGroupPython] G4_V  # scripted group (container) (typed FeaturePython)
  Dunit = g/cm3
  Dvalue = 6.11
  Group = -> [V_element005]
  conduct = 2
  density = 1
  expand = 3
  formula = V
  name = G4_V
  specific = 4
FEATURE [App::DocumentObjectGroupPython] Cr_element009  label="Cr_element : 023"  # scripted group (container) (typed FeaturePython)
  n = 1
  ref = Cr_element
FEATURE [App::DocumentObjectGroupPython] G4_Cr  # scripted group (container) (typed FeaturePython)
  Dunit = g/cm3
  Dvalue = 7.18
  Group = -> [Cr_element009]
  conduct = 2
  density = 1
  expand = 3
  formula = Cr
  name = G4_Cr
  specific = 4
FEATURE [App::DocumentObjectGroupPython] Mn_element005  label="Mn_element : 004"  # scripted group (container) (typed FeaturePython)
  n = 1
  ref = Mn_element
FEATURE [App::DocumentObjectGroupPython] G4_Mn  # scripted group (container) (typed FeaturePython)
  Dunit = g/cm3
  Dvalue = 7.44
  Group = -> [Mn_element005]
  conduct = 2
  density = 1
  expand = 3
  formula = Mn
  name = G4_Mn
  specific = 4
FEATURE [App::DocumentObjectGroupPython] Fe_element039  label="Fe_element : 020"  # scripted group (container) (typed FeaturePython)
  n = 1
  ref = Fe_element
FEATURE [App::DocumentObjectGroupPython] G4_Fe  # scripted group (container) (typed FeaturePython)
  Dunit = g/cm3
  Dvalue = 7.874
  Group = -> [Fe_element039]
  conduct = 2
  density = 1
  expand = 3
  formula = Fe
  name = G4_Fe
  specific = 4
FEATURE [App::DocumentObjectGroupPython] Co_element005  label="Co_element : 004"  # scripted group (container) (typed FeaturePython)
  n = 1
  ref = Co_element
FEATURE [App::DocumentObjectGroupPython] G4_Co  # scripted group (container) (typed FeaturePython)
  Dunit = g/cm3
  Dvalue = 8.9
  Group = -> [Co_element005]
  conduct = 2
  density = 1
  expand = 3
  formula = Co
  name = G4_Co
  specific = 4
FEATURE [App::DocumentObjectGroupPython] Ni_element009  label="Ni_element : 013"  # scripted group (container) (typed FeaturePython)
  n = 1
  ref = Ni_element
FEATURE [App::DocumentObjectGroupPython] G4_Ni  # scripted group (container) (typed FeaturePython)
  Dunit = g/cm3
  Dvalue = 8.902
  Group = -> [Ni_element009]
  conduct = 2
  density = 1
  expand = 3
  formula = Ni
  name = G4_Ni
  specific = 4
FEATURE [App::DocumentObjectGroupPython] Cu_element013  label="Cu_element : 096"  # scripted group (container) (typed FeaturePython)
  n = 1
  ref = Cu_element
FEATURE [App::DocumentObjectGroupPython] G4_Cu  # scripted group (container) (typed FeaturePython)
  Dunit = g/cm3
  Dvalue = 8.96
  Group = -> [Cu_element013]
  conduct = 2
  density = 1
  expand = 3
  formula = Cu
  name = G4_Cu
  specific = 4
FEATURE [App::DocumentObjectGroupPython] Zn_element013  label="Zn_element : 042"  # scripted group (container) (typed FeaturePython)
  n = 1
  ref = Zn_element
FEATURE [App::DocumentObjectGroupPython] G4_Zn  # scripted group (container) (typed FeaturePython)
  Dunit = g/cm3
  Dvalue = 7.133
  Group = -> [Zn_element013]
  conduct = 2
  density = 1
  expand = 3
  formula = Zn
  name = G4_Zn
  specific = 4
FEATURE [App::DocumentObjectGroupPython] Ga_element010  label="Ga_element : 009"  # scripted group (container) (typed FeaturePython)
  n = 1
  ref = Ga_element
FEATURE [App::DocumentObjectGroupPython] G4_Ga  # scripted group (container) (typed FeaturePython)
  Dunit = g/cm3
  Dvalue = 5.904
  Group = -> [Ga_element010]
  conduct = 2
  density = 1
  expand = 3
  formula = Ga
  name = G4_Ga
  specific = 4
FEATURE [App::DocumentObjectGroupPython] Ge_element010  label="Ge_element : 009"  # scripted group (container) (typed FeaturePython)
  n = 1
  ref = Ge_element
FEATURE [App::DocumentObjectGroupPython] G4_Ge  # scripted group (container) (typed FeaturePython)
  Dunit = g/cm3
  Dvalue = 5.323
  Group = -> [Ge_element010]
  conduct = 2
  density = 1
  expand = 3
  formula = Ge
  name = G4_Ge
  specific = 4
FEATURE [App::DocumentObjectGroupPython] As_element015  label="As_element : 009"  # scripted group (container) (typed FeaturePython)
  n = 1
  ref = As_element
FEATURE [App::DocumentObjectGroupPython] G4_As  # scripted group (container) (typed FeaturePython)
  Dunit = g/cm3
  Dvalue = 5.73
  Group = -> [As_element015]
  conduct = 2
  density = 1
  expand = 3
  formula = As
  name = G4_As
  specific = 4
FEATURE [App::DocumentObjectGroupPython] Se_element005  label="Se_element : 004"  # scripted group (container) (typed FeaturePython)
  n = 1
  ref = Se_element
FEATURE [App::DocumentObjectGroupPython] G4_Se  # scripted group (container) (typed FeaturePython)
  Dunit = g/cm3
  Dvalue = 4.5
  Group = -> [Se_element005]
  conduct = 2
  density = 1
  expand = 3
  formula = Se
  name = G4_Se
  specific = 4
FEATURE [App::DocumentObjectGroupPython] Br_element035  label="Br_element : 019"  # scripted group (container) (typed FeaturePython)
  n = 1
  ref = Br_element
FEATURE [App::DocumentObjectGroupPython] G4_Br  # scripted group (container) (typed FeaturePython)
  Dunit = g/cm3
  Dvalue = 0.0070721
  Group = -> [Br_element035]
  conduct = 2
  density = 1
  expand = 3
  formula = Br
  name = G4_Br
  specific = 4
FEATURE [App::DocumentObjectGroupPython] Kr_element005  label="Kr_element : 004"  # scripted group (container) (typed FeaturePython)
  n = 1
  ref = Kr_element
FEATURE [App::DocumentObjectGroupPython] G4_Kr  # scripted group (container) (typed FeaturePython)
  Dunit = g/cm3
  Dvalue = 0.00347832
  Group = -> [Kr_element005]
  conduct = 2
  density = 1
  expand = 3
  formula = Kr
  name = G4_Kr
  specific = 4
FEATURE [App::DocumentObjectGroupPython] Rb_element005  label="Rb_element : 004"  # scripted group (container) (typed FeaturePython)
  n = 1
  ref = Rb_element
FEATURE [App::DocumentObjectGroupPython] G4_Rb  # scripted group (container) (typed FeaturePython)
  Dunit = g/cm3
  Dvalue = 1.532
  Group = -> [Rb_element005]
  conduct = 2
  density = 1
  expand = 3
  formula = Rb
  name = G4_Rb
  specific = 4
FEATURE [App::DocumentObjectGroupPython] Sr_element005  label="Sr_element : 004"  # scripted group (container) (typed FeaturePython)
  n = 1
  ref = Sr_element
FEATURE [App::DocumentObjectGroupPython] G4_Sr  # scripted group (container) (typed FeaturePython)
  Dunit = g/cm3
  Dvalue = 2.54
  Group = -> [Sr_element005]
  conduct = 2
  density = 1
  expand = 3
  formula = Sr
  name = G4_Sr
  specific = 4
FEATURE [App::DocumentObjectGroupPython] Y_element005  label="Y_element : 004"  # scripted group (container) (typed FeaturePython)
  n = 1
  ref = Y_element
FEATURE [App::DocumentObjectGroupPython] G4_Y  # scripted group (container) (typed FeaturePython)
  Dunit = g/cm3
  Dvalue = 4.469
  Group = -> [Y_element005]
  conduct = 2
  density = 1
  expand = 3
  formula = Y
  name = G4_Y
  specific = 4
FEATURE [App::DocumentObjectGroupPython] Zr_element005  label="Zr_element : 004"  # scripted group (container) (typed FeaturePython)
  n = 1
  ref = Zr_element
FEATURE [App::DocumentObjectGroupPython] G4_Zr  # scripted group (container) (typed FeaturePython)
  Dunit = g/cm3
  Dvalue = 6.506
  Group = -> [Zr_element005]
  conduct = 2
  density = 1
  expand = 3
  formula = Zr
  name = G4_Zr
  specific = 4
FEATURE [App::DocumentObjectGroupPython] Nb_element005  label="Nb_element : 004"  # scripted group (container) (typed FeaturePython)
  n = 1
  ref = Nb_element
FEATURE [App::DocumentObjectGroupPython] G4_Nb  # scripted group (container) (typed FeaturePython)
  Dunit = g/cm3
  Dvalue = 8.57
  Group = -> [Nb_element005]
  conduct = 2
  density = 1
  expand = 3
  formula = Nb
  name = G4_Nb
  specific = 4
FEATURE [App::DocumentObjectGroupPython] Mo_element005  label="Mo_element : 004"  # scripted group (container) (typed FeaturePython)
  n = 1
  ref = Mo_element
FEATURE [App::DocumentObjectGroupPython] G4_Mo  # scripted group (container) (typed FeaturePython)
  Dunit = g/cm3
  Dvalue = 10.22
  Group = -> [Mo_element005]
  conduct = 2
  density = 1
  expand = 3
  formula = Mo
  name = G4_Mo
  specific = 4
FEATURE [App::DocumentObjectGroupPython] Tc_element005  label="Tc_element : 004"  # scripted group (container) (typed FeaturePython)
  n = 1
  ref = Tc_element
FEATURE [App::DocumentObjectGroupPython] G4_Tc  # scripted group (container) (typed FeaturePython)
  Dunit = g/cm3
  Dvalue = 11.5
  Group = -> [Tc_element005]
  conduct = 2
  density = 1
  expand = 3
  formula = Tc
  name = G4_Tc
  specific = 4
FEATURE [App::DocumentObjectGroupPython] Ru_element005  label="Ru_element : 004"  # scripted group (container) (typed FeaturePython)
  n = 1
  ref = Ru_element
FEATURE [App::DocumentObjectGroupPython] G4_Ru  # scripted group (container) (typed FeaturePython)
  Dunit = g/cm3
  Dvalue = 12.41
  Group = -> [Ru_element005]
  conduct = 2
  density = 1
  expand = 3
  formula = Ru
  name = G4_Ru
  specific = 4
FEATURE [App::DocumentObjectGroupPython] Rh_element005  label="Rh_element : 004"  # scripted group (container) (typed FeaturePython)
  n = 1
  ref = Rh_element
FEATURE [App::DocumentObjectGroupPython] G4_Rh  # scripted group (container) (typed FeaturePython)
  Dunit = g/cm3
  Dvalue = 12.41
  Group = -> [Rh_element005]
  conduct = 2
  density = 1
  expand = 3
  formula = Rh
  name = G4_Rh
  specific = 4
FEATURE [App::DocumentObjectGroupPython] Pd_element005  label="Pd_element : 004"  # scripted group (container) (typed FeaturePython)
  n = 1
  ref = Pd_element
FEATURE [App::DocumentObjectGroupPython] G4_Pd  # scripted group (container) (typed FeaturePython)
  Dunit = g/cm3
  Dvalue = 12.02
  Group = -> [Pd_element005]
  conduct = 2
  density = 1
  expand = 3
  formula = Pd
  name = G4_Pd
  specific = 4
FEATURE [App::DocumentObjectGroupPython] Ag_element030  label="Ag_element : 019"  # scripted group (container) (typed FeaturePython)
  n = 1
  ref = Ag_element
FEATURE [App::DocumentObjectGroupPython] G4_Ag  # scripted group (container) (typed FeaturePython)
  Dunit = g/cm3
  Dvalue = 10.5
  Group = -> [Ag_element030]
  conduct = 2
  density = 1
  expand = 3
  formula = Ag
  name = G4_Ag
  specific = 4
FEATURE [App::DocumentObjectGroupPython] Cd_element015  label="Cd_element : 014"  # scripted group (container) (typed FeaturePython)
  n = 1
  ref = Cd_element
FEATURE [App::DocumentObjectGroupPython] G4_Cd  # scripted group (container) (typed FeaturePython)
  Dunit = g/cm3
  Dvalue = 8.65
  Group = -> [Cd_element015]
  conduct = 2
  density = 1
  expand = 3
  formula = Cd
  name = G4_Cd
  specific = 4
FEATURE [App::DocumentObjectGroupPython] In_element005  label="In_element : 004"  # scripted group (container) (typed FeaturePython)
  n = 1
  ref = In_element
FEATURE [App::DocumentObjectGroupPython] G4_In  # scripted group (container) (typed FeaturePython)
  Dunit = g/cm3
  Dvalue = 7.31
  Group = -> [In_element005]
  conduct = 2
  density = 1
  expand = 3
  formula = In
  name = G4_In
  specific = 4
FEATURE [App::DocumentObjectGroupPython] Sn_element005  label="Sn_element : 004"  # scripted group (container) (typed FeaturePython)
  n = 1
  ref = Sn_element
FEATURE [App::DocumentObjectGroupPython] G4_Sn  # scripted group (container) (typed FeaturePython)
  Dunit = g/cm3
  Dvalue = 7.31
  Group = -> [Sn_element005]
  conduct = 2
  density = 1
  expand = 3
  formula = Sn
  name = G4_Sn
  specific = 4
FEATURE [App::DocumentObjectGroupPython] Sb_element005  label="Sb_element : 004"  # scripted group (container) (typed FeaturePython)
  n = 1
  ref = Sb_element
FEATURE [App::DocumentObjectGroupPython] G4_Sb  # scripted group (container) (typed FeaturePython)
  Dunit = g/cm3
  Dvalue = 6.691
  Group = -> [Sb_element005]
  conduct = 2
  density = 1
  expand = 3
  formula = Sb
  name = G4_Sb
  specific = 4
FEATURE [App::DocumentObjectGroupPython] Te_element010  label="Te_element : 009"  # scripted group (container) (typed FeaturePython)
  n = 1
  ref = Te_element
FEATURE [App::DocumentObjectGroupPython] G4_Te  # scripted group (container) (typed FeaturePython)
  Dunit = g/cm3
  Dvalue = 6.24
  Group = -> [Te_element010]
  conduct = 2
  density = 1
  expand = 3
  formula = Te
  name = G4_Te
  specific = 4
FEATURE [App::DocumentObjectGroupPython] I_element050  label="I_element : 032"  # scripted group (container) (typed FeaturePython)
  n = 1
  ref = I_element
FEATURE [App::DocumentObjectGroupPython] G4_I  # scripted group (container) (typed FeaturePython)
  Dunit = g/cm3
  Dvalue = 4.93
  Group = -> [I_element050]
  conduct = 2
  density = 1
  expand = 3
  formula = I
  name = G4_I
  specific = 4
FEATURE [App::DocumentObjectGroupPython] Xe_element005  label="Xe_element : 004"  # scripted group (container) (typed FeaturePython)
  n = 1
  ref = Xe_element
FEATURE [App::DocumentObjectGroupPython] G4_Xe  # scripted group (container) (typed FeaturePython)
  Dunit = g/cm3
  Dvalue = 0.00548536
  Group = -> [Xe_element005]
  conduct = 2
  density = 1
  expand = 3
  formula = Xe
  name = G4_Xe
  specific = 4
FEATURE [App::DocumentObjectGroupPython] Cs_element015  label="Cs_element : 014"  # scripted group (container) (typed FeaturePython)
  n = 1
  ref = Cs_element
FEATURE [App::DocumentObjectGroupPython] G4_Cs  # scripted group (container) (typed FeaturePython)
  Dunit = g/cm3
  Dvalue = 1.873
  Group = -> [Cs_element015]
  conduct = 2
  density = 1
  expand = 3
  formula = Cs
  name = G4_Cs
  specific = 4
FEATURE [App::DocumentObjectGroupPython] Ba_element015  label="Ba_element : 014"  # scripted group (container) (typed FeaturePython)
  n = 1
  ref = Ba_element
FEATURE [App::DocumentObjectGroupPython] G4_Ba  # scripted group (container) (typed FeaturePython)
  Dunit = g/cm3
  Dvalue = 3.5
  Group = -> [Ba_element015]
  conduct = 2
  density = 1
  expand = 3
  formula = Ba
  name = G4_Ba
  specific = 4
FEATURE [App::DocumentObjectGroupPython] La_element015  label="La_element : 013"  # scripted group (container) (typed FeaturePython)
  n = 1
  ref = La_element
FEATURE [App::DocumentObjectGroupPython] G4_La  # scripted group (container) (typed FeaturePython)
  Dunit = g/cm3
  Dvalue = 6.154
  Group = -> [La_element015]
  conduct = 2
  density = 1
  expand = 3
  formula = La
  name = G4_La
  specific = 4
FEATURE [App::DocumentObjectGroupPython] Ce_element010  label="Ce_element : 004"  # scripted group (container) (typed FeaturePython)
  n = 1
  ref = Ce_element
FEATURE [App::DocumentObjectGroupPython] G4_Ce  # scripted group (container) (typed FeaturePython)
  Dunit = g/cm3
  Dvalue = 6.657
  Group = -> [Ce_element010]
  conduct = 2
  density = 1
  expand = 3
  formula = Ce
  name = G4_Ce
  specific = 4
FEATURE [App::DocumentObjectGroupPython] Pr_element005  label="Pr_element : 004"  # scripted group (container) (typed FeaturePython)
  n = 1
  ref = Pr_element
FEATURE [App::DocumentObjectGroupPython] G4_Pr  # scripted group (container) (typed FeaturePython)
  Dunit = g/cm3
  Dvalue = 6.71
  Group = -> [Pr_element005]
  conduct = 2
  density = 1
  expand = 3
  formula = Pr
  name = G4_Pr
  specific = 4
FEATURE [App::DocumentObjectGroupPython] Nd_element005  label="Nd_element : 004"  # scripted group (container) (typed FeaturePython)
  n = 1
  ref = Nd_element
FEATURE [App::DocumentObjectGroupPython] G4_Nd  # scripted group (container) (typed FeaturePython)
  Dunit = g/cm3
  Dvalue = 6.9
  Group = -> [Nd_element005]
  conduct = 2
  density = 1
  expand = 3
  formula = Nd
  name = G4_Nd
  specific = 4
FEATURE [App::DocumentObjectGroupPython] Pm_element005  label="Pm_element : 004"  # scripted group (container) (typed FeaturePython)
  n = 1
  ref = Pm_element
FEATURE [App::DocumentObjectGroupPython] G4_Pm  # scripted group (container) (typed FeaturePython)
  Dunit = g/cm3
  Dvalue = 7.22
  Group = -> [Pm_element005]
  conduct = 2
  density = 1
  expand = 3
  formula = Pm
  name = G4_Pm
  specific = 4
FEATURE [App::DocumentObjectGroupPython] Sm_element005  label="Sm_element : 004"  # scripted group (container) (typed FeaturePython)
  n = 1
  ref = Sm_element
FEATURE [App::DocumentObjectGroupPython] G4_Sm  # scripted group (container) (typed FeaturePython)
  Dunit = g/cm3
  Dvalue = 7.46
  Group = -> [Sm_element005]
  conduct = 2
  density = 1
  expand = 3
  formula = Sm
  name = G4_Sm
  specific = 4
FEATURE [App::DocumentObjectGroupPython] Eu_element005  label="Eu_element : 004"  # scripted group (container) (typed FeaturePython)
  n = 1
  ref = Eu_element
FEATURE [App::DocumentObjectGroupPython] G4_Eu  # scripted group (container) (typed FeaturePython)
  Dunit = g/cm3
  Dvalue = 5.243
  Group = -> [Eu_element005]
  conduct = 2
  density = 1
  expand = 3
  formula = Eu
  name = G4_Eu
  specific = 4
FEATURE [App::DocumentObjectGroupPython] Gd_element010  label="Gd_element : 008"  # scripted group (container) (typed FeaturePython)
  n = 1
  ref = Gd_element
FEATURE [App::DocumentObjectGroupPython] G4_Gd  # scripted group (container) (typed FeaturePython)
  Dunit = g/cm3
  Dvalue = 7.9004
  Group = -> [Gd_element010]
  conduct = 2
  density = 1
  expand = 3
  formula = Gd
  name = G4_Gd
  specific = 4
FEATURE [App::DocumentObjectGroupPython] Tb_element005  label="Tb_element : 004"  # scripted group (container) (typed FeaturePython)
  n = 1
  ref = Tb_element
FEATURE [App::DocumentObjectGroupPython] G4_Tb  # scripted group (container) (typed FeaturePython)
  Dunit = g/cm3
  Dvalue = 8.229
  Group = -> [Tb_element005]
  conduct = 2
  density = 1
  expand = 3
  formula = Tb
  name = G4_Tb
  specific = 4
FEATURE [App::DocumentObjectGroupPython] Dy_element005  label="Dy_element : 004"  # scripted group (container) (typed FeaturePython)
  n = 1
  ref = Dy_element
FEATURE [App::DocumentObjectGroupPython] G4_Dy  # scripted group (container) (typed FeaturePython)
  Dunit = g/cm3
  Dvalue = 8.55
  Group = -> [Dy_element005]
  conduct = 2
  density = 1
  expand = 3
  formula = Dy
  name = G4_Dy
  specific = 4
FEATURE [App::DocumentObjectGroupPython] Ho_element005  label="Ho_element : 004"  # scripted group (container) (typed FeaturePython)
  n = 1
  ref = Ho_element
FEATURE [App::DocumentObjectGroupPython] G4_Ho  # scripted group (container) (typed FeaturePython)
  Dunit = g/cm3
  Dvalue = 8.795
  Group = -> [Ho_element005]
  conduct = 2
  density = 1
  expand = 3
  formula = Ho
  name = G4_Ho
  specific = 4
FEATURE [App::DocumentObjectGroupPython] Er_element005  label="Er_element : 004"  # scripted group (container) (typed FeaturePython)
  n = 1
  ref = Er_element
FEATURE [App::DocumentObjectGroupPython] G4_Er  # scripted group (container) (typed FeaturePython)
  Dunit = g/cm3
  Dvalue = 9.066
  Group = -> [Er_element005]
  conduct = 2
  density = 1
  expand = 3
  formula = Er
  name = G4_Er
  specific = 4
FEATURE [App::DocumentObjectGroupPython] Tm_element005  label="Tm_element : 004"  # scripted group (container) (typed FeaturePython)
  n = 1
  ref = Tm_element
FEATURE [App::DocumentObjectGroupPython] G4_Tm  # scripted group (container) (typed FeaturePython)
  Dunit = g/cm3
  Dvalue = 9.321
  Group = -> [Tm_element005]
  conduct = 2
  density = 1
  expand = 3
  formula = Tm
  name = G4_Tm
  specific = 4
FEATURE [App::DocumentObjectGroupPython] Yb_element005  label="Yb_element : 004"  # scripted group (container) (typed FeaturePython)
  n = 1
  ref = Yb_element
FEATURE [App::DocumentObjectGroupPython] G4_Yb  # scripted group (container) (typed FeaturePython)
  Dunit = g/cm3
  Dvalue = 6.73
  Group = -> [Yb_element005]
  conduct = 2
  density = 1
  expand = 3
  formula = Yb
  name = G4_Yb
  specific = 4
FEATURE [App::DocumentObjectGroupPython] Lu_element005  label="Lu_element : 004"  # scripted group (container) (typed FeaturePython)
  n = 1
  ref = Lu_element
FEATURE [App::DocumentObjectGroupPython] G4_Lu  # scripted group (container) (typed FeaturePython)
  Dunit = g/cm3
  Dvalue = 9.84
  Group = -> [Lu_element005]
  conduct = 2
  density = 1
  expand = 3
  formula = Lu
  name = G4_Lu
  specific = 4
FEATURE [App::DocumentObjectGroupPython] Hf_element005  label="Hf_element : 004"  # scripted group (container) (typed FeaturePython)
  n = 1
  ref = Hf_element
FEATURE [App::DocumentObjectGroupPython] G4_Hf  # scripted group (container) (typed FeaturePython)
  Dunit = g/cm3
  Dvalue = 13.31
  Group = -> [Hf_element005]
  conduct = 2
  density = 1
  expand = 3
  formula = Hf
  name = G4_Hf
  specific = 4
FEATURE [App::DocumentObjectGroupPython] Ta_element005  label="Ta_element : 004"  # scripted group (container) (typed FeaturePython)
  n = 1
  ref = Ta_element
FEATURE [App::DocumentObjectGroupPython] G4_Ta  # scripted group (container) (typed FeaturePython)
  Dunit = g/cm3
  Dvalue = 16.654
  Group = -> [Ta_element005]
  conduct = 2
  density = 1
  expand = 3
  formula = Ta
  name = G4_Ta
  specific = 4
FEATURE [App::DocumentObjectGroupPython] W_element024  label="W_element : 023"  # scripted group (container) (typed FeaturePython)
  n = 1
  ref = W_element
FEATURE [App::DocumentObjectGroupPython] G4_W  # scripted group (container) (typed FeaturePython)
  Dunit = g/cm3
  Dvalue = 19.3
  Group = -> [W_element024]
  conduct = 2
  density = 1
  expand = 3
  formula = W
  name = G4_W
  specific = 4
FEATURE [App::DocumentObjectGroupPython] Re_element005  label="Re_element : 004"  # scripted group (container) (typed FeaturePython)
  n = 1
  ref = Re_element
FEATURE [App::DocumentObjectGroupPython] G4_Re  # scripted group (container) (typed FeaturePython)
  Dunit = g/cm3
  Dvalue = 21.02
  Group = -> [Re_element005]
  conduct = 2
  density = 1
  expand = 3
  formula = Re
  name = G4_Re
  specific = 4
FEATURE [App::DocumentObjectGroupPython] Os_element005  label="Os_element : 004"  # scripted group (container) (typed FeaturePython)
  n = 1
  ref = Os_element
FEATURE [App::DocumentObjectGroupPython] G4_Os  # scripted group (container) (typed FeaturePython)
  Dunit = g/cm3
  Dvalue = 22.57
  Group = -> [Os_element005]
  conduct = 2
  density = 1
  expand = 3
  formula = Os
  name = G4_Os
  specific = 4
FEATURE [App::DocumentObjectGroupPython] Ir_element005  label="Ir_element : 004"  # scripted group (container) (typed FeaturePython)
  n = 1
  ref = Ir_element
FEATURE [App::DocumentObjectGroupPython] G4_Ir  # scripted group (container) (typed FeaturePython)
  Dunit = g/cm3
  Dvalue = 22.42
  Group = -> [Ir_element005]
  conduct = 2
  density = 1
  expand = 3
  formula = Ir
  name = G4_Ir
  specific = 4
FEATURE [App::DocumentObjectGroupPython] Pt_element005  label="Pt_element : 004"  # scripted group (container) (typed FeaturePython)
  n = 1
  ref = Pt_element
FEATURE [App::DocumentObjectGroupPython] G4_Pt  # scripted group (container) (typed FeaturePython)
  Dunit = g/cm3
  Dvalue = 21.45
  Group = -> [Pt_element005]
  conduct = 2
  density = 1
  expand = 3
  formula = Pt
  name = G4_Pt
  specific = 4
FEATURE [App::DocumentObjectGroupPython] Au_element005  label="Au_element : 004"  # scripted group (container) (typed FeaturePython)
  n = 1
  ref = Au_element
FEATURE [App::DocumentObjectGroupPython] G4_Au  # scripted group (container) (typed FeaturePython)
  Dunit = g/cm3
  Dvalue = 19.32
  Group = -> [Au_element005]
  conduct = 2
  density = 1
  expand = 3
  formula = Au
  name = G4_Au
  specific = 4
FEATURE [App::DocumentObjectGroupPython] Hg_element010  label="Hg_element : 009"  # scripted group (container) (typed FeaturePython)
  n = 1
  ref = Hg_element
FEATURE [App::DocumentObjectGroupPython] G4_Hg  # scripted group (container) (typed FeaturePython)
  Dunit = g/cm3
  Dvalue = 13.546
  Group = -> [Hg_element010]
  conduct = 2
  density = 1
  expand = 3
  formula = Hg
  name = G4_Hg
  specific = 4
FEATURE [App::DocumentObjectGroupPython] Tl_element010  label="Tl_element : 009"  # scripted group (container) (typed FeaturePython)
  n = 1
  ref = Tl_element
FEATURE [App::DocumentObjectGroupPython] G4_Tl  # scripted group (container) (typed FeaturePython)
  Dunit = g/cm3
  Dvalue = 11.72
  Group = -> [Tl_element010]
  conduct = 2
  density = 1
  expand = 3
  formula = Tl
  name = G4_Tl
  specific = 4
FEATURE [App::DocumentObjectGroupPython] Pb_element027  label="Pb_element : 012"  # scripted group (container) (typed FeaturePython)
  n = 1
  ref = Pb_element
FEATURE [App::DocumentObjectGroupPython] G4_Pb  # scripted group (container) (typed FeaturePython)
  Dunit = g/cm3
  Dvalue = 11.35
  Group = -> [Pb_element027]
  conduct = 2
  density = 1
  expand = 3
  formula = Pb
  name = G4_Pb
  specific = 4
FEATURE [App::DocumentObjectGroupPython] Bi_element010  label="Bi_element : 010"  # scripted group (container) (typed FeaturePython)
  n = 1
  ref = Bi_element
FEATURE [App::DocumentObjectGroupPython] G4_Bi  # scripted group (container) (typed FeaturePython)
  Dunit = g/cm3
  Dvalue = 9.747
  Group = -> [Bi_element010]
  conduct = 2
  density = 1
  expand = 3
  formula = Bi
  name = G4_Bi
  specific = 4
FEATURE [App::DocumentObjectGroupPython] Po_element005  label="Po_element : 004"  # scripted group (container) (typed FeaturePython)
  n = 1
  ref = Po_element
FEATURE [App::DocumentObjectGroupPython] G4_Po  # scripted group (container) (typed FeaturePython)
  Dunit = g/cm3
  Dvalue = 9.32
  Group = -> [Po_element005]
  conduct = 2
  density = 1
  expand = 3
  formula = Po
  name = G4_Po
  specific = 4
FEATURE [App::DocumentObjectGroupPython] At_element005  label="At_element : 004"  # scripted group (container) (typed FeaturePython)
  n = 1
  ref = At_element
FEATURE [App::DocumentObjectGroupPython] G4_At  # scripted group (container) (typed FeaturePython)
  Dunit = g/cm3
  Dvalue = 9.32
  Group = -> [At_element005]
  conduct = 2
  density = 1
  expand = 3
  formula = At
  name = G4_At
  specific = 4
FEATURE [App::DocumentObjectGroupPython] Rn_element005  label="Rn_element : 004"  # scripted group (container) (typed FeaturePython)
  n = 1
  ref = Rn_element
FEATURE [App::DocumentObjectGroupPython] G4_Rn  # scripted group (container) (typed FeaturePython)
  Dunit = g/cm3
  Dvalue = 0.00900662
  Group = -> [Rn_element005]
  conduct = 2
  density = 1
  expand = 3
  formula = Rn
  name = G4_Rn
  specific = 4
FEATURE [App::DocumentObjectGroupPython] Fr_element005  label="Fr_element : 004"  # scripted group (container) (typed FeaturePython)
  n = 1
  ref = Fr_element
FEATURE [App::DocumentObjectGroupPython] G4_Fr  # scripted group (container) (typed FeaturePython)
  Dunit = g/cm3
  Dvalue = 1
  Group = -> [Fr_element005]
  conduct = 2
  density = 1
  expand = 3
  formula = Fr
  name = G4_Fr
  specific = 4
FEATURE [App::DocumentObjectGroupPython] Ra_element005  label="Ra_element : 004"  # scripted group (container) (typed FeaturePython)
  n = 1
  ref = Ra_element
FEATURE [App::DocumentObjectGroupPython] G4_Ra  # scripted group (container) (typed FeaturePython)
  Dunit = g/cm3
  Dvalue = 5
  Group = -> [Ra_element005]
  conduct = 2
  density = 1
  expand = 3
  formula = Ra
  name = G4_Ra
  specific = 4
FEATURE [App::DocumentObjectGroupPython] Ac_element005  label="Ac_element : 004"  # scripted group (container) (typed FeaturePython)
  n = 1
  ref = Ac_element
FEATURE [App::DocumentObjectGroupPython] G4_Ac  # scripted group (container) (typed FeaturePython)
  Dunit = g/cm3
  Dvalue = 10.07
  Group = -> [Ac_element005]
  conduct = 2
  density = 1
  expand = 3
  formula = Ac
  name = G4_Ac
  specific = 4
FEATURE [App::DocumentObjectGroupPython] Th_element005  label="Th_element : 004"  # scripted group (container) (typed FeaturePython)
  n = 1
  ref = Th_element
FEATURE [App::DocumentObjectGroupPython] G4_Th  # scripted group (container) (typed FeaturePython)
  Dunit = g/cm3
  Dvalue = 11.72
  Group = -> [Th_element005]
  conduct = 2
  density = 1
  expand = 3
  formula = Th
  name = G4_Th
  specific = 4
FEATURE [App::DocumentObjectGroupPython] Pa_element005  label="Pa_element : 004"  # scripted group (container) (typed FeaturePython)
  n = 1
  ref = Pa_element
FEATURE [App::DocumentObjectGroupPython] G4_Pa  # scripted group (container) (typed FeaturePython)
  Dunit = g/cm3
  Dvalue = 15.37
  Group = -> [Pa_element005]
  conduct = 2
  density = 1
  expand = 3
  formula = Pa
  name = G4_Pa
  specific = 4
FEATURE [App::DocumentObjectGroupPython] U_element020  label="U_element : 019"  # scripted group (container) (typed FeaturePython)
  n = 1
  ref = U_element
FEATURE [App::DocumentObjectGroupPython] G4_U  # scripted group (container) (typed FeaturePython)
  Dunit = g/cm3
  Dvalue = 18.95
  Group = -> [U_element020]
  conduct = 2
  density = 1
  expand = 3
  formula = U
  name = G4_U
  specific = 4
FEATURE [App::DocumentObjectGroupPython] Np_element005  label="Np_element : 004"  # scripted group (container) (typed FeaturePython)
  n = 1
  ref = Np_element
FEATURE [App::DocumentObjectGroupPython] G4_Np  # scripted group (container) (typed FeaturePython)
  Dunit = g/cm3
  Dvalue = 20.25
  Group = -> [Np_element005]
  conduct = 2
  density = 1
  expand = 3
  formula = Np
  name = G4_Np
  specific = 4
FEATURE [App::DocumentObjectGroupPython] Pu_element010  label="Pu_element : 009"  # scripted group (container) (typed FeaturePython)
  n = 1
  ref = Pu_element
FEATURE [App::DocumentObjectGroupPython] G4_Pu  # scripted group (container) (typed FeaturePython)
  Dunit = g/cm3
  Dvalue = 19.84
  Group = -> [Pu_element010]
  conduct = 2
  density = 1
  expand = 3
  formula = Pu
  name = G4_Pu
  specific = 4
FEATURE [App::DocumentObjectGroupPython] Am_element005  label="Am_element : 004"  # scripted group (container) (typed FeaturePython)
  n = 1
  ref = Am_element
FEATURE [App::DocumentObjectGroupPython] G4_Am  # scripted group (container) (typed FeaturePython)
  Dunit = g/cm3
  Dvalue = 13.67
  Group = -> [Am_element005]
  conduct = 2
  density = 1
  expand = 3
  formula = Am
  name = G4_Am
  specific = 4
FEATURE [App::DocumentObjectGroupPython] Cm_element005  label="Cm_element : 004"  # scripted group (container) (typed FeaturePython)
  n = 1
  ref = Cm_element
FEATURE [App::DocumentObjectGroupPython] G4_Cm  # scripted group (container) (typed FeaturePython)
  Dunit = g/cm3
  Dvalue = 13.51
  Group = -> [Cm_element005]
  conduct = 2
  density = 1
  expand = 3
  formula = Cm
  name = G4_Cm
  specific = 4
FEATURE [App::DocumentObjectGroupPython] Bk_element005  label="Bk_element : 004"  # scripted group (container) (typed FeaturePython)
  n = 1
  ref = Bk_element
FEATURE [App::DocumentObjectGroupPython] G4_Bk  # scripted group (container) (typed FeaturePython)
  Dunit = g/cm3
  Dvalue = 14
  Group = -> [Bk_element005]
  conduct = 2
  density = 1
  expand = 3
  formula = Bk
  name = G4_Bk
  specific = 4
FEATURE [App::DocumentObjectGroupPython] Cf_element005  label="Cf_element : 004"  # scripted group (container) (typed FeaturePython)
  n = 1
  ref = Cf_element
FEATURE [App::DocumentObjectGroupPython] G4_Cf  # scripted group (container) (typed FeaturePython)
  Dunit = g/cm3
  Dvalue = 10
  Group = -> [Cf_element005]
  conduct = 2
  density = 1
  expand = 3
  formula = Cf
  name = G4_Cf
  specific = 4
FEATURE [App::DocumentObjectGroupPython] Element  # scripted group (container) (typed FeaturePython)
  Group = -> [G4_H,G4_He,G4_Li,G4_Be,G4_B,G4_C,G4_N,G4_O,G4_F,G4_Ne,G4_Na,G4_Mg,G4_Al,G4_Si,G4_P,G4_S,G4_Cl,G4_Ar,G4_K,G4_Ca,G4_Sc,G4_Ti,G4_V,G4_Cr,G4_Mn,G4_Fe,G4_Co,G4_Ni,G4_Cu,G4_Zn,G4_Ga,G4_Ge,G4_As,G4_Se,G4_Br,G4_Kr,G4_Rb,G4_Sr,G4_Y,G4_Zr,G4_Nb,G4_Mo,G4_Tc,G4_Ru,G4_Rh,G4_Pd,G4_Ag,G4_Cd,G4_In,G4_Sn,G4_Sb,G4_Te,G4_I,G4_Xe,G4_Cs,G4_Ba,G4_La,G4_Ce,G4_Pr,G4_Nd,G4_Pm,G4_Sm,G4_Eu,G4_Gd,G4_Tb,G4_Dy,G4_Ho,G4_Er,+30 more]
FEATURE [App::DocumentObjectGroupPython] H_element666  label="H_element : 431"  # scripted group (container) (typed FeaturePython)
  n = 2
  ref = H_element
FEATURE [App::DocumentObjectGroupPython] G4_lH2  # scripted group (container) (typed FeaturePython)
  Dunit = g/cm3
  Dvalue = 0.0708
  Group = -> [H_element666]
  conduct = 2
  density = 1
  expand = 3
  formula = G4_lH2
  name = G4_lH2
  specific = 4
FEATURE [App::DocumentObjectGroupPython] N_element321  label="N_element : 173"  # scripted group (container) (typed FeaturePython)
  n = 2
  ref = N_element
FEATURE [App::DocumentObjectGroupPython] G4_lN2  # scripted group (container) (typed FeaturePython)
  Dunit = g/cm3
  Dvalue = 0.807
  Group = -> [N_element321]
  conduct = 2
  density = 1
  expand = 3
  formula = G4_lN2
  name = G4_lN2
  specific = 4
FEATURE [App::DocumentObjectGroupPython] O_element626  label="O_element : 399"  # scripted group (container) (typed FeaturePython)
  n = 2
  ref = O_element
FEATURE [App::DocumentObjectGroupPython] G4_lO2  # scripted group (container) (typed FeaturePython)
  Dunit = g/cm3
  Dvalue = 1.141
  Group = -> [O_element626]
  conduct = 2
  density = 1
  expand = 3
  formula = G4_lO2
  name = G4_lO2
  specific = 4
FEATURE [App::DocumentObjectGroupPython] Ar003  label="Ar : 004"  # scripted group (container) (typed FeaturePython)
  n = 1
  ref = Ar
FEATURE [App::DocumentObjectGroupPython] G4_lAr  # scripted group (container) (typed FeaturePython)
  Dunit = g/cm3
  Dvalue = 1.396
  Group = -> [Ar003]
  conduct = 2
  density = 1
  expand = 3
  formula = G4_lAr
  name = G4_lAr
  specific = 4
FEATURE [App::DocumentObjectGroupPython] Br003  label="Br : 004"  # scripted group (container) (typed FeaturePython)
  n = 1
  ref = Br
FEATURE [App::DocumentObjectGroupPython] G4_lBr  # scripted group (container) (typed FeaturePython)
  Dunit = g/cm3
  Dvalue = 3.1028
  Group = -> [Br003]
  conduct = 2
  density = 1
  expand = 3
  formula = G4_lBr
  name = G4_lBr
  specific = 4
FEATURE [App::DocumentObjectGroupPython] Kr003  label="Kr : 004"  # scripted group (container) (typed FeaturePython)
  n = 1
  ref = Kr
FEATURE [App::DocumentObjectGroupPython] G4_lKr  # scripted group (container) (typed FeaturePython)
  Dunit = g/cm3
  Dvalue = 2.418
  Group = -> [Kr003]
  conduct = 2
  density = 1
  expand = 3
  formula = G4_lKr
  name = G4_lKr
  specific = 4
FEATURE [App::DocumentObjectGroupPython] Xe003  label="Xe : 004"  # scripted group (container) (typed FeaturePython)
  n = 1
  ref = Xe
FEATURE [App::DocumentObjectGroupPython] G4_lXe  # scripted group (container) (typed FeaturePython)
  Dunit = g/cm3
  Dvalue = 2.953
  Group = -> [Xe003]
  conduct = 2
  density = 1
  expand = 3
  formula = G4_lXe
  name = G4_lXe
  specific = 4
FEATURE [App::DocumentObjectGroupPython] O_element627  label="O_element : 400"  # scripted group (container) (typed FeaturePython)
  n = 4
  ref = O_element
FEATURE [App::DocumentObjectGroupPython] Pb_element028  label="Pb_element : 013"  # scripted group (container) (typed FeaturePython)
  n = 1
  ref = Pb_element
FEATURE [App::DocumentObjectGroupPython] W_element025  label="W_element : 024"  # scripted group (container) (typed FeaturePython)
  n = 1
  ref = W_element
FEATURE [App::DocumentObjectGroupPython] G4_PbWO4  # scripted group (container) (typed FeaturePython)
  Dunit = g/cm3
  Dvalue = 8.28
  Group = -> [O_element627,Pb_element028,W_element025]
  conduct = 2
  density = 1
  expand = 3
  formula = G4_PbWO4
  name = G4_PbWO4
  specific = 4
FEATURE [App::DocumentObjectGroupPython] alactic003  label="alactic : 004"  # scripted group (container) (typed FeaturePython)
  n = 1
  ref = alactic
FEATURE [App::DocumentObjectGroupPython] G4_Galactic  # scripted group (container) (typed FeaturePython)
  Dunit = g/cm3
  Dvalue = 0
  Group = -> [alactic003]
  conduct = 2
  density = 1
  expand = 3
  formula = G4_Galactic
  name = G4_Galactic
  specific = 4
FEATURE [App::DocumentObjectGroupPython] RAPHITE_POROUS003  label="RAPHITE_POROUS : 004"  # scripted group (container) (typed FeaturePython)
  n = 1
  ref = RAPHITE_POROUS
FEATURE [App::DocumentObjectGroupPython] G4_GRAPHITE_POROUS  # scripted group (container) (typed FeaturePython)
  Dunit = g/cm3
  Dvalue = 1.7
  Group = -> [RAPHITE_POROUS003]
  conduct = 2
  density = 1
  expand = 3
  formula = G4_GRAPHITE_POROUS
  name = G4_GRAPHITE_POROUS
  specific = 4
FEATURE [App::DocumentObjectGroupPython] H_element667  label="H_element : 0.286"  # scripted group (container) (typed FeaturePython)
  n = 0.080538
FEATURE [App::DocumentObjectGroupPython] C_element717  label="C_element : 0.1017"  # scripted group (container) (typed FeaturePython)
  n = 0.599848
FEATURE [App::DocumentObjectGroupPython] O_element628  label="O_element : 0.1007"  # scripted group (container) (typed FeaturePython)
  n = 0.319614
FEATURE [App::DocumentObjectGroupPython] G4_LUCITE  # scripted group (container) (typed FeaturePython)
  Dunit = g/cm3
  Dvalue = 1.19
  Group = -> [H_element667,C_element717,O_element628]
  conduct = 2
  density = 1
  expand = 3
  formula = G4_LUCITE
  name = G4_LUCITE
  specific = 4
FEATURE [App::DocumentObjectGroupPython] Cu_element014  label="Cu_element : 097"  # scripted group (container) (typed FeaturePython)
  n = 62
  ref = Cu_element
FEATURE [App::DocumentObjectGroupPython] Zn_element014  label="Zn_element : 043"  # scripted group (container) (typed FeaturePython)
  n = 35
  ref = Zn_element
FEATURE [App::DocumentObjectGroupPython] Pb_element029  label="Pb_element : 014"  # scripted group (container) (typed FeaturePython)
  n = 3
  ref = Pb_element
FEATURE [App::DocumentObjectGroupPython] G4_BRASS  # scripted group (container) (typed FeaturePython)
  Dunit = g/cm3
  Dvalue = 8.52
  Group = -> [Cu_element014,Zn_element014,Pb_element029]
  conduct = 2
  density = 1
  expand = 3
  formula = G4_BRASS
  name = G4_BRASS
  specific = 4
FEATURE [App::DocumentObjectGroupPython] Cu_element015  label="Cu_element : 098"  # scripted group (container) (typed FeaturePython)
  n = 89
  ref = Cu_element
FEATURE [App::DocumentObjectGroupPython] Zn_element015  label="Zn_element : 044"  # scripted group (container) (typed FeaturePython)
  n = 9
  ref = Zn_element
FEATURE [App::DocumentObjectGroupPython] Pb_element030  label="Pb_element : 015"  # scripted group (container) (typed FeaturePython)
  n = 2
  ref = Pb_element
FEATURE [App::DocumentObjectGroupPython] G4_BRONZE  # scripted group (container) (typed FeaturePython)
  Dunit = g/cm3
  Dvalue = 8.82
  Group = -> [Cu_element015,Zn_element015,Pb_element030]
  conduct = 2
  density = 1
  expand = 3
  formula = G4_BRONZE
  name = G4_BRONZE
  specific = 4
FEATURE [App::DocumentObjectGroupPython] Fe_element040  label="Fe_element : 021"  # scripted group (container) (typed FeaturePython)
  n = 74
  ref = Fe_element
FEATURE [App::DocumentObjectGroupPython] Cr_element010  label="Cr_element : 024"  # scripted group (container) (typed FeaturePython)
  n = 18
  ref = Cr_element
FEATURE [App::DocumentObjectGroupPython] Ni_element010  label="Ni_element : 014"  # scripted group (container) (typed FeaturePython)
  n = 8
  ref = Ni_element
FEATURE [App::DocumentObjectGroupPython] G4_STAINLESS_STEEL  label="G4_STAINLESS-STEEL"  # scripted group (container) (typed FeaturePython)
  Dunit = g/cm3
  Dvalue = 8
  Group = -> [Fe_element040,Cr_element010,Ni_element010]
  conduct = 2
  density = 1
  expand = 3
  formula = G4_STAINLESS-STEEL
  name = G4_STAINLESS-STEEL
  specific = 4
FEATURE [App::DocumentObjectGroupPython] H_element668  label="H_element : 432"  # scripted group (container) (typed FeaturePython)
  n = 18
  ref = H_element
FEATURE [App::DocumentObjectGroupPython] C_element718  label="C_element : 471"  # scripted group (container) (typed FeaturePython)
  n = 12
  ref = C_element
FEATURE [App::DocumentObjectGroupPython] O_element629  label="O_element : 401"  # scripted group (container) (typed FeaturePython)
  n = 7
  ref = O_element
FEATURE [App::DocumentObjectGroupPython] G4_CR39  # scripted group (container) (typed FeaturePython)
  Dunit = g/cm3
  Dvalue = 1.32
  Group = -> [H_element668,C_element718,O_element629]
  conduct = 2
  density = 1
  expand = 3
  formula = G4_CR39
  name = G4_CR39
  specific = 4
FEATURE [App::DocumentObjectGroupPython] H_element669  label="H_element : 433"  # scripted group (container) (typed FeaturePython)
  n = 38
  ref = H_element
FEATURE [App::DocumentObjectGroupPython] C_element719  label="C_element : 472"  # scripted group (container) (typed FeaturePython)
  n = 18
  ref = C_element
FEATURE [App::DocumentObjectGroupPython] O_element630  label="O_element : 402"  # scripted group (container) (typed FeaturePython)
  n = 1
  ref = O_element
FEATURE [App::DocumentObjectGroupPython] G4_OCTADECANOL  # scripted group (container) (typed FeaturePython)
  Dunit = g/cm3
  Dvalue = 0.812
  Group = -> [H_element669,C_element719,O_element630]
  conduct = 2
  density = 1
  expand = 3
  formula = G4_OCTADECANOL
  name = G4_OCTADECANOL
  specific = 4
FEATURE [App::DocumentObjectGroupPython] HEP  # scripted group (container) (typed FeaturePython)
  Group = -> [G4_lH2,G4_lN2,G4_lO2,G4_lAr,G4_lBr,G4_lKr,G4_lXe,G4_PbWO4,G4_Galactic,G4_GRAPHITE_POROUS,G4_LUCITE,G4_BRASS,G4_BRONZE,G4_STAINLESS_STEEL,G4_CR39,G4_OCTADECANOL]
FEATURE [App::DocumentObjectGroupPython] C_element720  label="C_element : 473"  # scripted group (container) (typed FeaturePython)
  n = 14
  ref = C_element
FEATURE [App::DocumentObjectGroupPython] H_element670  label="H_element : 434"  # scripted group (container) (typed FeaturePython)
  n = 10
  ref = H_element
FEATURE [App::DocumentObjectGroupPython] O_element631  label="O_element : 403"  # scripted group (container) (typed FeaturePython)
  n = 2
  ref = O_element
FEATURE [App::DocumentObjectGroupPython] N_element322  label="N_element : 174"  # scripted group (container) (typed FeaturePython)
  n = 2
  ref = N_element
FEATURE [App::DocumentObjectGroupPython] G4_KEVLAR  # scripted group (container) (typed FeaturePython)
  Dunit = g/cm3
  Dvalue = 1.44
  Group = -> [C_element720,H_element670,O_element631,N_element322]
  conduct = 2
  density = 1
  expand = 3
  formula = G4_KEVLAR
  name = G4_KEVLAR
  specific = 4
FEATURE [App::DocumentObjectGroupPython] C_element721  label="C_element : 474"  # scripted group (container) (typed FeaturePython)
  n = 10
  ref = C_element
FEATURE [App::DocumentObjectGroupPython] H_element671  label="H_element : 435"  # scripted group (container) (typed FeaturePython)
  n = 8
  ref = H_element
FEATURE [App::DocumentObjectGroupPython] O_element632  label="O_element : 404"  # scripted group (container) (typed FeaturePython)
  n = 4
  ref = O_element
FEATURE [App::DocumentObjectGroupPython] G4_DACRON  # scripted group (container) (typed FeaturePython)
  Dunit = g/cm3
  Dvalue = 1.4
  Group = -> [C_element721,H_element671,O_element632]
  conduct = 2
  density = 1
  expand = 3
  formula = G4_DACRON
  name = G4_DACRON
  specific = 4
FEATURE [App::DocumentObjectGroupPython] C_element722  label="C_element : 475"  # scripted group (container) (typed FeaturePython)
  n = 4
  ref = C_element
FEATURE [App::DocumentObjectGroupPython] H_element672  label="H_element : 436"  # scripted group (container) (typed FeaturePython)
  n = 5
  ref = H_element
FEATURE [App::DocumentObjectGroupPython] Cl_element150  label="Cl_element : 076"  # scripted group (container) (typed FeaturePython)
  n = 1
  ref = Cl_element
FEATURE [App::DocumentObjectGroupPython] G4_NEOPRENE  # scripted group (container) (typed FeaturePython)
  Dunit = g/cm3
  Dvalue = 1.23
  Group = -> [C_element722,H_element672,Cl_element150]
  conduct = 2
  density = 1
  expand = 3
  formula = G4_NEOPRENE
  name = G4_NEOPRENE
  specific = 4
FEATURE [App::DocumentObjectGroupPython] Space  # scripted group (container) (typed FeaturePython)
  Group = -> [G4_KEVLAR,G4_DACRON,G4_NEOPRENE]
FEATURE [App::DocumentObjectGroupPython] H_element673  label="H_element : 437"  # scripted group (container) (typed FeaturePython)
  n = 5
  ref = H_element
FEATURE [App::DocumentObjectGroupPython] C_element723  label="C_element : 476"  # scripted group (container) (typed FeaturePython)
  n = 4
  ref = C_element
FEATURE [App::DocumentObjectGroupPython] N_element323  label="N_element : 175"  # scripted group (container) (typed FeaturePython)
  n = 3
  ref = N_element
FEATURE [App::DocumentObjectGroupPython] O_element633  label="O_element : 405"  # scripted group (container) (typed FeaturePython)
  n = 1
  ref = O_element
FEATURE [App::DocumentObjectGroupPython] G4_CYTOSINE  # scripted group (container) (typed FeaturePython)
  Dunit = g/cm3
  Dvalue = 1.55
  Group = -> [H_element673,C_element723,N_element323,O_element633]
  conduct = 2
  density = 1
  expand = 3
  formula = G4_CYTOSINE
  name = G4_CYTOSINE
  specific = 4
FEATURE [App::DocumentObjectGroupPython] H_element674  label="H_element : 438"  # scripted group (container) (typed FeaturePython)
  n = 6
  ref = H_element
FEATURE [App::DocumentObjectGroupPython] C_element724  label="C_element : 477"  # scripted group (container) (typed FeaturePython)
  n = 5
  ref = C_element
FEATURE [App::DocumentObjectGroupPython] N_element324  label="N_element : 176"  # scripted group (container) (typed FeaturePython)
  n = 2
  ref = N_element
FEATURE [App::DocumentObjectGroupPython] O_element634  label="O_element : 406"  # scripted group (container) (typed FeaturePython)
  n = 2
  ref = O_element
FEATURE [App::DocumentObjectGroupPython] G4_THYMINE  # scripted group (container) (typed FeaturePython)
  Dunit = g/cm3
  Dvalue = 1.23
  Group = -> [H_element674,C_element724,N_element324,O_element634]
  conduct = 2
  density = 1
  expand = 3
  formula = G4_THYMINE
  name = G4_THYMINE
  specific = 4
FEATURE [App::DocumentObjectGroupPython] H_element675  label="H_element : 439"  # scripted group (container) (typed FeaturePython)
  n = 4
  ref = H_element
FEATURE [App::DocumentObjectGroupPython] C_element725  label="C_element : 478"  # scripted group (container) (typed FeaturePython)
  n = 4
  ref = C_element
FEATURE [App::DocumentObjectGroupPython] N_element325  label="N_element : 177"  # scripted group (container) (typed FeaturePython)
  n = 2
  ref = N_element
FEATURE [App::DocumentObjectGroupPython] O_element635  label="O_element : 407"  # scripted group (container) (typed FeaturePython)
  n = 2
  ref = O_element
FEATURE [App::DocumentObjectGroupPython] G4_URACIL  # scripted group (container) (typed FeaturePython)
  Dunit = g/cm3
  Dvalue = 1.32
  Group = -> [H_element675,C_element725,N_element325,O_element635]
  conduct = 2
  density = 1
  expand = 3
  formula = G4_URACIL
  name = G4_URACIL
  specific = 4
FEATURE [App::DocumentObjectGroupPython] H_element676  label="H_element : 440"  # scripted group (container) (typed FeaturePython)
  n = 4
  ref = H_element
FEATURE [App::DocumentObjectGroupPython] C_element726  label="C_element : 479"  # scripted group (container) (typed FeaturePython)
  n = 5
  ref = C_element
FEATURE [App::DocumentObjectGroupPython] N_element326  label="N_element : 178"  # scripted group (container) (typed FeaturePython)
  n = 5
  ref = N_element
FEATURE [App::DocumentObjectGroupPython] G4_DNA_ADENINE  # scripted group (container) (typed FeaturePython)
  Dunit = g/cm3
  Dvalue = 1
  Group = -> [H_element676,C_element726,N_element326]
  conduct = 2
  density = 1
  expand = 3
  formula = G4_DNA_ADENINE
  name = G4_DNA_ADENINE
  specific = 4
FEATURE [App::DocumentObjectGroupPython] H_element677  label="H_element : 441"  # scripted group (container) (typed FeaturePython)
  n = 4
  ref = H_element
FEATURE [App::DocumentObjectGroupPython] C_element727  label="C_element : 480"  # scripted group (container) (typed FeaturePython)
  n = 5
  ref = C_element
FEATURE [App::DocumentObjectGroupPython] N_element327  label="N_element : 179"  # scripted group (container) (typed FeaturePython)
  n = 5
  ref = N_element
FEATURE [App::DocumentObjectGroupPython] O_element636  label="O_element : 408"  # scripted group (container) (typed FeaturePython)
  n = 1
  ref = O_element
FEATURE [App::DocumentObjectGroupPython] G4_DNA_GUANINE  # scripted group (container) (typed FeaturePython)
  Dunit = g/cm3
  Dvalue = 1
  Group = -> [H_element677,C_element727,N_element327,O_element636]
  conduct = 2
  density = 1
  expand = 3
  formula = G4_DNA_GUANINE
  name = G4_DNA_GUANINE
  specific = 4
FEATURE [App::DocumentObjectGroupPython] H_element678  label="H_element : 442"  # scripted group (container) (typed FeaturePython)
  n = 4
  ref = H_element
FEATURE [App::DocumentObjectGroupPython] C_element728  label="C_element : 481"  # scripted group (container) (typed FeaturePython)
  n = 4
  ref = C_element
FEATURE [App::DocumentObjectGroupPython] N_element328  label="N_element : 180"  # scripted group (container) (typed FeaturePython)
  n = 3
  ref = N_element
FEATURE [App::DocumentObjectGroupPython] O_element637  label="O_element : 409"  # scripted group (container) (typed FeaturePython)
  n = 1
  ref = O_element
FEATURE [App::DocumentObjectGroupPython] G4_DNA_CYTOSINE  # scripted group (container) (typed FeaturePython)
  Dunit = g/cm3
  Dvalue = 1
  Group = -> [H_element678,C_element728,N_element328,O_element637]
  conduct = 2
  density = 1
  expand = 3
  formula = G4_DNA_CYTOSINE
  name = G4_DNA_CYTOSINE
  specific = 4
FEATURE [App::DocumentObjectGroupPython] H_element679  label="H_element : 443"  # scripted group (container) (typed FeaturePython)
  n = 5
  ref = H_element
FEATURE [App::DocumentObjectGroupPython] C_element729  label="C_element : 482"  # scripted group (container) (typed FeaturePython)
  n = 5
  ref = C_element
FEATURE [App::DocumentObjectGroupPython] N_element329  label="N_element : 181"  # scripted group (container) (typed FeaturePython)
  n = 2
  ref = N_element
FEATURE [App::DocumentObjectGroupPython] O_element638  label="O_element : 410"  # scripted group (container) (typed FeaturePython)
  n = 2
  ref = O_element
FEATURE [App::DocumentObjectGroupPython] G4_DNA_THYMINE  # scripted group (container) (typed FeaturePython)
  Dunit = g/cm3
  Dvalue = 1
  Group = -> [H_element679,C_element729,N_element329,O_element638]
  conduct = 2
  density = 1
  expand = 3
  formula = G4_DNA_THYMINE
  name = G4_DNA_THYMINE
  specific = 4
FEATURE [App::DocumentObjectGroupPython] H_element680  label="H_element : 444"  # scripted group (container) (typed FeaturePython)
  n = 3
  ref = H_element
FEATURE [App::DocumentObjectGroupPython] C_element730  label="C_element : 483"  # scripted group (container) (typed FeaturePython)
  n = 4
  ref = C_element
FEATURE [App::DocumentObjectGroupPython] N_element330  label="N_element : 182"  # scripted group (container) (typed FeaturePython)
  n = 2
  ref = N_element
FEATURE [App::DocumentObjectGroupPython] O_element639  label="O_element : 411"  # scripted group (container) (typed FeaturePython)
  n = 2
  ref = O_element
FEATURE [App::DocumentObjectGroupPython] G4_DNA_URACIL  # scripted group (container) (typed FeaturePython)
  Dunit = g/cm3
  Dvalue = 1
  Group = -> [H_element680,C_element730,N_element330,O_element639]
  conduct = 2
  density = 1
  expand = 3
  formula = G4_DNA_URACIL
  name = G4_DNA_URACIL
  specific = 4
FEATURE [App::DocumentObjectGroupPython] H_element681  label="H_element : 445"  # scripted group (container) (typed FeaturePython)
  n = 10
  ref = H_element
FEATURE [App::DocumentObjectGroupPython] C_element731  label="C_element : 484"  # scripted group (container) (typed FeaturePython)
  n = 10
  ref = C_element
FEATURE [App::DocumentObjectGroupPython] N_element331  label="N_element : 183"  # scripted group (container) (typed FeaturePython)
  n = 5
  ref = N_element
FEATURE [App::DocumentObjectGroupPython] O_element640  label="O_element : 412"  # scripted group (container) (typed FeaturePython)
  n = 4
  ref = O_element
FEATURE [App::DocumentObjectGroupPython] G4_DNA_ADENOSINE  # scripted group (container) (typed FeaturePython)
  Dunit = g/cm3
  Dvalue = 1
  Group = -> [H_element681,C_element731,N_element331,O_element640]
  conduct = 2
  density = 1
  expand = 3
  formula = G4_DNA_ADENOSINE
  name = G4_DNA_ADENOSINE
  specific = 4
FEATURE [App::DocumentObjectGroupPython] H_element682  label="H_element : 446"  # scripted group (container) (typed FeaturePython)
  n = 10
  ref = H_element
FEATURE [App::DocumentObjectGroupPython] C_element732  label="C_element : 485"  # scripted group (container) (typed FeaturePython)
  n = 10
  ref = C_element
FEATURE [App::DocumentObjectGroupPython] N_element332  label="N_element : 184"  # scripted group (container) (typed FeaturePython)
  n = 5
  ref = N_element
FEATURE [App::DocumentObjectGroupPython] O_element641  label="O_element : 413"  # scripted group (container) (typed FeaturePython)
  n = 5
  ref = O_element
FEATURE [App::DocumentObjectGroupPython] G4_DNA_GUANOSINE  # scripted group (container) (typed FeaturePython)
  Dunit = g/cm3
  Dvalue = 1
  Group = -> [H_element682,C_element732,N_element332,O_element641]
  conduct = 2
  density = 1
  expand = 3
  formula = G4_DNA_GUANOSINE
  name = G4_DNA_GUANOSINE
  specific = 4
FEATURE [App::DocumentObjectGroupPython] H_element683  label="H_element : 447"  # scripted group (container) (typed FeaturePython)
  n = 10
  ref = H_element
FEATURE [App::DocumentObjectGroupPython] C_element733  label="C_element : 486"  # scripted group (container) (typed FeaturePython)
  n = 9
  ref = C_element
FEATURE [App::DocumentObjectGroupPython] N_element333  label="N_element : 185"  # scripted group (container) (typed FeaturePython)
  n = 3
  ref = N_element
FEATURE [App::DocumentObjectGroupPython] O_element642  label="O_element : 414"  # scripted group (container) (typed FeaturePython)
  n = 5
  ref = O_element
FEATURE [App::DocumentObjectGroupPython] G4_DNA_CYTIDINE  # scripted group (container) (typed FeaturePython)
  Dunit = g/cm3
  Dvalue = 1
  Group = -> [H_element683,C_element733,N_element333,O_element642]
  conduct = 2
  density = 1
  expand = 3
  formula = G4_DNA_CYTIDINE
  name = G4_DNA_CYTIDINE
  specific = 4
FEATURE [App::DocumentObjectGroupPython] H_element684  label="H_element : 448"  # scripted group (container) (typed FeaturePython)
  n = 9
  ref = H_element
FEATURE [App::DocumentObjectGroupPython] C_element734  label="C_element : 487"  # scripted group (container) (typed FeaturePython)
  n = 9
  ref = C_element
FEATURE [App::DocumentObjectGroupPython] N_element334  label="N_element : 186"  # scripted group (container) (typed FeaturePython)
  n = 2
  ref = N_element
FEATURE [App::DocumentObjectGroupPython] O_element643  label="O_element : 415"  # scripted group (container) (typed FeaturePython)
  n = 6
  ref = O_element
FEATURE [App::DocumentObjectGroupPython] G4_DNA_URIDINE  # scripted group (container) (typed FeaturePython)
  Dunit = g/cm3
  Dvalue = 1
  Group = -> [H_element684,C_element734,N_element334,O_element643]
  conduct = 2
  density = 1
  expand = 3
  formula = G4_DNA_URIDINE
  name = G4_DNA_URIDINE
  specific = 4
FEATURE [App::DocumentObjectGroupPython] H_element685  label="H_element : 449"  # scripted group (container) (typed FeaturePython)
  n = 11
  ref = H_element
FEATURE [App::DocumentObjectGroupPython] C_element735  label="C_element : 488"  # scripted group (container) (typed FeaturePython)
  n = 10
  ref = C_element
FEATURE [App::DocumentObjectGroupPython] N_element335  label="N_element : 187"  # scripted group (container) (typed FeaturePython)
  n = 2
  ref = N_element
FEATURE [App::DocumentObjectGroupPython] O_element644  label="O_element : 416"  # scripted group (container) (typed FeaturePython)
  n = 6
  ref = O_element
FEATURE [App::DocumentObjectGroupPython] G4_DNA_METHYLURIDINE  # scripted group (container) (typed FeaturePython)
  Dunit = g/cm3
  Dvalue = 1
  Group = -> [H_element685,C_element735,N_element335,O_element644]
  conduct = 2
  density = 1
  expand = 3
  formula = G4_DNA_METHYLURIDINE
  name = G4_DNA_METHYLURIDINE
  specific = 4
FEATURE [App::DocumentObjectGroupPython] P_element090  label="P_element : 034"  # scripted group (container) (typed FeaturePython)
  n = 1
  ref = P_element
FEATURE [App::DocumentObjectGroupPython] O_element645  label="O_element : 417"  # scripted group (container) (typed FeaturePython)
  n = 3
  ref = O_element
FEATURE [App::DocumentObjectGroupPython] G4_DNA_MONOPHOSPHATE  # scripted group (container) (typed FeaturePython)
  Dunit = g/cm3
  Dvalue = 1
  Group = -> [P_element090,O_element645]
  conduct = 2
  density = 1
  expand = 3
  formula = G4_DNA_MONOPHOSPHATE
  name = G4_DNA_MONOPHOSPHATE
  specific = 4
FEATURE [App::DocumentObjectGroupPython] H_element686  label="H_element : 450"  # scripted group (container) (typed FeaturePython)
  n = 10
  ref = H_element
FEATURE [App::DocumentObjectGroupPython] C_element736  label="C_element : 489"  # scripted group (container) (typed FeaturePython)
  n = 10
  ref = C_element
FEATURE [App::DocumentObjectGroupPython] N_element336  label="N_element : 188"  # scripted group (container) (typed FeaturePython)
  n = 5
  ref = N_element
FEATURE [App::DocumentObjectGroupPython] O_element646  label="O_element : 418"  # scripted group (container) (typed FeaturePython)
  n = 7
  ref = O_element
FEATURE [App::DocumentObjectGroupPython] P_element091  label="P_element : 035"  # scripted group (container) (typed FeaturePython)
  n = 1
  ref = P_element
FEATURE [App::DocumentObjectGroupPython] G4_DNA_A  # scripted group (container) (typed FeaturePython)
  Dunit = g/cm3
  Dvalue = 1
  Group = -> [H_element686,C_element736,N_element336,O_element646,P_element091]
  conduct = 2
  density = 1
  expand = 3
  formula = G4_DNA_A
  name = G4_DNA_A
  specific = 4
FEATURE [App::DocumentObjectGroupPython] H_element687  label="H_element : 451"  # scripted group (container) (typed FeaturePython)
  n = 10
  ref = H_element
FEATURE [App::DocumentObjectGroupPython] C_element737  label="C_element : 490"  # scripted group (container) (typed FeaturePython)
  n = 10
  ref = C_element
FEATURE [App::DocumentObjectGroupPython] N_element337  label="N_element : 189"  # scripted group (container) (typed FeaturePython)
  n = 5
  ref = N_element
FEATURE [App::DocumentObjectGroupPython] O_element647  label="O_element : 419"  # scripted group (container) (typed FeaturePython)
  n = 8
  ref = O_element
FEATURE [App::DocumentObjectGroupPython] P_element092  label="P_element : 036"  # scripted group (container) (typed FeaturePython)
  n = 1
  ref = P_element
FEATURE [App::DocumentObjectGroupPython] G4_DNA_G  # scripted group (container) (typed FeaturePython)
  Dunit = g/cm3
  Dvalue = 1
  Group = -> [H_element687,C_element737,N_element337,O_element647,P_element092]
  conduct = 2
  density = 1
  expand = 3
  formula = G4_DNA_G
  name = G4_DNA_G
  specific = 4
FEATURE [App::DocumentObjectGroupPython] H_element688  label="H_element : 452"  # scripted group (container) (typed FeaturePython)
  n = 10
  ref = H_element
FEATURE [App::DocumentObjectGroupPython] C_element738  label="C_element : 491"  # scripted group (container) (typed FeaturePython)
  n = 9
  ref = C_element
FEATURE [App::DocumentObjectGroupPython] N_element338  label="N_element : 190"  # scripted group (container) (typed FeaturePython)
  n = 3
  ref = N_element
FEATURE [App::DocumentObjectGroupPython] O_element648  label="O_element : 420"  # scripted group (container) (typed FeaturePython)
  n = 8
  ref = O_element
FEATURE [App::DocumentObjectGroupPython] P_element093  label="P_element : 037"  # scripted group (container) (typed FeaturePython)
  n = 1
  ref = P_element
FEATURE [App::DocumentObjectGroupPython] G4_DNA_C  # scripted group (container) (typed FeaturePython)
  Dunit = g/cm3
  Dvalue = 1
  Group = -> [H_element688,C_element738,N_element338,O_element648,P_element093]
  conduct = 2
  density = 1
  expand = 3
  formula = G4_DNA_C
  name = G4_DNA_C
  specific = 4
FEATURE [App::DocumentObjectGroupPython] H_element689  label="H_element : 453"  # scripted group (container) (typed FeaturePython)
  n = 9
  ref = H_element
FEATURE [App::DocumentObjectGroupPython] C_element739  label="C_element : 492"  # scripted group (container) (typed FeaturePython)
  n = 9
  ref = C_element
FEATURE [App::DocumentObjectGroupPython] N_element339  label="N_element : 191"  # scripted group (container) (typed FeaturePython)
  n = 2
  ref = N_element
FEATURE [App::DocumentObjectGroupPython] O_element649  label="O_element : 421"  # scripted group (container) (typed FeaturePython)
  n = 9
  ref = O_element
FEATURE [App::DocumentObjectGroupPython] P_element094  label="P_element : 038"  # scripted group (container) (typed FeaturePython)
  n = 1
  ref = P_element
FEATURE [App::DocumentObjectGroupPython] G4_DNA_U  # scripted group (container) (typed FeaturePython)
  Dunit = g/cm3
  Dvalue = 1
  Group = -> [H_element689,C_element739,N_element339,O_element649,P_element094]
  conduct = 2
  density = 1
  expand = 3
  formula = G4_DNA_U
  name = G4_DNA_U
  specific = 4
FEATURE [App::DocumentObjectGroupPython] H_element690  label="H_element : 454"  # scripted group (container) (typed FeaturePython)
  n = 11
  ref = H_element
FEATURE [App::DocumentObjectGroupPython] C_element740  label="C_element : 493"  # scripted group (container) (typed FeaturePython)
  n = 10
  ref = C_element
FEATURE [App::DocumentObjectGroupPython] N_element340  label="N_element : 192"  # scripted group (container) (typed FeaturePython)
  n = 2
  ref = N_element
FEATURE [App::DocumentObjectGroupPython] O_element650  label="O_element : 422"  # scripted group (container) (typed FeaturePython)
  n = 9
  ref = O_element
FEATURE [App::DocumentObjectGroupPython] P_element095  label="P_element : 039"  # scripted group (container) (typed FeaturePython)
  n = 1
  ref = P_element
FEATURE [App::DocumentObjectGroupPython] G4_DNA_MU  # scripted group (container) (typed FeaturePython)
  Dunit = g/cm3
  Dvalue = 1
  Group = -> [H_element690,C_element740,N_element340,O_element650,P_element095]
  conduct = 2
  density = 1
  expand = 3
  formula = G4_DNA_MU
  name = G4_DNA_MU
  specific = 4
FEATURE [App::DocumentObjectGroupPython] BioChemical  # scripted group (container) (typed FeaturePython)
  Group = -> [G4_CYTOSINE,G4_THYMINE,G4_URACIL,G4_DNA_ADENINE,G4_DNA_GUANINE,G4_DNA_CYTOSINE,G4_DNA_THYMINE,G4_DNA_URACIL,G4_DNA_ADENOSINE,G4_DNA_GUANOSINE,G4_DNA_CYTIDINE,G4_DNA_URIDINE,G4_DNA_METHYLURIDINE,G4_DNA_MONOPHOSPHATE,G4_DNA_A,G4_DNA_G,G4_DNA_C,G4_DNA_U,G4_DNA_MU]
FEATURE [App::DocumentObjectGroupPython] G4Materials  # scripted group (container) (typed FeaturePython)
  Group = -> [NIST,Element,HEP,Space,BioChemical]
FEATURE [App::DocumentObjectGroupPython] Geant4  # scripted group (container) (typed FeaturePython)
  Group = -> [G4Isotopes,G4Elements,G4Materials]
FEATURE [App::DocumentObjectGroupPython] Materials  # scripted group (container) (typed FeaturePython)
  Group = -> [Geant4]
FEATURE [Part::FeaturePython] GDMLCone_Cone  # WARN: FeaturePython — macro-defined, semantics opaque (R4)
  Placement = pos=(20,0,0) rot=(0,0,1;0rad)
  aunit = 0
  deltaphi = 2
  lunit = 2
  material = 0
  rmax1 = 3
  rmax2 = 7
  rmin1 = 1
  rmin2 = 4
  startphi = 0
  z = 10
FEATURE [App::Part] LV_Tube  label="Tube"
  Group = -> [GDMLTube_Tube002,GDMLCone_Cone]
  Origin = -> Origin006
  Placement = pos=(57,0,0) rot=(0,1,0;1.5708rad)
FEATURE [App::Part] Part  label="DetectorAssembly"
  Group = -> [Bool_Union001,LV_Tube]
  Origin = -> Origin007
FEATURE [App::Part] worldVOL
  Group = -> [GDMLBox_WorldBox,Part,Part001]
  Origin = -> Origin
